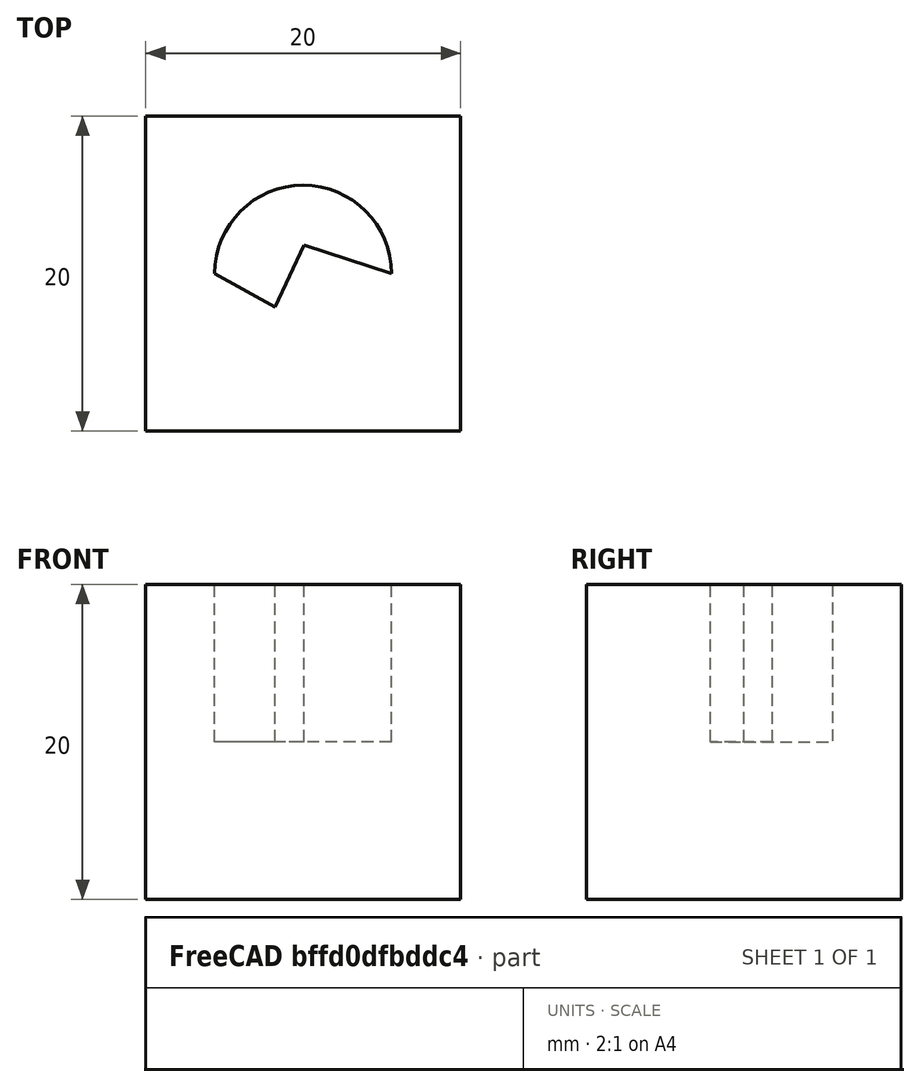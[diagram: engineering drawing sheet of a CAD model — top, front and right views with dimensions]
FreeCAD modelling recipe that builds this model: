
FCSTD DOCUMENT  (FreeCAD 1.0R39109 (Git))
Label: extrudeLimitation-1
License: All rights reserved
LicenseURL: http://en.wikipedia.org/wiki/All_rights_reserved
objects: App::DocumentObjectGroupPython×1248, App::Part×2, Part::FeaturePython×1, Sketcher::SketchObject×1, Part::Extrusion×1
note: 4 computed .brp shape members not serialized (recipe doc carries the construction recipe); baked Part::Feature solids carry a one-line shape summary decoded from their .brp

FEATURE [App::DocumentObjectGroupPython] HALFPI  # scripted group (container) (typed FeaturePython)
  name = HALFPI
  value = pi/2.
FEATURE [App::DocumentObjectGroupPython] PI  # scripted group (container) (typed FeaturePython)
  name = PI
  value = 1.*pi
FEATURE [App::DocumentObjectGroupPython] TWOPI  # scripted group (container) (typed FeaturePython)
  name = TWOPI
  value = 2.*pi
FEATURE [App::DocumentObjectGroupPython] Constants  # scripted group (container) (typed FeaturePython)
  Group = -> [HALFPI,PI,TWOPI]
FEATURE [App::DocumentObjectGroupPython] Variables  # scripted group (container) (typed FeaturePython)
FEATURE [App::DocumentObjectGroupPython] Quantities  # scripted group (container) (typed FeaturePython)
FEATURE [App::DocumentObjectGroupPython] Isotopes  # scripted group (container) (typed FeaturePython)
FEATURE [App::DocumentObjectGroupPython] Elements  # scripted group (container) (typed FeaturePython)
FEATURE [App::DocumentObjectGroupPython] G4Isotopes  # scripted group (container) (typed FeaturePython)
FEATURE [App::DocumentObjectGroupPython] H_element  # scripted group (container) (typed FeaturePython)
  Z = 1
  atom_value = 1.008
  formula = H
  name = H_element
FEATURE [App::DocumentObjectGroupPython] He_element  # scripted group (container) (typed FeaturePython)
  Z = 2
  atom_value = 4.0026
  formula = He
  name = He_element
FEATURE [App::DocumentObjectGroupPython] Li_element  # scripted group (container) (typed FeaturePython)
  Z = 3
  atom_value = 6.94
  formula = Li
  name = Li_element
FEATURE [App::DocumentObjectGroupPython] Be_element  # scripted group (container) (typed FeaturePython)
  Z = 4
  atom_value = 9.01218
  formula = Be
  name = Be_element
FEATURE [App::DocumentObjectGroupPython] B_element  # scripted group (container) (typed FeaturePython)
  Z = 5
  atom_value = 10.81
  formula = B
  name = B_element
FEATURE [App::DocumentObjectGroupPython] C_element  # scripted group (container) (typed FeaturePython)
  Z = 6
  atom_value = 12.011
  formula = C
  name = C_element
FEATURE [App::DocumentObjectGroupPython] N_element  # scripted group (container) (typed FeaturePython)
  Z = 7
  atom_value = 14.007
  formula = N
  name = N_element
FEATURE [App::DocumentObjectGroupPython] O_element  # scripted group (container) (typed FeaturePython)
  Z = 8
  atom_value = 15.999
  formula = O
  name = O_element
FEATURE [App::DocumentObjectGroupPython] F_element  # scripted group (container) (typed FeaturePython)
  Z = 9
  atom_value = 18.9984
  formula = F
  name = F_element
FEATURE [App::DocumentObjectGroupPython] Ne_element  # scripted group (container) (typed FeaturePython)
  Z = 10
  atom_value = 20.1797
  formula = Ne
  name = Ne_element
FEATURE [App::DocumentObjectGroupPython] Na_element  # scripted group (container) (typed FeaturePython)
  Z = 11
  atom_value = 22.9898
  formula = Na
  name = Na_element
FEATURE [App::DocumentObjectGroupPython] Mg_element  # scripted group (container) (typed FeaturePython)
  Z = 12
  atom_value = 24.305
  formula = Mg
  name = Mg_element
FEATURE [App::DocumentObjectGroupPython] Al_element  # scripted group (container) (typed FeaturePython)
  Z = 13
  atom_value = 26.9815
  formula = Al
  name = Al_element
FEATURE [App::DocumentObjectGroupPython] Si_element  # scripted group (container) (typed FeaturePython)
  Z = 14
  atom_value = 28.085
  formula = Si
  name = Si_element
FEATURE [App::DocumentObjectGroupPython] P_element  # scripted group (container) (typed FeaturePython)
  Z = 15
  atom_value = 30.9738
  formula = P
  name = P_element
FEATURE [App::DocumentObjectGroupPython] S_element  # scripted group (container) (typed FeaturePython)
  Z = 16
  atom_value = 32.06
  formula = S
  name = S_element
FEATURE [App::DocumentObjectGroupPython] Cl_element  # scripted group (container) (typed FeaturePython)
  Z = 17
  atom_value = 35.45
  formula = Cl
  name = Cl_element
FEATURE [App::DocumentObjectGroupPython] Ar_element  # scripted group (container) (typed FeaturePython)
  Z = 18
  atom_value = 39.95
  formula = Ar
  name = Ar_element
FEATURE [App::DocumentObjectGroupPython] K_element  # scripted group (container) (typed FeaturePython)
  Z = 19
  atom_value = 39.0983
  formula = K
  name = K_element
FEATURE [App::DocumentObjectGroupPython] Ca_element  # scripted group (container) (typed FeaturePython)
  Z = 20
  atom_value = 40.078
  formula = Ca
  name = Ca_element
FEATURE [App::DocumentObjectGroupPython] Sc_element  # scripted group (container) (typed FeaturePython)
  Z = 21
  atom_value = 44.9559
  formula = Sc
  name = Sc_element
FEATURE [App::DocumentObjectGroupPython] Ti_element  # scripted group (container) (typed FeaturePython)
  Z = 22
  atom_value = 47.867
  formula = Ti
  name = Ti_element
FEATURE [App::DocumentObjectGroupPython] V_element  # scripted group (container) (typed FeaturePython)
  Z = 23
  atom_value = 50.9415
  formula = V
  name = V_element
FEATURE [App::DocumentObjectGroupPython] Cr_element  # scripted group (container) (typed FeaturePython)
  Z = 24
  atom_value = 51.9961
  formula = Cr
  name = Cr_element
FEATURE [App::DocumentObjectGroupPython] Mn_element  # scripted group (container) (typed FeaturePython)
  Z = 25
  atom_value = 54.938
  formula = Mn
  name = Mn_element
FEATURE [App::DocumentObjectGroupPython] Fe_element  # scripted group (container) (typed FeaturePython)
  Z = 26
  atom_value = 55.845
  formula = Fe
  name = Fe_element
FEATURE [App::DocumentObjectGroupPython] Co_element  # scripted group (container) (typed FeaturePython)
  Z = 27
  atom_value = 58.9332
  formula = Co
  name = Co_element
FEATURE [App::DocumentObjectGroupPython] Ni_element  # scripted group (container) (typed FeaturePython)
  Z = 28
  atom_value = 58.6934
  formula = Ni
  name = Ni_element
FEATURE [App::DocumentObjectGroupPython] Cu_element  # scripted group (container) (typed FeaturePython)
  Z = 29
  atom_value = 63.546
  formula = Cu
  name = Cu_element
FEATURE [App::DocumentObjectGroupPython] Zn_element  # scripted group (container) (typed FeaturePython)
  Z = 30
  atom_value = 65.38
  formula = Zn
  name = Zn_element
FEATURE [App::DocumentObjectGroupPython] Ga_element  # scripted group (container) (typed FeaturePython)
  Z = 31
  atom_value = 69.723
  formula = Ga
  name = Ga_element
FEATURE [App::DocumentObjectGroupPython] Ge_element  # scripted group (container) (typed FeaturePython)
  Z = 32
  atom_value = 72.63
  formula = Ge
  name = Ge_element
FEATURE [App::DocumentObjectGroupPython] As_element  # scripted group (container) (typed FeaturePython)
  Z = 33
  atom_value = 74.9216
  formula = As
  name = As_element
FEATURE [App::DocumentObjectGroupPython] Se_element  # scripted group (container) (typed FeaturePython)
  Z = 34
  atom_value = 78.971
  formula = Se
  name = Se_element
FEATURE [App::DocumentObjectGroupPython] Br_element  # scripted group (container) (typed FeaturePython)
  Z = 35
  atom_value = 79.904
  formula = Br
  name = Br_element
FEATURE [App::DocumentObjectGroupPython] Kr_element  # scripted group (container) (typed FeaturePython)
  Z = 36
  atom_value = 83.798
  formula = Kr
  name = Kr_element
FEATURE [App::DocumentObjectGroupPython] Rb_element  # scripted group (container) (typed FeaturePython)
  Z = 37
  atom_value = 85.4678
  formula = Rb
  name = Rb_element
FEATURE [App::DocumentObjectGroupPython] Sr_element  # scripted group (container) (typed FeaturePython)
  Z = 38
  atom_value = 87.62
  formula = Sr
  name = Sr_element
FEATURE [App::DocumentObjectGroupPython] Y_element  # scripted group (container) (typed FeaturePython)
  Z = 39
  atom_value = 88.9058
  formula = Y
  name = Y_element
FEATURE [App::DocumentObjectGroupPython] Zr_element  # scripted group (container) (typed FeaturePython)
  Z = 40
  atom_value = 91.224
  formula = Zr
  name = Zr_element
FEATURE [App::DocumentObjectGroupPython] Nb_element  # scripted group (container) (typed FeaturePython)
  Z = 41
  atom_value = 92.9064
  formula = Nb
  name = Nb_element
FEATURE [App::DocumentObjectGroupPython] Mo_element  # scripted group (container) (typed FeaturePython)
  Z = 42
  atom_value = 95.95
  formula = Mo
  name = Mo_element
FEATURE [App::DocumentObjectGroupPython] Tc_element  # scripted group (container) (typed FeaturePython)
  Z = 43
  atom_value = 97
  formula = Tc
  name = Tc_element
FEATURE [App::DocumentObjectGroupPython] Ru_element  # scripted group (container) (typed FeaturePython)
  Z = 44
  atom_value = 101.07
  formula = Ru
  name = Ru_element
FEATURE [App::DocumentObjectGroupPython] Rh_element  # scripted group (container) (typed FeaturePython)
  Z = 45
  atom_value = 102.905
  formula = Rh
  name = Rh_element
FEATURE [App::DocumentObjectGroupPython] Pd_element  # scripted group (container) (typed FeaturePython)
  Z = 46
  atom_value = 106.42
  formula = Pd
  name = Pd_element
FEATURE [App::DocumentObjectGroupPython] Ag_element  # scripted group (container) (typed FeaturePython)
  Z = 47
  atom_value = 107.868
  formula = Ag
  name = Ag_element
FEATURE [App::DocumentObjectGroupPython] Cd_element  # scripted group (container) (typed FeaturePython)
  Z = 48
  atom_value = 112.414
  formula = Cd
  name = Cd_element
FEATURE [App::DocumentObjectGroupPython] In_element  # scripted group (container) (typed FeaturePython)
  Z = 49
  atom_value = 114.818
  formula = In
  name = In_element
FEATURE [App::DocumentObjectGroupPython] Sn_element  # scripted group (container) (typed FeaturePython)
  Z = 50
  atom_value = 118.71
  formula = Sn
  name = Sn_element
FEATURE [App::DocumentObjectGroupPython] Sb_element  # scripted group (container) (typed FeaturePython)
  Z = 51
  atom_value = 121.76
  formula = Sb
  name = Sb_element
FEATURE [App::DocumentObjectGroupPython] Te_element  # scripted group (container) (typed FeaturePython)
  Z = 52
  atom_value = 127.6
  formula = Te
  name = Te_element
FEATURE [App::DocumentObjectGroupPython] I_element  # scripted group (container) (typed FeaturePython)
  Z = 53
  atom_value = 126.904
  formula = I
  name = I_element
FEATURE [App::DocumentObjectGroupPython] Xe_element  # scripted group (container) (typed FeaturePython)
  Z = 54
  atom_value = 131.293
  formula = Xe
  name = Xe_element
FEATURE [App::DocumentObjectGroupPython] Cs_element  # scripted group (container) (typed FeaturePython)
  Z = 55
  atom_value = 132.905
  formula = Cs
  name = Cs_element
FEATURE [App::DocumentObjectGroupPython] Ba_element  # scripted group (container) (typed FeaturePython)
  Z = 56
  atom_value = 137.327
  formula = Ba
  name = Ba_element
FEATURE [App::DocumentObjectGroupPython] La_element  # scripted group (container) (typed FeaturePython)
  Z = 57
  atom_value = 138.905
  formula = La
  name = La_element
FEATURE [App::DocumentObjectGroupPython] Ce_element  # scripted group (container) (typed FeaturePython)
  Z = 58
  atom_value = 140.116
  formula = Ce
  name = Ce_element
FEATURE [App::DocumentObjectGroupPython] Pr_element  # scripted group (container) (typed FeaturePython)
  Z = 59
  atom_value = 140.908
  formula = Pr
  name = Pr_element
FEATURE [App::DocumentObjectGroupPython] Nd_element  # scripted group (container) (typed FeaturePython)
  Z = 60
  atom_value = 144.242
  formula = Nd
  name = Nd_element
FEATURE [App::DocumentObjectGroupPython] Pm_element  # scripted group (container) (typed FeaturePython)
  Z = 61
  atom_value = 145
  formula = Pm
  name = Pm_element
FEATURE [App::DocumentObjectGroupPython] Sm_element  # scripted group (container) (typed FeaturePython)
  Z = 62
  atom_value = 150.36
  formula = Sm
  name = Sm_element
FEATURE [App::DocumentObjectGroupPython] Eu_element  # scripted group (container) (typed FeaturePython)
  Z = 63
  atom_value = 151.964
  formula = Eu
  name = Eu_element
FEATURE [App::DocumentObjectGroupPython] Gd_element  # scripted group (container) (typed FeaturePython)
  Z = 64
  atom_value = 157.25
  formula = Gd
  name = Gd_element
FEATURE [App::DocumentObjectGroupPython] Tb_element  # scripted group (container) (typed FeaturePython)
  Z = 65
  atom_value = 158.925
  formula = Tb
  name = Tb_element
FEATURE [App::DocumentObjectGroupPython] Dy_element  # scripted group (container) (typed FeaturePython)
  Z = 66
  atom_value = 162.5
  formula = Dy
  name = Dy_element
FEATURE [App::DocumentObjectGroupPython] Ho_element  # scripted group (container) (typed FeaturePython)
  Z = 67
  atom_value = 164.93
  formula = Ho
  name = Ho_element
FEATURE [App::DocumentObjectGroupPython] Er_element  # scripted group (container) (typed FeaturePython)
  Z = 68
  atom_value = 167.259
  formula = Er
  name = Er_element
FEATURE [App::DocumentObjectGroupPython] Tm_element  # scripted group (container) (typed FeaturePython)
  Z = 69
  atom_value = 168.934
  formula = Tm
  name = Tm_element
FEATURE [App::DocumentObjectGroupPython] Yb_element  # scripted group (container) (typed FeaturePython)
  Z = 70
  atom_value = 173.045
  formula = Yb
  name = Yb_element
FEATURE [App::DocumentObjectGroupPython] Lu_element  # scripted group (container) (typed FeaturePython)
  Z = 71
  atom_value = 174.967
  formula = Lu
  name = Lu_element
FEATURE [App::DocumentObjectGroupPython] Hf_element  # scripted group (container) (typed FeaturePython)
  Z = 72
  atom_value = 178.49
  formula = Hf
  name = Hf_element
FEATURE [App::DocumentObjectGroupPython] Ta_element  # scripted group (container) (typed FeaturePython)
  Z = 73
  atom_value = 180.948
  formula = Ta
  name = Ta_element
FEATURE [App::DocumentObjectGroupPython] W_element  # scripted group (container) (typed FeaturePython)
  Z = 74
  atom_value = 183.84
  formula = W
  name = W_element
FEATURE [App::DocumentObjectGroupPython] Re_element  # scripted group (container) (typed FeaturePython)
  Z = 75
  atom_value = 186.207
  formula = Re
  name = Re_element
FEATURE [App::DocumentObjectGroupPython] Os_element  # scripted group (container) (typed FeaturePython)
  Z = 76
  atom_value = 190.23
  formula = Os
  name = Os_element
FEATURE [App::DocumentObjectGroupPython] Ir_element  # scripted group (container) (typed FeaturePython)
  Z = 77
  atom_value = 192.217
  formula = Ir
  name = Ir_element
FEATURE [App::DocumentObjectGroupPython] Pt_element  # scripted group (container) (typed FeaturePython)
  Z = 78
  atom_value = 195.084
  formula = Pt
  name = Pt_element
FEATURE [App::DocumentObjectGroupPython] Au_element  # scripted group (container) (typed FeaturePython)
  Z = 79
  atom_value = 196.967
  formula = Au
  name = Au_element
FEATURE [App::DocumentObjectGroupPython] Hg_element  # scripted group (container) (typed FeaturePython)
  Z = 80
  atom_value = 200.592
  formula = Hg
  name = Hg_element
FEATURE [App::DocumentObjectGroupPython] Tl_element  # scripted group (container) (typed FeaturePython)
  Z = 81
  atom_value = 204.38
  formula = Tl
  name = Tl_element
FEATURE [App::DocumentObjectGroupPython] Pb_element  # scripted group (container) (typed FeaturePython)
  Z = 82
  atom_value = 207.2
  formula = Pb
  name = Pb_element
FEATURE [App::DocumentObjectGroupPython] Bi_element  # scripted group (container) (typed FeaturePython)
  Z = 83
  atom_value = 208.98
  formula = Bi
  name = Bi_element
FEATURE [App::DocumentObjectGroupPython] Po_element  # scripted group (container) (typed FeaturePython)
  Z = 84
  atom_value = 209
  formula = Po
  name = Po_element
FEATURE [App::DocumentObjectGroupPython] At_element  # scripted group (container) (typed FeaturePython)
  Z = 85
  atom_value = 210
  formula = At
  name = At_element
FEATURE [App::DocumentObjectGroupPython] Rn_element  # scripted group (container) (typed FeaturePython)
  Z = 86
  atom_value = 222
  formula = Rn
  name = Rn_element
FEATURE [App::DocumentObjectGroupPython] Fr_element  # scripted group (container) (typed FeaturePython)
  Z = 87
  atom_value = 223
  formula = Fr
  name = Fr_element
FEATURE [App::DocumentObjectGroupPython] Ra_element  # scripted group (container) (typed FeaturePython)
  Z = 88
  atom_value = 226
  formula = Ra
  name = Ra_element
FEATURE [App::DocumentObjectGroupPython] Ac_element  # scripted group (container) (typed FeaturePython)
  Z = 89
  atom_value = 227
  formula = Ac
  name = Ac_element
FEATURE [App::DocumentObjectGroupPython] Th_element  # scripted group (container) (typed FeaturePython)
  Z = 90
  atom_value = 232.038
  formula = Th
  name = Th_element
FEATURE [App::DocumentObjectGroupPython] Pa_element  # scripted group (container) (typed FeaturePython)
  Z = 91
  atom_value = 231.036
  formula = Pa
  name = Pa_element
FEATURE [App::DocumentObjectGroupPython] U_element  # scripted group (container) (typed FeaturePython)
  Z = 92
  atom_value = 238.029
  formula = U
  name = U_element
FEATURE [App::DocumentObjectGroupPython] Np_element  # scripted group (container) (typed FeaturePython)
  Z = 93
  atom_value = 237
  formula = Np
  name = Np_element
FEATURE [App::DocumentObjectGroupPython] Pu_element  # scripted group (container) (typed FeaturePython)
  Z = 94
  atom_value = 244
  formula = Pu
  name = Pu_element
FEATURE [App::DocumentObjectGroupPython] Am_element  # scripted group (container) (typed FeaturePython)
  Z = 95
  atom_value = 243
  formula = Am
  name = Am_element
FEATURE [App::DocumentObjectGroupPython] Cm_element  # scripted group (container) (typed FeaturePython)
  Z = 96
  atom_value = 247
  formula = Cm
  name = Cm_element
FEATURE [App::DocumentObjectGroupPython] Bk_element  # scripted group (container) (typed FeaturePython)
  Z = 97
  atom_value = 247
  formula = Bk
  name = Bk_element
FEATURE [App::DocumentObjectGroupPython] Cf_element  # scripted group (container) (typed FeaturePython)
  Z = 98
  atom_value = 251
  formula = Cf
  name = Cf_element
FEATURE [App::DocumentObjectGroupPython] G4Elements  # scripted group (container) (typed FeaturePython)
  Group = -> [H_element,He_element,Li_element,Be_element,B_element,C_element,N_element,O_element,F_element,Ne_element,Na_element,Mg_element,Al_element,Si_element,P_element,S_element,Cl_element,Ar_element,K_element,Ca_element,Sc_element,Ti_element,V_element,Cr_element,Mn_element,Fe_element,Co_element,Ni_element,Cu_element,Zn_element,Ga_element,Ge_element,As_element,Se_element,Br_element,Kr_element,Rb_element,+61 more]
FEATURE [App::DocumentObjectGroupPython] H_element001  label="H_element : 0.101"  # scripted group (container) (typed FeaturePython)
  n = 0.101327
FEATURE [App::DocumentObjectGroupPython] C_element001  label="C_element : 0.775"  # scripted group (container) (typed FeaturePython)
  n = 0.7755
FEATURE [App::DocumentObjectGroupPython] N_element001  label="N_element : 0.035"  # scripted group (container) (typed FeaturePython)
  n = 0.035057
FEATURE [App::DocumentObjectGroupPython] O_element001  label="O_element : 0.052"  # scripted group (container) (typed FeaturePython)
  n = 0.0523159
FEATURE [App::DocumentObjectGroupPython] F_element001  label="F_element : 0.017"  # scripted group (container) (typed FeaturePython)
  n = 0.017422
FEATURE [App::DocumentObjectGroupPython] Ca_element001  label="Ca_element : 0.018"  # scripted group (container) (typed FeaturePython)
  n = 0.018378
FEATURE [App::DocumentObjectGroupPython] G4_A_150_TISSUE  label="G4_A-150_TISSUE"  # scripted group (container) (typed FeaturePython)
  Dunit = g/cm3
  Dvalue = 1.127
  Group = -> [H_element001,C_element001,N_element001,O_element001,F_element001,Ca_element001]
  conduct = 2
  density = 1
  expand = 3
  formula = G4_A-150_TISSUE
  name = G4_A-150_TISSUE
  specific = 4
FEATURE [App::DocumentObjectGroupPython] C_element002  label="C_element : 3"  # scripted group (container) (typed FeaturePython)
  n = 3
  ref = C_element
FEATURE [App::DocumentObjectGroupPython] H_element002  label="H_element : 6"  # scripted group (container) (typed FeaturePython)
  n = 6
  ref = H_element
FEATURE [App::DocumentObjectGroupPython] O_element002  label="O_element : 1"  # scripted group (container) (typed FeaturePython)
  n = 1
  ref = O_element
FEATURE [App::DocumentObjectGroupPython] G4_ACETONE  # scripted group (container) (typed FeaturePython)
  Dunit = g/cm3
  Dvalue = 0.7899
  Group = -> [C_element002,H_element002,O_element002]
  conduct = 2
  density = 1
  expand = 3
  formula = G4_ACETONE
  name = G4_ACETONE
  specific = 4
FEATURE [App::DocumentObjectGroupPython] C_element003  label="C_element : 2"  # scripted group (container) (typed FeaturePython)
  n = 2
  ref = C_element
FEATURE [App::DocumentObjectGroupPython] H_element003  label="H_element : 2"  # scripted group (container) (typed FeaturePython)
  n = 2
  ref = H_element
FEATURE [App::DocumentObjectGroupPython] G4_ACETYLENE  # scripted group (container) (typed FeaturePython)
  Dunit = g/cm3
  Dvalue = 0.0010967
  Group = -> [C_element003,H_element003]
  conduct = 2
  density = 1
  expand = 3
  formula = G4_ACETYLENE
  name = G4_ACETYLENE
  specific = 4
FEATURE [App::DocumentObjectGroupPython] C_element004  label="C_element : 5"  # scripted group (container) (typed FeaturePython)
  n = 5
  ref = C_element
FEATURE [App::DocumentObjectGroupPython] H_element004  label="H_element : 5"  # scripted group (container) (typed FeaturePython)
  n = 5
  ref = H_element
FEATURE [App::DocumentObjectGroupPython] N_element002  label="N_element : 5"  # scripted group (container) (typed FeaturePython)
  n = 5
  ref = N_element
FEATURE [App::DocumentObjectGroupPython] G4_ADENINE  # scripted group (container) (typed FeaturePython)
  Dunit = g/cm3
  Dvalue = 1.6
  Group = -> [C_element004,H_element004,N_element002]
  conduct = 2
  density = 1
  expand = 3
  formula = G4_ADENINE
  name = G4_ADENINE
  specific = 4
FEATURE [App::DocumentObjectGroupPython] H_element005  label="H_element : 0.114"  # scripted group (container) (typed FeaturePython)
  n = 0.114
FEATURE [App::DocumentObjectGroupPython] C_element005  label="C_element : 0.598"  # scripted group (container) (typed FeaturePython)
  n = 0.598
FEATURE [App::DocumentObjectGroupPython] N_element003  label="N_element : 0.007"  # scripted group (container) (typed FeaturePython)
  n = 0.007
FEATURE [App::DocumentObjectGroupPython] O_element003  label="O_element : 0.278"  # scripted group (container) (typed FeaturePython)
  n = 0.278
FEATURE [App::DocumentObjectGroupPython] Na_element001  label="Na_element : 0.001"  # scripted group (container) (typed FeaturePython)
  n = 0.001
FEATURE [App::DocumentObjectGroupPython] S_element001  label="S_element : 0.001"  # scripted group (container) (typed FeaturePython)
  n = 0.001
FEATURE [App::DocumentObjectGroupPython] Cl_element001  label="Cl_element : 0.001"  # scripted group (container) (typed FeaturePython)
  n = 0.001
FEATURE [App::DocumentObjectGroupPython] G4_ADIPOSE_TISSUE_ICRP  # scripted group (container) (typed FeaturePython)
  Dunit = g/cm3
  Dvalue = 0.95
  Group = -> [H_element005,C_element005,N_element003,O_element003,Na_element001,S_element001,Cl_element001]
  conduct = 2
  density = 1
  expand = 3
  formula = G4_ADIPOSE_TISSUE_ICRP
  name = G4_ADIPOSE_TISSUE_ICRP
  specific = 4
FEATURE [App::DocumentObjectGroupPython] C_element006  label="C_element : 0.000"  # scripted group (container) (typed FeaturePython)
  n = 0.000124
FEATURE [App::DocumentObjectGroupPython] N_element004  label="N_element : 0.755"  # scripted group (container) (typed FeaturePython)
  n = 0.755268
FEATURE [App::DocumentObjectGroupPython] O_element004  label="O_element : 0.232"  # scripted group (container) (typed FeaturePython)
  n = 0.231781
FEATURE [App::DocumentObjectGroupPython] Ar_element001  label="Ar_element : 0.013"  # scripted group (container) (typed FeaturePython)
  n = 0.012827
FEATURE [App::DocumentObjectGroupPython] G4_AIR  # scripted group (container) (typed FeaturePython)
  Dunit = g/cm3
  Dvalue = 0.00120479
  Group = -> [C_element006,N_element004,O_element004,Ar_element001]
  conduct = 2
  density = 1
  expand = 3
  formula = G4_AIR
  name = G4_AIR
  specific = 4
FEATURE [App::DocumentObjectGroupPython] C_element007  label="C_element : 006"  # scripted group (container) (typed FeaturePython)
  n = 3
  ref = C_element
FEATURE [App::DocumentObjectGroupPython] H_element006  label="H_element : 7"  # scripted group (container) (typed FeaturePython)
  n = 7
  ref = H_element
FEATURE [App::DocumentObjectGroupPython] N_element005  label="N_element : 1"  # scripted group (container) (typed FeaturePython)
  n = 1
  ref = N_element
FEATURE [App::DocumentObjectGroupPython] O_element005  label="O_element : 2"  # scripted group (container) (typed FeaturePython)
  n = 2
  ref = O_element
FEATURE [App::DocumentObjectGroupPython] G4_ALANINE  # scripted group (container) (typed FeaturePython)
  Dunit = g/cm3
  Dvalue = 1.42
  Group = -> [C_element007,H_element006,N_element005,O_element005]
  conduct = 2
  density = 1
  expand = 3
  formula = G4_ALANINE
  name = G4_ALANINE
  specific = 4
FEATURE [App::DocumentObjectGroupPython] Al_element001  label="Al_element : 2"  # scripted group (container) (typed FeaturePython)
  n = 2
  ref = Al_element
FEATURE [App::DocumentObjectGroupPython] O_element006  label="O_element : 3"  # scripted group (container) (typed FeaturePython)
  n = 3
  ref = O_element
FEATURE [App::DocumentObjectGroupPython] G4_ALUMINUM_OXIDE  # scripted group (container) (typed FeaturePython)
  Dunit = g/cm3
  Dvalue = 3.97
  Group = -> [Al_element001,O_element006]
  conduct = 2
  density = 1
  expand = 3
  formula = G4_ALUMINUM_OXIDE
  name = G4_ALUMINUM_OXIDE
  specific = 4
FEATURE [App::DocumentObjectGroupPython] H_element007  label="H_element : 0.106"  # scripted group (container) (typed FeaturePython)
  n = 0.10593
FEATURE [App::DocumentObjectGroupPython] C_element008  label="C_element : 0.789"  # scripted group (container) (typed FeaturePython)
  n = 0.788974
FEATURE [App::DocumentObjectGroupPython] O_element007  label="O_element : 0.105"  # scripted group (container) (typed FeaturePython)
  n = 0.105096
FEATURE [App::DocumentObjectGroupPython] G4_AMBER  # scripted group (container) (typed FeaturePython)
  Dunit = g/cm3
  Dvalue = 1.1
  Group = -> [H_element007,C_element008,O_element007]
  conduct = 2
  density = 1
  expand = 3
  formula = G4_AMBER
  name = G4_AMBER
  specific = 4
FEATURE [App::DocumentObjectGroupPython] N_element006  label="N_element : 006"  # scripted group (container) (typed FeaturePython)
  n = 1
  ref = N_element
FEATURE [App::DocumentObjectGroupPython] H_element008  label="H_element : 3"  # scripted group (container) (typed FeaturePython)
  n = 3
  ref = H_element
FEATURE [App::DocumentObjectGroupPython] G4_AMMONIA  # scripted group (container) (typed FeaturePython)
  Dunit = g/cm3
  Dvalue = 0.000826019
  Group = -> [N_element006,H_element008]
  conduct = 2
  density = 1
  expand = 3
  formula = G4_AMMONIA
  name = G4_AMMONIA
  specific = 4
FEATURE [App::DocumentObjectGroupPython] C_element009  label="C_element : 6"  # scripted group (container) (typed FeaturePython)
  n = 6
  ref = C_element
FEATURE [App::DocumentObjectGroupPython] H_element009  label="H_element : 008"  # scripted group (container) (typed FeaturePython)
  n = 7
  ref = H_element
FEATURE [App::DocumentObjectGroupPython] N_element007  label="N_element : 007"  # scripted group (container) (typed FeaturePython)
  n = 1
  ref = N_element
FEATURE [App::DocumentObjectGroupPython] G4_ANILINE  # scripted group (container) (typed FeaturePython)
  Dunit = g/cm3
  Dvalue = 1.0235
  Group = -> [C_element009,H_element009,N_element007]
  conduct = 2
  density = 1
  expand = 3
  formula = G4_ANILINE
  name = G4_ANILINE
  specific = 4
FEATURE [App::DocumentObjectGroupPython] C_element010  label="C_element : 14"  # scripted group (container) (typed FeaturePython)
  n = 14
  ref = C_element
FEATURE [App::DocumentObjectGroupPython] H_element010  label="H_element : 10"  # scripted group (container) (typed FeaturePython)
  n = 10
  ref = H_element
FEATURE [App::DocumentObjectGroupPython] G4_ANTHRACENE  # scripted group (container) (typed FeaturePython)
  Dunit = g/cm3
  Dvalue = 1.283
  Group = -> [C_element010,H_element010]
  conduct = 2
  density = 1
  expand = 3
  formula = G4_ANTHRACENE
  name = G4_ANTHRACENE
  specific = 4
FEATURE [App::DocumentObjectGroupPython] H_element011  label="H_element : 0.065"  # scripted group (container) (typed FeaturePython)
  n = 0.0654709
FEATURE [App::DocumentObjectGroupPython] C_element011  label="C_element : 0.537"  # scripted group (container) (typed FeaturePython)
  n = 0.536944
FEATURE [App::DocumentObjectGroupPython] N_element008  label="N_element : 0.021"  # scripted group (container) (typed FeaturePython)
  n = 0.0215
FEATURE [App::DocumentObjectGroupPython] O_element008  label="O_element : 0.032"  # scripted group (container) (typed FeaturePython)
  n = 0.032085
FEATURE [App::DocumentObjectGroupPython] F_element002  label="F_element : 0.167"  # scripted group (container) (typed FeaturePython)
  n = 0.167411
FEATURE [App::DocumentObjectGroupPython] Ca_element002  label="Ca_element : 0.177"  # scripted group (container) (typed FeaturePython)
  n = 0.176589
FEATURE [App::DocumentObjectGroupPython] G4_B_100_BONE  label="G4_B-100_BONE"  # scripted group (container) (typed FeaturePython)
  Dunit = g/cm3
  Dvalue = 1.45
  Group = -> [H_element011,C_element011,N_element008,O_element008,F_element002,Ca_element002]
  conduct = 2
  density = 1
  expand = 3
  formula = G4_B-100_BONE
  name = G4_B-100_BONE
  specific = 4
FEATURE [App::DocumentObjectGroupPython] H_element012  label="H_element : 0.057"  # scripted group (container) (typed FeaturePython)
  n = 0.057441
FEATURE [App::DocumentObjectGroupPython] C_element012  label="C_element : 0.790"  # scripted group (container) (typed FeaturePython)
  n = 0.774591
FEATURE [App::DocumentObjectGroupPython] O_element009  label="O_element : 0.168"  # scripted group (container) (typed FeaturePython)
  n = 0.167968
FEATURE [App::DocumentObjectGroupPython] G4_BAKELITE  # scripted group (container) (typed FeaturePython)
  Dunit = g/cm3
  Dvalue = 1.25
  Group = -> [H_element012,C_element012,O_element009]
  conduct = 2
  density = 1
  expand = 3
  formula = G4_BAKELITE
  name = G4_BAKELITE
  specific = 4
FEATURE [App::DocumentObjectGroupPython] Ba_element001  label="Ba_element : 1"  # scripted group (container) (typed FeaturePython)
  n = 1
  ref = Ba_element
FEATURE [App::DocumentObjectGroupPython] F_element003  label="F_element : 2"  # scripted group (container) (typed FeaturePython)
  n = 2
  ref = F_element
FEATURE [App::DocumentObjectGroupPython] G4_BARIUM_FLUORIDE  # scripted group (container) (typed FeaturePython)
  Dunit = g/cm3
  Dvalue = 4.89
  Group = -> [Ba_element001,F_element003]
  conduct = 2
  density = 1
  expand = 3
  formula = G4_BARIUM_FLUORIDE
  name = G4_BARIUM_FLUORIDE
  specific = 4
FEATURE [App::DocumentObjectGroupPython] Ba_element002  label="Ba_element : 002"  # scripted group (container) (typed FeaturePython)
  n = 1
  ref = Ba_element
FEATURE [App::DocumentObjectGroupPython] S_element002  label="S_element : 1"  # scripted group (container) (typed FeaturePython)
  n = 1
  ref = S_element
FEATURE [App::DocumentObjectGroupPython] O_element010  label="O_element : 4"  # scripted group (container) (typed FeaturePython)
  n = 4
  ref = O_element
FEATURE [App::DocumentObjectGroupPython] G4_BARIUM_SULFATE  # scripted group (container) (typed FeaturePython)
  Dunit = g/cm3
  Dvalue = 4.5
  Group = -> [Ba_element002,S_element002,O_element010]
  conduct = 2
  density = 1
  expand = 3
  formula = G4_BARIUM_SULFATE
  name = G4_BARIUM_SULFATE
  specific = 4
FEATURE [App::DocumentObjectGroupPython] C_element013  label="C_element : 007"  # scripted group (container) (typed FeaturePython)
  n = 6
  ref = C_element
FEATURE [App::DocumentObjectGroupPython] H_element013  label="H_element : 009"  # scripted group (container) (typed FeaturePython)
  n = 6
  ref = H_element
FEATURE [App::DocumentObjectGroupPython] G4_BENZENE  # scripted group (container) (typed FeaturePython)
  Dunit = g/cm3
  Dvalue = 0.87865
  Group = -> [C_element013,H_element013]
  conduct = 2
  density = 1
  expand = 3
  formula = G4_BENZENE
  name = G4_BENZENE
  specific = 4
FEATURE [App::DocumentObjectGroupPython] Be_element001  label="Be_element : 1"  # scripted group (container) (typed FeaturePython)
  n = 1
  ref = Be_element
FEATURE [App::DocumentObjectGroupPython] O_element011  label="O_element : 005"  # scripted group (container) (typed FeaturePython)
  n = 1
  ref = O_element
FEATURE [App::DocumentObjectGroupPython] G4_BERYLLIUM_OXIDE  # scripted group (container) (typed FeaturePython)
  Dunit = g/cm3
  Dvalue = 3.01
  Group = -> [Be_element001,O_element011]
  conduct = 2
  density = 1
  expand = 3
  formula = G4_BERYLLIUM_OXIDE
  name = G4_BERYLLIUM_OXIDE
  specific = 4
FEATURE [App::DocumentObjectGroupPython] Bi_element001  label="Bi_element : 4"  # scripted group (container) (typed FeaturePython)
  n = 4
  ref = Bi_element
FEATURE [App::DocumentObjectGroupPython] Ge_element001  label="Ge_element : 3"  # scripted group (container) (typed FeaturePython)
  n = 3
  ref = Ge_element
FEATURE [App::DocumentObjectGroupPython] O_element012  label="O_element : 12"  # scripted group (container) (typed FeaturePython)
  n = 12
  ref = O_element
FEATURE [App::DocumentObjectGroupPython] G4_BGO  # scripted group (container) (typed FeaturePython)
  Dunit = g/cm3
  Dvalue = 7.13
  Group = -> [Bi_element001,Ge_element001,O_element012]
  conduct = 2
  density = 1
  expand = 3
  formula = G4_BGO
  name = G4_BGO
  specific = 4
FEATURE [App::DocumentObjectGroupPython] H_element014  label="H_element : 0.102"  # scripted group (container) (typed FeaturePython)
  n = 0.102
FEATURE [App::DocumentObjectGroupPython] C_element014  label="C_element : 0.110"  # scripted group (container) (typed FeaturePython)
  n = 0.11
FEATURE [App::DocumentObjectGroupPython] N_element009  label="N_element : 0.033"  # scripted group (container) (typed FeaturePython)
  n = 0.033
FEATURE [App::DocumentObjectGroupPython] O_element013  label="O_element : 0.745"  # scripted group (container) (typed FeaturePython)
  n = 0.745
FEATURE [App::DocumentObjectGroupPython] Na_element002  label="Na_element : 0.002"  # scripted group (container) (typed FeaturePython)
  n = 0.001
FEATURE [App::DocumentObjectGroupPython] P_element001  label="P_element : 0.001"  # scripted group (container) (typed FeaturePython)
  n = 0.001
FEATURE [App::DocumentObjectGroupPython] S_element003  label="S_element : 0.002"  # scripted group (container) (typed FeaturePython)
  n = 0.002
FEATURE [App::DocumentObjectGroupPython] Cl_element002  label="Cl_element : 0.003"  # scripted group (container) (typed FeaturePython)
  n = 0.003
FEATURE [App::DocumentObjectGroupPython] K_element001  label="K_element : 0.002"  # scripted group (container) (typed FeaturePython)
  n = 0.002
FEATURE [App::DocumentObjectGroupPython] Fe_element001  label="Fe_element : 0.001"  # scripted group (container) (typed FeaturePython)
  n = 0.001
FEATURE [App::DocumentObjectGroupPython] G4_BLOOD_ICRP  # scripted group (container) (typed FeaturePython)
  Dunit = g/cm3
  Dvalue = 1.06
  Group = -> [H_element014,C_element014,N_element009,O_element013,Na_element002,P_element001,S_element003,Cl_element002,K_element001,Fe_element001]
  conduct = 2
  density = 1
  expand = 3
  formula = G4_BLOOD_ICRP
  name = G4_BLOOD_ICRP
  specific = 4
FEATURE [App::DocumentObjectGroupPython] H_element015  label="H_element : 0.064"  # scripted group (container) (typed FeaturePython)
  n = 0.064
FEATURE [App::DocumentObjectGroupPython] C_element015  label="C_element : 0.278"  # scripted group (container) (typed FeaturePython)
  n = 0.278
FEATURE [App::DocumentObjectGroupPython] N_element010  label="N_element : 0.027"  # scripted group (container) (typed FeaturePython)
  n = 0.027
FEATURE [App::DocumentObjectGroupPython] O_element014  label="O_element : 0.410"  # scripted group (container) (typed FeaturePython)
  n = 0.41
FEATURE [App::DocumentObjectGroupPython] Mg_element001  label="Mg_element : 0.002"  # scripted group (container) (typed FeaturePython)
  n = 0.002
FEATURE [App::DocumentObjectGroupPython] P_element002  label="P_element : 0.070"  # scripted group (container) (typed FeaturePython)
  n = 0.07
FEATURE [App::DocumentObjectGroupPython] S_element004  label="S_element : 0.003"  # scripted group (container) (typed FeaturePython)
  n = 0.002
FEATURE [App::DocumentObjectGroupPython] Ca_element003  label="Ca_element : 0.147"  # scripted group (container) (typed FeaturePython)
  n = 0.147
FEATURE [App::DocumentObjectGroupPython] G4_BONE_COMPACT_ICRU  # scripted group (container) (typed FeaturePython)
  Dunit = g/cm3
  Dvalue = 1.85
  Group = -> [H_element015,C_element015,N_element010,O_element014,Mg_element001,P_element002,S_element004,Ca_element003]
  conduct = 2
  density = 1
  expand = 3
  formula = G4_BONE_COMPACT_ICRU
  name = G4_BONE_COMPACT_ICRU
  specific = 4
FEATURE [App::DocumentObjectGroupPython] H_element016  label="H_element : 0.034"  # scripted group (container) (typed FeaturePython)
  n = 0.034
FEATURE [App::DocumentObjectGroupPython] C_element016  label="C_element : 0.155"  # scripted group (container) (typed FeaturePython)
  n = 0.155
FEATURE [App::DocumentObjectGroupPython] N_element011  label="N_element : 0.042"  # scripted group (container) (typed FeaturePython)
  n = 0.042
FEATURE [App::DocumentObjectGroupPython] O_element015  label="O_element : 0.435"  # scripted group (container) (typed FeaturePython)
  n = 0.435
FEATURE [App::DocumentObjectGroupPython] Na_element003  label="Na_element : 0.003"  # scripted group (container) (typed FeaturePython)
  n = 0.001
FEATURE [App::DocumentObjectGroupPython] Mg_element002  label="Mg_element : 0.003"  # scripted group (container) (typed FeaturePython)
  n = 0.002
FEATURE [App::DocumentObjectGroupPython] P_element003  label="P_element : 0.103"  # scripted group (container) (typed FeaturePython)
  n = 0.103
FEATURE [App::DocumentObjectGroupPython] S_element005  label="S_element : 0.004"  # scripted group (container) (typed FeaturePython)
  n = 0.003
FEATURE [App::DocumentObjectGroupPython] Ca_element004  label="Ca_element : 0.225"  # scripted group (container) (typed FeaturePython)
  n = 0.225
FEATURE [App::DocumentObjectGroupPython] G4_BONE_CORTICAL_ICRP  # scripted group (container) (typed FeaturePython)
  Dunit = g/cm3
  Dvalue = 1.92
  Group = -> [H_element016,C_element016,N_element011,O_element015,Na_element003,Mg_element002,P_element003,S_element005,Ca_element004]
  conduct = 2
  density = 1
  expand = 3
  formula = G4_BONE_CORTICAL_ICRP
  name = G4_BONE_CORTICAL_ICRP
  specific = 4
FEATURE [App::DocumentObjectGroupPython] B_element001  label="B_element : 4"  # scripted group (container) (typed FeaturePython)
  n = 4
  ref = B_element
FEATURE [App::DocumentObjectGroupPython] C_element017  label="C_element : 1"  # scripted group (container) (typed FeaturePython)
  n = 1
  ref = C_element
FEATURE [App::DocumentObjectGroupPython] G4_BORON_CARBIDE  # scripted group (container) (typed FeaturePython)
  Dunit = g/cm3
  Dvalue = 2.52
  Group = -> [B_element001,C_element017]
  conduct = 2
  density = 1
  expand = 3
  formula = G4_BORON_CARBIDE
  name = G4_BORON_CARBIDE
  specific = 4
FEATURE [App::DocumentObjectGroupPython] B_element002  label="B_element : 2"  # scripted group (container) (typed FeaturePython)
  n = 2
  ref = B_element
FEATURE [App::DocumentObjectGroupPython] O_element016  label="O_element : 006"  # scripted group (container) (typed FeaturePython)
  n = 3
  ref = O_element
FEATURE [App::DocumentObjectGroupPython] G4_BORON_OXIDE  # scripted group (container) (typed FeaturePython)
  Dunit = g/cm3
  Dvalue = 1.812
  Group = -> [B_element002,O_element016]
  conduct = 2
  density = 1
  expand = 3
  formula = G4_BORON_OXIDE
  name = G4_BORON_OXIDE
  specific = 4
FEATURE [App::DocumentObjectGroupPython] H_element017  label="H_element : 0.107"  # scripted group (container) (typed FeaturePython)
  n = 0.107
FEATURE [App::DocumentObjectGroupPython] C_element018  label="C_element : 0.145"  # scripted group (container) (typed FeaturePython)
  n = 0.145
FEATURE [App::DocumentObjectGroupPython] N_element012  label="N_element : 0.022"  # scripted group (container) (typed FeaturePython)
  n = 0.022
FEATURE [App::DocumentObjectGroupPython] O_element017  label="O_element : 0.712"  # scripted group (container) (typed FeaturePython)
  n = 0.712
FEATURE [App::DocumentObjectGroupPython] Na_element004  label="Na_element : 0.004"  # scripted group (container) (typed FeaturePython)
  n = 0.002
FEATURE [App::DocumentObjectGroupPython] P_element004  label="P_element : 0.004"  # scripted group (container) (typed FeaturePython)
  n = 0.004
FEATURE [App::DocumentObjectGroupPython] S_element006  label="S_element : 0.005"  # scripted group (container) (typed FeaturePython)
  n = 0.002
FEATURE [App::DocumentObjectGroupPython] Cl_element003  label="Cl_element : 0.004"  # scripted group (container) (typed FeaturePython)
  n = 0.003
FEATURE [App::DocumentObjectGroupPython] K_element002  label="K_element : 0.003"  # scripted group (container) (typed FeaturePython)
  n = 0.003
FEATURE [App::DocumentObjectGroupPython] G4_BRAIN_ICRP  # scripted group (container) (typed FeaturePython)
  Dunit = g/cm3
  Dvalue = 1.04
  Group = -> [H_element017,C_element018,N_element012,O_element017,Na_element004,P_element004,S_element006,Cl_element003,K_element002]
  conduct = 2
  density = 1
  expand = 3
  formula = G4_BRAIN_ICRP
  name = G4_BRAIN_ICRP
  specific = 4
FEATURE [App::DocumentObjectGroupPython] C_element019  label="C_element : 4"  # scripted group (container) (typed FeaturePython)
  n = 4
  ref = C_element
FEATURE [App::DocumentObjectGroupPython] H_element018  label="H_element : 010"  # scripted group (container) (typed FeaturePython)
  n = 10
  ref = H_element
FEATURE [App::DocumentObjectGroupPython] G4_BUTANE  # scripted group (container) (typed FeaturePython)
  Dunit = g/cm3
  Dvalue = 0.00249343
  Group = -> [C_element019,H_element018]
  conduct = 2
  density = 1
  expand = 3
  formula = G4_BUTANE
  name = G4_BUTANE
  specific = 4
FEATURE [App::DocumentObjectGroupPython] C_element020  label="C_element : 008"  # scripted group (container) (typed FeaturePython)
  n = 4
  ref = C_element
FEATURE [App::DocumentObjectGroupPython] H_element019  label="H_element : 011"  # scripted group (container) (typed FeaturePython)
  n = 10
  ref = H_element
FEATURE [App::DocumentObjectGroupPython] O_element018  label="O_element : 007"  # scripted group (container) (typed FeaturePython)
  n = 1
  ref = O_element
FEATURE [App::DocumentObjectGroupPython] G4_N_BUTYL_ALCOHOL  label="G4_N-BUTYL_ALCOHOL"  # scripted group (container) (typed FeaturePython)
  Dunit = g/cm3
  Dvalue = 0.8098
  Group = -> [C_element020,H_element019,O_element018]
  conduct = 2
  density = 1
  expand = 3
  formula = G4_N-BUTYL_ALCOHOL
  name = G4_N-BUTYL_ALCOHOL
  specific = 4
FEATURE [App::DocumentObjectGroupPython] H_element020  label="H_element : 0.025"  # scripted group (container) (typed FeaturePython)
  n = 0.02468
FEATURE [App::DocumentObjectGroupPython] C_element021  label="C_element : 0.502"  # scripted group (container) (typed FeaturePython)
  n = 0.501611
FEATURE [App::DocumentObjectGroupPython] O_element019  label="O_element : 0.005"  # scripted group (container) (typed FeaturePython)
  n = 0.004527
FEATURE [App::DocumentObjectGroupPython] F_element004  label="F_element : 0.465"  # scripted group (container) (typed FeaturePython)
  n = 0.465209
FEATURE [App::DocumentObjectGroupPython] Si_element001  label="Si_element : 0.004"  # scripted group (container) (typed FeaturePython)
  n = 0.003973
FEATURE [App::DocumentObjectGroupPython] G4_C_552  label="G4_C-552"  # scripted group (container) (typed FeaturePython)
  Dunit = g/cm3
  Dvalue = 1.76
  Group = -> [H_element020,C_element021,O_element019,F_element004,Si_element001]
  conduct = 2
  density = 1
  expand = 3
  formula = G4_C-552
  name = G4_C-552
  specific = 4
FEATURE [App::DocumentObjectGroupPython] Cd_element001  label="Cd_element : 1"  # scripted group (container) (typed FeaturePython)
  n = 1
  ref = Cd_element
FEATURE [App::DocumentObjectGroupPython] Te_element001  label="Te_element : 1"  # scripted group (container) (typed FeaturePython)
  n = 1
  ref = Te_element
FEATURE [App::DocumentObjectGroupPython] G4_CADMIUM_TELLURIDE  # scripted group (container) (typed FeaturePython)
  Dunit = g/cm3
  Dvalue = 6.2
  Group = -> [Cd_element001,Te_element001]
  conduct = 2
  density = 1
  expand = 3
  formula = G4_CADMIUM_TELLURIDE
  name = G4_CADMIUM_TELLURIDE
  specific = 4
FEATURE [App::DocumentObjectGroupPython] Cd_element002  label="Cd_element : 002"  # scripted group (container) (typed FeaturePython)
  n = 1
  ref = Cd_element
FEATURE [App::DocumentObjectGroupPython] W_element001  label="W_element : 1"  # scripted group (container) (typed FeaturePython)
  n = 1
  ref = W_element
FEATURE [App::DocumentObjectGroupPython] O_element020  label="O_element : 008"  # scripted group (container) (typed FeaturePython)
  n = 4
  ref = O_element
FEATURE [App::DocumentObjectGroupPython] G4_CADMIUM_TUNGSTATE  # scripted group (container) (typed FeaturePython)
  Dunit = g/cm3
  Dvalue = 7.9
  Group = -> [Cd_element002,W_element001,O_element020]
  conduct = 2
  density = 1
  expand = 3
  formula = G4_CADMIUM_TUNGSTATE
  name = G4_CADMIUM_TUNGSTATE
  specific = 4
FEATURE [App::DocumentObjectGroupPython] Ca_element005  label="Ca_element : 1"  # scripted group (container) (typed FeaturePython)
  n = 1
  ref = Ca_element
FEATURE [App::DocumentObjectGroupPython] C_element022  label="C_element : 009"  # scripted group (container) (typed FeaturePython)
  n = 1
  ref = C_element
FEATURE [App::DocumentObjectGroupPython] O_element021  label="O_element : 009"  # scripted group (container) (typed FeaturePython)
  n = 3
  ref = O_element
FEATURE [App::DocumentObjectGroupPython] G4_CALCIUM_CARBONATE  # scripted group (container) (typed FeaturePython)
  Dunit = g/cm3
  Dvalue = 2.8
  Group = -> [Ca_element005,C_element022,O_element021]
  conduct = 2
  density = 1
  expand = 3
  formula = G4_CALCIUM_CARBONATE
  name = G4_CALCIUM_CARBONATE
  specific = 4
FEATURE [App::DocumentObjectGroupPython] Ca_element006  label="Ca_element : 002"  # scripted group (container) (typed FeaturePython)
  n = 1
  ref = Ca_element
FEATURE [App::DocumentObjectGroupPython] F_element005  label="F_element : 003"  # scripted group (container) (typed FeaturePython)
  n = 2
  ref = F_element
FEATURE [App::DocumentObjectGroupPython] G4_CALCIUM_FLUORIDE  # scripted group (container) (typed FeaturePython)
  Dunit = g/cm3
  Dvalue = 3.18
  Group = -> [Ca_element006,F_element005]
  conduct = 2
  density = 1
  expand = 3
  formula = G4_CALCIUM_FLUORIDE
  name = G4_CALCIUM_FLUORIDE
  specific = 4
FEATURE [App::DocumentObjectGroupPython] Ca_element007  label="Ca_element : 003"  # scripted group (container) (typed FeaturePython)
  n = 1
  ref = Ca_element
FEATURE [App::DocumentObjectGroupPython] O_element022  label="O_element : 010"  # scripted group (container) (typed FeaturePython)
  n = 1
  ref = O_element
FEATURE [App::DocumentObjectGroupPython] G4_CALCIUM_OXIDE  # scripted group (container) (typed FeaturePython)
  Dunit = g/cm3
  Dvalue = 3.3
  Group = -> [Ca_element007,O_element022]
  conduct = 2
  density = 1
  expand = 3
  formula = G4_CALCIUM_OXIDE
  name = G4_CALCIUM_OXIDE
  specific = 4
FEATURE [App::DocumentObjectGroupPython] Ca_element008  label="Ca_element : 004"  # scripted group (container) (typed FeaturePython)
  n = 1
  ref = Ca_element
FEATURE [App::DocumentObjectGroupPython] S_element007  label="S_element : 002"  # scripted group (container) (typed FeaturePython)
  n = 1
  ref = S_element
FEATURE [App::DocumentObjectGroupPython] O_element023  label="O_element : 011"  # scripted group (container) (typed FeaturePython)
  n = 4
  ref = O_element
FEATURE [App::DocumentObjectGroupPython] G4_CALCIUM_SULFATE  # scripted group (container) (typed FeaturePython)
  Dunit = g/cm3
  Dvalue = 2.96
  Group = -> [Ca_element008,S_element007,O_element023]
  conduct = 2
  density = 1
  expand = 3
  formula = G4_CALCIUM_SULFATE
  name = G4_CALCIUM_SULFATE
  specific = 4
FEATURE [App::DocumentObjectGroupPython] Ca_element009  label="Ca_element : 005"  # scripted group (container) (typed FeaturePython)
  n = 1
  ref = Ca_element
FEATURE [App::DocumentObjectGroupPython] W_element002  label="W_element : 002"  # scripted group (container) (typed FeaturePython)
  n = 1
  ref = W_element
FEATURE [App::DocumentObjectGroupPython] O_element024  label="O_element : 012"  # scripted group (container) (typed FeaturePython)
  n = 4
  ref = O_element
FEATURE [App::DocumentObjectGroupPython] G4_CALCIUM_TUNGSTATE  # scripted group (container) (typed FeaturePython)
  Dunit = g/cm3
  Dvalue = 6.062
  Group = -> [Ca_element009,W_element002,O_element024]
  conduct = 2
  density = 1
  expand = 3
  formula = G4_CALCIUM_TUNGSTATE
  name = G4_CALCIUM_TUNGSTATE
  specific = 4
FEATURE [App::DocumentObjectGroupPython] C_element023  label="C_element : 010"  # scripted group (container) (typed FeaturePython)
  n = 1
  ref = C_element
FEATURE [App::DocumentObjectGroupPython] O_element025  label="O_element : 013"  # scripted group (container) (typed FeaturePython)
  n = 2
  ref = O_element
FEATURE [App::DocumentObjectGroupPython] G4_CARBON_DIOXIDE  # scripted group (container) (typed FeaturePython)
  Dunit = g/cm3
  Dvalue = 0.00184212
  Group = -> [C_element023,O_element025]
  conduct = 2
  density = 1
  expand = 3
  formula = G4_CARBON_DIOXIDE
  name = G4_CARBON_DIOXIDE
  specific = 4
FEATURE [App::DocumentObjectGroupPython] C_element024  label="C_element : 011"  # scripted group (container) (typed FeaturePython)
  n = 1
  ref = C_element
FEATURE [App::DocumentObjectGroupPython] Cl_element004  label="Cl_element : 4"  # scripted group (container) (typed FeaturePython)
  n = 4
  ref = Cl_element
FEATURE [App::DocumentObjectGroupPython] G4_CARBON_TETRACHLORIDE  # scripted group (container) (typed FeaturePython)
  Dunit = g/cm3
  Dvalue = 1.594
  Group = -> [C_element024,Cl_element004]
  conduct = 2
  density = 1
  expand = 3
  formula = G4_CARBON_TETRACHLORIDE
  name = G4_CARBON_TETRACHLORIDE
  specific = 4
FEATURE [App::DocumentObjectGroupPython] C_element025  label="C_element : 012"  # scripted group (container) (typed FeaturePython)
  n = 6
  ref = C_element
FEATURE [App::DocumentObjectGroupPython] H_element021  label="H_element : 012"  # scripted group (container) (typed FeaturePython)
  n = 10
  ref = H_element
FEATURE [App::DocumentObjectGroupPython] O_element026  label="O_element : 5"  # scripted group (container) (typed FeaturePython)
  n = 5
  ref = O_element
FEATURE [App::DocumentObjectGroupPython] G4_CELLULOSE_CELLOPHANE  # scripted group (container) (typed FeaturePython)
  Dunit = g/cm3
  Dvalue = 1.42
  Group = -> [C_element025,H_element021,O_element026]
  conduct = 2
  density = 1
  expand = 3
  formula = G4_CELLULOSE_CELLOPHANE
  name = G4_CELLULOSE_CELLOPHANE
  specific = 4
FEATURE [App::DocumentObjectGroupPython] H_element022  label="H_element : 0.067"  # scripted group (container) (typed FeaturePython)
  n = 0.067125
FEATURE [App::DocumentObjectGroupPython] C_element026  label="C_element : 0.545"  # scripted group (container) (typed FeaturePython)
  n = 0.545403
FEATURE [App::DocumentObjectGroupPython] O_element027  label="O_element : 0.387"  # scripted group (container) (typed FeaturePython)
  n = 0.387472
FEATURE [App::DocumentObjectGroupPython] G4_CELLULOSE_BUTYRATE  # scripted group (container) (typed FeaturePython)
  Dunit = g/cm3
  Dvalue = 1.2
  Group = -> [H_element022,C_element026,O_element027]
  conduct = 2
  density = 1
  expand = 3
  formula = G4_CELLULOSE_BUTYRATE
  name = G4_CELLULOSE_BUTYRATE
  specific = 4
FEATURE [App::DocumentObjectGroupPython] H_element023  label="H_element : 0.029"  # scripted group (container) (typed FeaturePython)
  n = 0.029216
FEATURE [App::DocumentObjectGroupPython] C_element027  label="C_element : 0.271"  # scripted group (container) (typed FeaturePython)
  n = 0.271296
FEATURE [App::DocumentObjectGroupPython] N_element013  label="N_element : 0.121"  # scripted group (container) (typed FeaturePython)
  n = 0.121276
FEATURE [App::DocumentObjectGroupPython] O_element028  label="O_element : 0.578"  # scripted group (container) (typed FeaturePython)
  n = 0.578212
FEATURE [App::DocumentObjectGroupPython] G4_CELLULOSE_NITRATE  # scripted group (container) (typed FeaturePython)
  Dunit = g/cm3
  Dvalue = 1.49
  Group = -> [H_element023,C_element027,N_element013,O_element028]
  conduct = 2
  density = 1
  expand = 3
  formula = G4_CELLULOSE_NITRATE
  name = G4_CELLULOSE_NITRATE
  specific = 4
FEATURE [App::DocumentObjectGroupPython] H_element024  label="H_element : 0.108"  # scripted group (container) (typed FeaturePython)
  n = 0.107596
FEATURE [App::DocumentObjectGroupPython] N_element014  label="N_element : 0.001"  # scripted group (container) (typed FeaturePython)
  n = 0.0008
FEATURE [App::DocumentObjectGroupPython] O_element029  label="O_element : 0.875"  # scripted group (container) (typed FeaturePython)
  n = 0.874976
FEATURE [App::DocumentObjectGroupPython] S_element008  label="S_element : 0.015"  # scripted group (container) (typed FeaturePython)
  n = 0.014627
FEATURE [App::DocumentObjectGroupPython] Ce_element001  label="Ce_element : 0.002"  # scripted group (container) (typed FeaturePython)
  n = 0.002001
FEATURE [App::DocumentObjectGroupPython] G4_CERIC_SULFATE  # scripted group (container) (typed FeaturePython)
  Dunit = g/cm3
  Dvalue = 1.03
  Group = -> [H_element024,N_element014,O_element029,S_element008,Ce_element001]
  conduct = 2
  density = 1
  expand = 3
  formula = G4_CERIC_SULFATE
  name = G4_CERIC_SULFATE
  specific = 4
FEATURE [App::DocumentObjectGroupPython] Cs_element001  label="Cs_element : 1"  # scripted group (container) (typed FeaturePython)
  n = 1
  ref = Cs_element
FEATURE [App::DocumentObjectGroupPython] F_element006  label="F_element : 1"  # scripted group (container) (typed FeaturePython)
  n = 1
  ref = F_element
FEATURE [App::DocumentObjectGroupPython] G4_CESIUM_FLUORIDE  # scripted group (container) (typed FeaturePython)
  Dunit = g/cm3
  Dvalue = 4.115
  Group = -> [Cs_element001,F_element006]
  conduct = 2
  density = 1
  expand = 3
  formula = G4_CESIUM_FLUORIDE
  name = G4_CESIUM_FLUORIDE
  specific = 4
FEATURE [App::DocumentObjectGroupPython] Cs_element002  label="Cs_element : 002"  # scripted group (container) (typed FeaturePython)
  n = 1
  ref = Cs_element
FEATURE [App::DocumentObjectGroupPython] I_element001  label="I_element : 1"  # scripted group (container) (typed FeaturePython)
  n = 1
  ref = I_element
FEATURE [App::DocumentObjectGroupPython] G4_CESIUM_IODIDE  # scripted group (container) (typed FeaturePython)
  Dunit = g/cm3
  Dvalue = 4.51
  Group = -> [Cs_element002,I_element001]
  conduct = 2
  density = 1
  expand = 3
  formula = G4_CESIUM_IODIDE
  name = G4_CESIUM_IODIDE
  specific = 4
FEATURE [App::DocumentObjectGroupPython] C_element028  label="C_element : 013"  # scripted group (container) (typed FeaturePython)
  n = 6
  ref = C_element
FEATURE [App::DocumentObjectGroupPython] H_element025  label="H_element : 013"  # scripted group (container) (typed FeaturePython)
  n = 5
  ref = H_element
FEATURE [App::DocumentObjectGroupPython] Cl_element005  label="Cl_element : 1"  # scripted group (container) (typed FeaturePython)
  n = 1
  ref = Cl_element
FEATURE [App::DocumentObjectGroupPython] G4_CHLOROBENZENE  # scripted group (container) (typed FeaturePython)
  Dunit = g/cm3
  Dvalue = 1.1058
  Group = -> [C_element028,H_element025,Cl_element005]
  conduct = 2
  density = 1
  expand = 3
  formula = G4_CHLOROBENZENE
  name = G4_CHLOROBENZENE
  specific = 4
FEATURE [App::DocumentObjectGroupPython] C_element029  label="C_element : 014"  # scripted group (container) (typed FeaturePython)
  n = 1
  ref = C_element
FEATURE [App::DocumentObjectGroupPython] H_element026  label="H_element : 1"  # scripted group (container) (typed FeaturePython)
  n = 1
  ref = H_element
FEATURE [App::DocumentObjectGroupPython] Cl_element006  label="Cl_element : 3"  # scripted group (container) (typed FeaturePython)
  n = 3
  ref = Cl_element
FEATURE [App::DocumentObjectGroupPython] G4_CHLOROFORM  # scripted group (container) (typed FeaturePython)
  Dunit = g/cm3
  Dvalue = 1.4832
  Group = -> [C_element029,H_element026,Cl_element006]
  conduct = 2
  density = 1
  expand = 3
  formula = G4_CHLOROFORM
  name = G4_CHLOROFORM
  specific = 4
FEATURE [App::DocumentObjectGroupPython] H_element027  label="H_element : 0.010"  # scripted group (container) (typed FeaturePython)
  n = 0.01
FEATURE [App::DocumentObjectGroupPython] C_element030  label="C_element : 0.001"  # scripted group (container) (typed FeaturePython)
  n = 0.001
FEATURE [App::DocumentObjectGroupPython] O_element030  label="O_element : 0.529"  # scripted group (container) (typed FeaturePython)
  n = 0.529107
FEATURE [App::DocumentObjectGroupPython] Na_element005  label="Na_element : 0.016"  # scripted group (container) (typed FeaturePython)
  n = 0.016
FEATURE [App::DocumentObjectGroupPython] Mg_element003  label="Mg_element : 0.004"  # scripted group (container) (typed FeaturePython)
  n = 0.002
FEATURE [App::DocumentObjectGroupPython] Al_element002  label="Al_element : 0.034"  # scripted group (container) (typed FeaturePython)
  n = 0.033872
FEATURE [App::DocumentObjectGroupPython] Si_element002  label="Si_element : 0.337"  # scripted group (container) (typed FeaturePython)
  n = 0.337021
FEATURE [App::DocumentObjectGroupPython] K_element003  label="K_element : 0.013"  # scripted group (container) (typed FeaturePython)
  n = 0.013
FEATURE [App::DocumentObjectGroupPython] Ca_element010  label="Ca_element : 0.044"  # scripted group (container) (typed FeaturePython)
  n = 0.044
FEATURE [App::DocumentObjectGroupPython] Fe_element002  label="Fe_element : 0.014"  # scripted group (container) (typed FeaturePython)
  n = 0.014
FEATURE [App::DocumentObjectGroupPython] G4_CONCRETE  # scripted group (container) (typed FeaturePython)
  Dunit = g/cm3
  Dvalue = 2.3
  Group = -> [H_element027,C_element030,O_element030,Na_element005,Mg_element003,Al_element002,Si_element002,K_element003,Ca_element010,Fe_element002]
  conduct = 2
  density = 1
  expand = 3
  formula = G4_CONCRETE
  name = G4_CONCRETE
  specific = 4
FEATURE [App::DocumentObjectGroupPython] C_element031  label="C_element : 015"  # scripted group (container) (typed FeaturePython)
  n = 6
  ref = C_element
FEATURE [App::DocumentObjectGroupPython] H_element028  label="H_element : 12"  # scripted group (container) (typed FeaturePython)
  n = 12
  ref = H_element
FEATURE [App::DocumentObjectGroupPython] G4_CYCLOHEXANE  # scripted group (container) (typed FeaturePython)
  Dunit = g/cm3
  Dvalue = 0.779
  Group = -> [C_element031,H_element028]
  conduct = 2
  density = 1
  expand = 3
  formula = G4_CYCLOHEXANE
  name = G4_CYCLOHEXANE
  specific = 4
FEATURE [App::DocumentObjectGroupPython] C_element032  label="C_element : 016"  # scripted group (container) (typed FeaturePython)
  n = 6
  ref = C_element
FEATURE [App::DocumentObjectGroupPython] H_element029  label="H_element : 4"  # scripted group (container) (typed FeaturePython)
  n = 4
  ref = H_element
FEATURE [App::DocumentObjectGroupPython] Cl_element007  label="Cl_element : 2"  # scripted group (container) (typed FeaturePython)
  n = 2
  ref = Cl_element
FEATURE [App::DocumentObjectGroupPython] G4_1_2_DICHLOROBENZENE  label="G4_1.2-DICHLOROBENZENE"  # scripted group (container) (typed FeaturePython)
  Dunit = g/cm3
  Dvalue = 1.3048
  Group = -> [C_element032,H_element029,Cl_element007]
  conduct = 2
  density = 1
  expand = 3
  formula = G4_1.2-DICHLOROBENZENE
  name = G4_1.2-DICHLOROBENZENE
  specific = 4
FEATURE [App::DocumentObjectGroupPython] C_element033  label="C_element : 017"  # scripted group (container) (typed FeaturePython)
  n = 4
  ref = C_element
FEATURE [App::DocumentObjectGroupPython] H_element030  label="H_element : 8"  # scripted group (container) (typed FeaturePython)
  n = 8
  ref = H_element
FEATURE [App::DocumentObjectGroupPython] O_element031  label="O_element : 014"  # scripted group (container) (typed FeaturePython)
  n = 1
  ref = O_element
FEATURE [App::DocumentObjectGroupPython] Cl_element008  label="Cl_element : 005"  # scripted group (container) (typed FeaturePython)
  n = 2
  ref = Cl_element
FEATURE [App::DocumentObjectGroupPython] G4_DICHLORODIETHYL_ETHER  # scripted group (container) (typed FeaturePython)
  Dunit = g/cm3
  Dvalue = 1.2199
  Group = -> [C_element033,H_element030,O_element031,Cl_element008]
  conduct = 2
  density = 1
  expand = 3
  formula = G4_DICHLORODIETHYL_ETHER
  name = G4_DICHLORODIETHYL_ETHER
  specific = 4
FEATURE [App::DocumentObjectGroupPython] C_element034  label="C_element : 018"  # scripted group (container) (typed FeaturePython)
  n = 2
  ref = C_element
FEATURE [App::DocumentObjectGroupPython] H_element031  label="H_element : 014"  # scripted group (container) (typed FeaturePython)
  n = 4
  ref = H_element
FEATURE [App::DocumentObjectGroupPython] Cl_element009  label="Cl_element : 006"  # scripted group (container) (typed FeaturePython)
  n = 2
  ref = Cl_element
FEATURE [App::DocumentObjectGroupPython] G4_1_2_DICHLOROETHANE  label="G4_1.2-DICHLOROETHANE"  # scripted group (container) (typed FeaturePython)
  Dunit = g/cm3
  Dvalue = 1.2351
  Group = -> [C_element034,H_element031,Cl_element009]
  conduct = 2
  density = 1
  expand = 3
  formula = G4_1.2-DICHLOROETHANE
  name = G4_1.2-DICHLOROETHANE
  specific = 4
FEATURE [App::DocumentObjectGroupPython] C_element035  label="C_element : 019"  # scripted group (container) (typed FeaturePython)
  n = 4
  ref = C_element
FEATURE [App::DocumentObjectGroupPython] H_element032  label="H_element : 015"  # scripted group (container) (typed FeaturePython)
  n = 10
  ref = H_element
FEATURE [App::DocumentObjectGroupPython] O_element032  label="O_element : 015"  # scripted group (container) (typed FeaturePython)
  n = 1
  ref = O_element
FEATURE [App::DocumentObjectGroupPython] G4_DIETHYL_ETHER  # scripted group (container) (typed FeaturePython)
  Dunit = g/cm3
  Dvalue = 0.71378
  Group = -> [C_element035,H_element032,O_element032]
  conduct = 2
  density = 1
  expand = 3
  formula = G4_DIETHYL_ETHER
  name = G4_DIETHYL_ETHER
  specific = 4
FEATURE [App::DocumentObjectGroupPython] C_element036  label="C_element : 020"  # scripted group (container) (typed FeaturePython)
  n = 3
  ref = C_element
FEATURE [App::DocumentObjectGroupPython] H_element033  label="H_element : 016"  # scripted group (container) (typed FeaturePython)
  n = 7
  ref = H_element
FEATURE [App::DocumentObjectGroupPython] N_element015  label="N_element : 008"  # scripted group (container) (typed FeaturePython)
  n = 1
  ref = N_element
FEATURE [App::DocumentObjectGroupPython] O_element033  label="O_element : 016"  # scripted group (container) (typed FeaturePython)
  n = 1
  ref = O_element
FEATURE [App::DocumentObjectGroupPython] G4_N_N_DIMETHYL_FORMAMIDE  label="G4_N.N-DIMETHYL_FORMAMIDE"  # scripted group (container) (typed FeaturePython)
  Dunit = g/cm3
  Dvalue = 0.9487
  Group = -> [C_element036,H_element033,N_element015,O_element033]
  conduct = 2
  density = 1
  expand = 3
  formula = G4_N.N-DIMETHYL_FORMAMIDE
  name = G4_N.N-DIMETHYL_FORMAMIDE
  specific = 4
FEATURE [App::DocumentObjectGroupPython] C_element037  label="C_element : 021"  # scripted group (container) (typed FeaturePython)
  n = 2
  ref = C_element
FEATURE [App::DocumentObjectGroupPython] H_element034  label="H_element : 017"  # scripted group (container) (typed FeaturePython)
  n = 6
  ref = H_element
FEATURE [App::DocumentObjectGroupPython] O_element034  label="O_element : 017"  # scripted group (container) (typed FeaturePython)
  n = 1
  ref = O_element
FEATURE [App::DocumentObjectGroupPython] S_element009  label="S_element : 003"  # scripted group (container) (typed FeaturePython)
  n = 1
  ref = S_element
FEATURE [App::DocumentObjectGroupPython] G4_DIMETHYL_SULFOXIDE  # scripted group (container) (typed FeaturePython)
  Dunit = g/cm3
  Dvalue = 1.1014
  Group = -> [C_element037,H_element034,O_element034,S_element009]
  conduct = 2
  density = 1
  expand = 3
  formula = G4_DIMETHYL_SULFOXIDE
  name = G4_DIMETHYL_SULFOXIDE
  specific = 4
FEATURE [App::DocumentObjectGroupPython] C_element038  label="C_element : 022"  # scripted group (container) (typed FeaturePython)
  n = 2
  ref = C_element
FEATURE [App::DocumentObjectGroupPython] H_element035  label="H_element : 018"  # scripted group (container) (typed FeaturePython)
  n = 6
  ref = H_element
FEATURE [App::DocumentObjectGroupPython] G4_ETHANE  # scripted group (container) (typed FeaturePython)
  Dunit = g/cm3
  Dvalue = 0.00125324
  Group = -> [C_element038,H_element035]
  conduct = 2
  density = 1
  expand = 3
  formula = G4_ETHANE
  name = G4_ETHANE
  specific = 4
FEATURE [App::DocumentObjectGroupPython] C_element039  label="C_element : 023"  # scripted group (container) (typed FeaturePython)
  n = 2
  ref = C_element
FEATURE [App::DocumentObjectGroupPython] H_element036  label="H_element : 019"  # scripted group (container) (typed FeaturePython)
  n = 6
  ref = H_element
FEATURE [App::DocumentObjectGroupPython] O_element035  label="O_element : 018"  # scripted group (container) (typed FeaturePython)
  n = 1
  ref = O_element
FEATURE [App::DocumentObjectGroupPython] G4_ETHYL_ALCOHOL  # scripted group (container) (typed FeaturePython)
  Dunit = g/cm3
  Dvalue = 0.7893
  Group = -> [C_element039,H_element036,O_element035]
  conduct = 2
  density = 1
  expand = 3
  formula = G4_ETHYL_ALCOHOL
  name = G4_ETHYL_ALCOHOL
  specific = 4
FEATURE [App::DocumentObjectGroupPython] H_element037  label="H_element : 0.090"  # scripted group (container) (typed FeaturePython)
  n = 0.090027
FEATURE [App::DocumentObjectGroupPython] C_element040  label="C_element : 0.585"  # scripted group (container) (typed FeaturePython)
  n = 0.585182
FEATURE [App::DocumentObjectGroupPython] O_element036  label="O_element : 0.325"  # scripted group (container) (typed FeaturePython)
  n = 0.324791
FEATURE [App::DocumentObjectGroupPython] G4_ETHYL_CELLULOSE  # scripted group (container) (typed FeaturePython)
  Dunit = g/cm3
  Dvalue = 1.13
  Group = -> [H_element037,C_element040,O_element036]
  conduct = 2
  density = 1
  expand = 3
  formula = G4_ETHYL_CELLULOSE
  name = G4_ETHYL_CELLULOSE
  specific = 4
FEATURE [App::DocumentObjectGroupPython] C_element041  label="C_element : 024"  # scripted group (container) (typed FeaturePython)
  n = 2
  ref = C_element
FEATURE [App::DocumentObjectGroupPython] H_element038  label="H_element : 020"  # scripted group (container) (typed FeaturePython)
  n = 4
  ref = H_element
FEATURE [App::DocumentObjectGroupPython] G4_ETHYLENE  # scripted group (container) (typed FeaturePython)
  Dunit = g/cm3
  Dvalue = 0.00117497
  Group = -> [C_element041,H_element038]
  conduct = 2
  density = 1
  expand = 3
  formula = G4_ETHYLENE
  name = G4_ETHYLENE
  specific = 4
FEATURE [App::DocumentObjectGroupPython] H_element039  label="H_element : 0.096"  # scripted group (container) (typed FeaturePython)
  n = 0.096
FEATURE [App::DocumentObjectGroupPython] C_element042  label="C_element : 0.195"  # scripted group (container) (typed FeaturePython)
  n = 0.195
FEATURE [App::DocumentObjectGroupPython] N_element016  label="N_element : 0.057"  # scripted group (container) (typed FeaturePython)
  n = 0.057
FEATURE [App::DocumentObjectGroupPython] O_element037  label="O_element : 0.646"  # scripted group (container) (typed FeaturePython)
  n = 0.646
FEATURE [App::DocumentObjectGroupPython] Na_element006  label="Na_element : 0.017"  # scripted group (container) (typed FeaturePython)
  n = 0.001
FEATURE [App::DocumentObjectGroupPython] P_element005  label="P_element : 0.104"  # scripted group (container) (typed FeaturePython)
  n = 0.001
FEATURE [App::DocumentObjectGroupPython] S_element010  label="S_element : 0.016"  # scripted group (container) (typed FeaturePython)
  n = 0.003
FEATURE [App::DocumentObjectGroupPython] Cl_element010  label="Cl_element : 0.005"  # scripted group (container) (typed FeaturePython)
  n = 0.001
FEATURE [App::DocumentObjectGroupPython] G4_EYE_LENS_ICRP  # scripted group (container) (typed FeaturePython)
  Dunit = g/cm3
  Dvalue = 1.07
  Group = -> [H_element039,C_element042,N_element016,O_element037,Na_element006,P_element005,S_element010,Cl_element010]
  conduct = 2
  density = 1
  expand = 3
  formula = G4_EYE_LENS_ICRP
  name = G4_EYE_LENS_ICRP
  specific = 4
FEATURE [App::DocumentObjectGroupPython] Fe_element003  label="Fe_element : 2"  # scripted group (container) (typed FeaturePython)
  n = 2
  ref = Fe_element
FEATURE [App::DocumentObjectGroupPython] O_element038  label="O_element : 019"  # scripted group (container) (typed FeaturePython)
  n = 3
  ref = O_element
FEATURE [App::DocumentObjectGroupPython] G4_FERRIC_OXIDE  # scripted group (container) (typed FeaturePython)
  Dunit = g/cm3
  Dvalue = 5.2
  Group = -> [Fe_element003,O_element038]
  conduct = 2
  density = 1
  expand = 3
  formula = G4_FERRIC_OXIDE
  name = G4_FERRIC_OXIDE
  specific = 4
FEATURE [App::DocumentObjectGroupPython] Fe_element004  label="Fe_element : 1"  # scripted group (container) (typed FeaturePython)
  n = 1
  ref = Fe_element
FEATURE [App::DocumentObjectGroupPython] B_element003  label="B_element : 1"  # scripted group (container) (typed FeaturePython)
  n = 1
  ref = B_element
FEATURE [App::DocumentObjectGroupPython] G4_FERROBORIDE  # scripted group (container) (typed FeaturePython)
  Dunit = g/cm3
  Dvalue = 7.15
  Group = -> [Fe_element004,B_element003]
  conduct = 2
  density = 1
  expand = 3
  formula = G4_FERROBORIDE
  name = G4_FERROBORIDE
  specific = 4
FEATURE [App::DocumentObjectGroupPython] Fe_element005  label="Fe_element : 003"  # scripted group (container) (typed FeaturePython)
  n = 1
  ref = Fe_element
FEATURE [App::DocumentObjectGroupPython] O_element039  label="O_element : 020"  # scripted group (container) (typed FeaturePython)
  n = 1
  ref = O_element
FEATURE [App::DocumentObjectGroupPython] G4_FERROUS_OXIDE  # scripted group (container) (typed FeaturePython)
  Dunit = g/cm3
  Dvalue = 5.7
  Group = -> [Fe_element005,O_element039]
  conduct = 2
  density = 1
  expand = 3
  formula = G4_FERROUS_OXIDE
  name = G4_FERROUS_OXIDE
  specific = 4
FEATURE [App::DocumentObjectGroupPython] H_element040  label="H_element : 0.115"  # scripted group (container) (typed FeaturePython)
  n = 0.108259
FEATURE [App::DocumentObjectGroupPython] N_element017  label="N_element : 0.000"  # scripted group (container) (typed FeaturePython)
  n = 2.7e-05
FEATURE [App::DocumentObjectGroupPython] O_element040  label="O_element : 0.879"  # scripted group (container) (typed FeaturePython)
  n = 0.878636
FEATURE [App::DocumentObjectGroupPython] Na_element007  label="Na_element : 0.000"  # scripted group (container) (typed FeaturePython)
  n = 2.2e-05
FEATURE [App::DocumentObjectGroupPython] S_element011  label="S_element : 0.013"  # scripted group (container) (typed FeaturePython)
  n = 0.012968
FEATURE [App::DocumentObjectGroupPython] Cl_element011  label="Cl_element : 0.000"  # scripted group (container) (typed FeaturePython)
  n = 3.4e-05
FEATURE [App::DocumentObjectGroupPython] Fe_element006  label="Fe_element : 0.000"  # scripted group (container) (typed FeaturePython)
  n = 5.4e-05
FEATURE [App::DocumentObjectGroupPython] G4_FERROUS_SULFATE  # scripted group (container) (typed FeaturePython)
  Dunit = g/cm3
  Dvalue = 1.024
  Group = -> [H_element040,N_element017,O_element040,Na_element007,S_element011,Cl_element011,Fe_element006]
  conduct = 2
  density = 1
  expand = 3
  formula = G4_FERROUS_SULFATE
  name = G4_FERROUS_SULFATE
  specific = 4
FEATURE [App::DocumentObjectGroupPython] C_element043  label="C_element : 0.099"  # scripted group (container) (typed FeaturePython)
  n = 0.099335
FEATURE [App::DocumentObjectGroupPython] F_element007  label="F_element : 0.314"  # scripted group (container) (typed FeaturePython)
  n = 0.314247
FEATURE [App::DocumentObjectGroupPython] Cl_element012  label="Cl_element : 0.586"  # scripted group (container) (typed FeaturePython)
  n = 0.586418
FEATURE [App::DocumentObjectGroupPython] G4_FREON_12  label="G4_FREON-12"  # scripted group (container) (typed FeaturePython)
  Dunit = g/cm3
  Dvalue = 1.12
  Group = -> [C_element043,F_element007,Cl_element012]
  conduct = 2
  density = 1
  expand = 3
  formula = G4_FREON-12
  name = G4_FREON-12
  specific = 4
FEATURE [App::DocumentObjectGroupPython] C_element044  label="C_element : 0.057"  # scripted group (container) (typed FeaturePython)
  n = 0.057245
FEATURE [App::DocumentObjectGroupPython] F_element008  label="F_element : 0.181"  # scripted group (container) (typed FeaturePython)
  n = 0.181096
FEATURE [App::DocumentObjectGroupPython] Br_element001  label="Br_element : 0.762"  # scripted group (container) (typed FeaturePython)
  n = 0.761659
FEATURE [App::DocumentObjectGroupPython] G4_FREON_12B2  label="G4_FREON-12B2"  # scripted group (container) (typed FeaturePython)
  Dunit = g/cm3
  Dvalue = 1.8
  Group = -> [C_element044,F_element008,Br_element001]
  conduct = 2
  density = 1
  expand = 3
  formula = G4_FREON-12B2
  name = G4_FREON-12B2
  specific = 4
FEATURE [App::DocumentObjectGroupPython] C_element045  label="C_element : 0.115"  # scripted group (container) (typed FeaturePython)
  n = 0.114983
FEATURE [App::DocumentObjectGroupPython] F_element009  label="F_element : 0.546"  # scripted group (container) (typed FeaturePython)
  n = 0.545621
FEATURE [App::DocumentObjectGroupPython] Cl_element013  label="Cl_element : 0.339"  # scripted group (container) (typed FeaturePython)
  n = 0.339396
FEATURE [App::DocumentObjectGroupPython] G4_FREON_13  label="G4_FREON-13"  # scripted group (container) (typed FeaturePython)
  Dunit = g/cm3
  Dvalue = 0.95
  Group = -> [C_element045,F_element009,Cl_element013]
  conduct = 2
  density = 1
  expand = 3
  formula = G4_FREON-13
  name = G4_FREON-13
  specific = 4
FEATURE [App::DocumentObjectGroupPython] C_element046  label="C_element : 025"  # scripted group (container) (typed FeaturePython)
  n = 1
  ref = C_element
FEATURE [App::DocumentObjectGroupPython] F_element010  label="F_element : 3"  # scripted group (container) (typed FeaturePython)
  n = 3
  ref = F_element
FEATURE [App::DocumentObjectGroupPython] Br_element002  label="Br_element : 1"  # scripted group (container) (typed FeaturePython)
  n = 1
  ref = Br_element
FEATURE [App::DocumentObjectGroupPython] G4_FREON_13B1  label="G4_FREON-13B1"  # scripted group (container) (typed FeaturePython)
  Dunit = g/cm3
  Dvalue = 1.5
  Group = -> [C_element046,F_element010,Br_element002]
  conduct = 2
  density = 1
  expand = 3
  formula = G4_FREON-13B1
  name = G4_FREON-13B1
  specific = 4
FEATURE [App::DocumentObjectGroupPython] C_element047  label="C_element : 0.061"  # scripted group (container) (typed FeaturePython)
  n = 0.061309
FEATURE [App::DocumentObjectGroupPython] F_element011  label="F_element : 0.291"  # scripted group (container) (typed FeaturePython)
  n = 0.290924
FEATURE [App::DocumentObjectGroupPython] I_element002  label="I_element : 0.648"  # scripted group (container) (typed FeaturePython)
  n = 0.647767
FEATURE [App::DocumentObjectGroupPython] G4_FREON_13I1  label="G4_FREON-13I1"  # scripted group (container) (typed FeaturePython)
  Dunit = g/cm3
  Dvalue = 1.8
  Group = -> [C_element047,F_element011,I_element002]
  conduct = 2
  density = 1
  expand = 3
  formula = G4_FREON-13I1
  name = G4_FREON-13I1
  specific = 4
FEATURE [App::DocumentObjectGroupPython] Gd_element001  label="Gd_element : 2"  # scripted group (container) (typed FeaturePython)
  n = 2
  ref = Gd_element
FEATURE [App::DocumentObjectGroupPython] O_element041  label="O_element : 021"  # scripted group (container) (typed FeaturePython)
  n = 2
  ref = O_element
FEATURE [App::DocumentObjectGroupPython] S_element012  label="S_element : 004"  # scripted group (container) (typed FeaturePython)
  n = 1
  ref = S_element
FEATURE [App::DocumentObjectGroupPython] G4_GADOLINIUM_OXYSULFIDE  # scripted group (container) (typed FeaturePython)
  Dunit = g/cm3
  Dvalue = 7.44
  Group = -> [Gd_element001,O_element041,S_element012]
  conduct = 2
  density = 1
  expand = 3
  formula = G4_GADOLINIUM_OXYSULFIDE
  name = G4_GADOLINIUM_OXYSULFIDE
  specific = 4
FEATURE [App::DocumentObjectGroupPython] Ga_element001  label="Ga_element : 1"  # scripted group (container) (typed FeaturePython)
  n = 1
  ref = Ga_element
FEATURE [App::DocumentObjectGroupPython] As_element001  label="As_element : 1"  # scripted group (container) (typed FeaturePython)
  n = 1
  ref = As_element
FEATURE [App::DocumentObjectGroupPython] G4_GALLIUM_ARSENIDE  # scripted group (container) (typed FeaturePython)
  Dunit = g/cm3
  Dvalue = 5.31
  Group = -> [Ga_element001,As_element001]
  conduct = 2
  density = 1
  expand = 3
  formula = G4_GALLIUM_ARSENIDE
  name = G4_GALLIUM_ARSENIDE
  specific = 4
FEATURE [App::DocumentObjectGroupPython] H_element041  label="H_element : 0.081"  # scripted group (container) (typed FeaturePython)
  n = 0.08118
FEATURE [App::DocumentObjectGroupPython] C_element048  label="C_element : 0.416"  # scripted group (container) (typed FeaturePython)
  n = 0.41606
FEATURE [App::DocumentObjectGroupPython] N_element018  label="N_element : 0.111"  # scripted group (container) (typed FeaturePython)
  n = 0.11124
FEATURE [App::DocumentObjectGroupPython] O_element042  label="O_element : 0.381"  # scripted group (container) (typed FeaturePython)
  n = 0.38064
FEATURE [App::DocumentObjectGroupPython] S_element013  label="S_element : 0.011"  # scripted group (container) (typed FeaturePython)
  n = 0.01088
FEATURE [App::DocumentObjectGroupPython] G4_GEL_PHOTO_EMULSION  # scripted group (container) (typed FeaturePython)
  Dunit = g/cm3
  Dvalue = 1.2914
  Group = -> [H_element041,C_element048,N_element018,O_element042,S_element013]
  conduct = 2
  density = 1
  expand = 3
  formula = G4_GEL_PHOTO_EMULSION
  name = G4_GEL_PHOTO_EMULSION
  specific = 4
FEATURE [App::DocumentObjectGroupPython] B_element004  label="B_element : 0.040"  # scripted group (container) (typed FeaturePython)
  n = 0.0400639
FEATURE [App::DocumentObjectGroupPython] O_element043  label="O_element : 0.540"  # scripted group (container) (typed FeaturePython)
  n = 0.539561
FEATURE [App::DocumentObjectGroupPython] Na_element008  label="Na_element : 0.028"  # scripted group (container) (typed FeaturePython)
  n = 0.0281909
FEATURE [App::DocumentObjectGroupPython] Al_element003  label="Al_element : 0.012"  # scripted group (container) (typed FeaturePython)
  n = 0.011644
FEATURE [App::DocumentObjectGroupPython] Si_element003  label="Si_element : 0.377"  # scripted group (container) (typed FeaturePython)
  n = 0.377219
FEATURE [App::DocumentObjectGroupPython] K_element004  label="K_element : 0.014"  # scripted group (container) (typed FeaturePython)
  n = 0.00332099
FEATURE [App::DocumentObjectGroupPython] G4_Pyrex_Glass  # scripted group (container) (typed FeaturePython)
  Dunit = g/cm3
  Dvalue = 2.23
  Group = -> [B_element004,O_element043,Na_element008,Al_element003,Si_element003,K_element004]
  conduct = 2
  density = 1
  expand = 3
  formula = G4_Pyrex_Glass
  name = G4_Pyrex_Glass
  specific = 4
FEATURE [App::DocumentObjectGroupPython] O_element044  label="O_element : 0.156"  # scripted group (container) (typed FeaturePython)
  n = 0.156453
FEATURE [App::DocumentObjectGroupPython] Si_element004  label="Si_element : 0.081"  # scripted group (container) (typed FeaturePython)
  n = 0.080866
FEATURE [App::DocumentObjectGroupPython] Ti_element001  label="Ti_element : 0.008"  # scripted group (container) (typed FeaturePython)
  n = 0.008092
FEATURE [App::DocumentObjectGroupPython] As_element002  label="As_element : 0.003"  # scripted group (container) (typed FeaturePython)
  n = 0.002651
FEATURE [App::DocumentObjectGroupPython] Pb_element001  label="Pb_element : 0.752"  # scripted group (container) (typed FeaturePython)
  n = 0.751938
FEATURE [App::DocumentObjectGroupPython] G4_GLASS_LEAD  # scripted group (container) (typed FeaturePython)
  Dunit = g/cm3
  Dvalue = 6.22
  Group = -> [O_element044,Si_element004,Ti_element001,As_element002,Pb_element001]
  conduct = 2
  density = 1
  expand = 3
  formula = G4_GLASS_LEAD
  name = G4_GLASS_LEAD
  specific = 4
FEATURE [App::DocumentObjectGroupPython] O_element045  label="O_element : 0.460"  # scripted group (container) (typed FeaturePython)
  n = 0.4598
FEATURE [App::DocumentObjectGroupPython] Na_element009  label="Na_element : 0.096"  # scripted group (container) (typed FeaturePython)
  n = 0.0964411
FEATURE [App::DocumentObjectGroupPython] Si_element005  label="Si_element : 0.378"  # scripted group (container) (typed FeaturePython)
  n = 0.336553
FEATURE [App::DocumentObjectGroupPython] Ca_element011  label="Ca_element : 0.107"  # scripted group (container) (typed FeaturePython)
  n = 0.107205
FEATURE [App::DocumentObjectGroupPython] G4_GLASS_PLATE  # scripted group (container) (typed FeaturePython)
  Dunit = g/cm3
  Dvalue = 2.4
  Group = -> [O_element045,Na_element009,Si_element005,Ca_element011]
  conduct = 2
  density = 1
  expand = 3
  formula = G4_GLASS_PLATE
  name = G4_GLASS_PLATE
  specific = 4
FEATURE [App::DocumentObjectGroupPython] C_element049  label="C_element : 026"  # scripted group (container) (typed FeaturePython)
  n = 5
  ref = C_element
FEATURE [App::DocumentObjectGroupPython] H_element042  label="H_element : 021"  # scripted group (container) (typed FeaturePython)
  n = 10
  ref = H_element
FEATURE [App::DocumentObjectGroupPython] N_element019  label="N_element : 2"  # scripted group (container) (typed FeaturePython)
  n = 2
  ref = N_element
FEATURE [App::DocumentObjectGroupPython] O_element046  label="O_element : 022"  # scripted group (container) (typed FeaturePython)
  n = 3
  ref = O_element
FEATURE [App::DocumentObjectGroupPython] G4_GLUTAMINE  # scripted group (container) (typed FeaturePython)
  Dunit = g/cm3
  Dvalue = 1.46
  Group = -> [C_element049,H_element042,N_element019,O_element046]
  conduct = 2
  density = 1
  expand = 3
  formula = G4_GLUTAMINE
  name = G4_GLUTAMINE
  specific = 4
FEATURE [App::DocumentObjectGroupPython] C_element050  label="C_element : 027"  # scripted group (container) (typed FeaturePython)
  n = 3
  ref = C_element
FEATURE [App::DocumentObjectGroupPython] H_element043  label="H_element : 022"  # scripted group (container) (typed FeaturePython)
  n = 8
  ref = H_element
FEATURE [App::DocumentObjectGroupPython] O_element047  label="O_element : 023"  # scripted group (container) (typed FeaturePython)
  n = 3
  ref = O_element
FEATURE [App::DocumentObjectGroupPython] G4_GLYCEROL  # scripted group (container) (typed FeaturePython)
  Dunit = g/cm3
  Dvalue = 1.2613
  Group = -> [C_element050,H_element043,O_element047]
  conduct = 2
  density = 1
  expand = 3
  formula = G4_GLYCEROL
  name = G4_GLYCEROL
  specific = 4
FEATURE [App::DocumentObjectGroupPython] C_element051  label="C_element : 028"  # scripted group (container) (typed FeaturePython)
  n = 5
  ref = C_element
FEATURE [App::DocumentObjectGroupPython] H_element044  label="H_element : 023"  # scripted group (container) (typed FeaturePython)
  n = 5
  ref = H_element
FEATURE [App::DocumentObjectGroupPython] N_element020  label="N_element : 009"  # scripted group (container) (typed FeaturePython)
  n = 5
  ref = N_element
FEATURE [App::DocumentObjectGroupPython] O_element048  label="O_element : 024"  # scripted group (container) (typed FeaturePython)
  n = 1
  ref = O_element
FEATURE [App::DocumentObjectGroupPython] G4_GUANINE  # scripted group (container) (typed FeaturePython)
  Dunit = g/cm3
  Dvalue = 2.2
  Group = -> [C_element051,H_element044,N_element020,O_element048]
  conduct = 2
  density = 1
  expand = 3
  formula = G4_GUANINE
  name = G4_GUANINE
  specific = 4
FEATURE [App::DocumentObjectGroupPython] Ca_element012  label="Ca_element : 006"  # scripted group (container) (typed FeaturePython)
  n = 1
  ref = Ca_element
FEATURE [App::DocumentObjectGroupPython] S_element014  label="S_element : 005"  # scripted group (container) (typed FeaturePython)
  n = 1
  ref = S_element
FEATURE [App::DocumentObjectGroupPython] O_element049  label="O_element : 6"  # scripted group (container) (typed FeaturePython)
  n = 6
  ref = O_element
FEATURE [App::DocumentObjectGroupPython] H_element045  label="H_element : 024"  # scripted group (container) (typed FeaturePython)
  n = 4
  ref = H_element
FEATURE [App::DocumentObjectGroupPython] G4_GYPSUM  # scripted group (container) (typed FeaturePython)
  Dunit = g/cm3
  Dvalue = 2.32
  Group = -> [Ca_element012,S_element014,O_element049,H_element045]
  conduct = 2
  density = 1
  expand = 3
  formula = G4_GYPSUM
  name = G4_GYPSUM
  specific = 4
FEATURE [App::DocumentObjectGroupPython] C_element052  label="C_element : 7"  # scripted group (container) (typed FeaturePython)
  n = 7
  ref = C_element
FEATURE [App::DocumentObjectGroupPython] H_element046  label="H_element : 16"  # scripted group (container) (typed FeaturePython)
  n = 16
  ref = H_element
FEATURE [App::DocumentObjectGroupPython] G4_N_HEPTANE  label="G4_N-HEPTANE"  # scripted group (container) (typed FeaturePython)
  Dunit = g/cm3
  Dvalue = 0.68376
  Group = -> [C_element052,H_element046]
  conduct = 2
  density = 1
  expand = 3
  formula = G4_N-HEPTANE
  name = G4_N-HEPTANE
  specific = 4
FEATURE [App::DocumentObjectGroupPython] C_element053  label="C_element : 029"  # scripted group (container) (typed FeaturePython)
  n = 6
  ref = C_element
FEATURE [App::DocumentObjectGroupPython] H_element047  label="H_element : 14"  # scripted group (container) (typed FeaturePython)
  n = 14
  ref = H_element
FEATURE [App::DocumentObjectGroupPython] G4_N_HEXANE  label="G4_N-HEXANE"  # scripted group (container) (typed FeaturePython)
  Dunit = g/cm3
  Dvalue = 0.6603
  Group = -> [C_element053,H_element047]
  conduct = 2
  density = 1
  expand = 3
  formula = G4_N-HEXANE
  name = G4_N-HEXANE
  specific = 4
FEATURE [App::DocumentObjectGroupPython] C_element054  label="C_element : 22"  # scripted group (container) (typed FeaturePython)
  n = 22
  ref = C_element
FEATURE [App::DocumentObjectGroupPython] H_element048  label="H_element : 025"  # scripted group (container) (typed FeaturePython)
  n = 10
  ref = H_element
FEATURE [App::DocumentObjectGroupPython] N_element021  label="N_element : 010"  # scripted group (container) (typed FeaturePython)
  n = 2
  ref = N_element
FEATURE [App::DocumentObjectGroupPython] O_element050  label="O_element : 025"  # scripted group (container) (typed FeaturePython)
  n = 5
  ref = O_element
FEATURE [App::DocumentObjectGroupPython] G4_KAPTON  # scripted group (container) (typed FeaturePython)
  Dunit = g/cm3
  Dvalue = 1.42
  Group = -> [C_element054,H_element048,N_element021,O_element050]
  conduct = 2
  density = 1
  expand = 3
  formula = G4_KAPTON
  name = G4_KAPTON
  specific = 4
FEATURE [App::DocumentObjectGroupPython] La_element001  label="La_element : 1"  # scripted group (container) (typed FeaturePython)
  n = 1
  ref = La_element
FEATURE [App::DocumentObjectGroupPython] Br_element003  label="Br_element : 002"  # scripted group (container) (typed FeaturePython)
  n = 1
  ref = Br_element
FEATURE [App::DocumentObjectGroupPython] O_element051  label="O_element : 026"  # scripted group (container) (typed FeaturePython)
  n = 1
  ref = O_element
FEATURE [App::DocumentObjectGroupPython] G4_LANTHANUM_OXYBROMIDE  # scripted group (container) (typed FeaturePython)
  Dunit = g/cm3
  Dvalue = 6.28
  Group = -> [La_element001,Br_element003,O_element051]
  conduct = 2
  density = 1
  expand = 3
  formula = G4_LANTHANUM_OXYBROMIDE
  name = G4_LANTHANUM_OXYBROMIDE
  specific = 4
FEATURE [App::DocumentObjectGroupPython] La_element002  label="La_element : 2"  # scripted group (container) (typed FeaturePython)
  n = 2
  ref = La_element
FEATURE [App::DocumentObjectGroupPython] O_element052  label="O_element : 027"  # scripted group (container) (typed FeaturePython)
  n = 2
  ref = O_element
FEATURE [App::DocumentObjectGroupPython] S_element015  label="S_element : 006"  # scripted group (container) (typed FeaturePython)
  n = 1
  ref = S_element
FEATURE [App::DocumentObjectGroupPython] G4_LANTHANUM_OXYSULFIDE  # scripted group (container) (typed FeaturePython)
  Dunit = g/cm3
  Dvalue = 5.86
  Group = -> [La_element002,O_element052,S_element015]
  conduct = 2
  density = 1
  expand = 3
  formula = G4_LANTHANUM_OXYSULFIDE
  name = G4_LANTHANUM_OXYSULFIDE
  specific = 4
FEATURE [App::DocumentObjectGroupPython] O_element053  label="O_element : 0.072"  # scripted group (container) (typed FeaturePython)
  n = 0.071682
FEATURE [App::DocumentObjectGroupPython] Pb_element002  label="Pb_element : 0.928"  # scripted group (container) (typed FeaturePython)
  n = 0.928318
FEATURE [App::DocumentObjectGroupPython] G4_LEAD_OXIDE  # scripted group (container) (typed FeaturePython)
  Dunit = g/cm3
  Dvalue = 9.53
  Group = -> [O_element053,Pb_element002]
  conduct = 2
  density = 1
  expand = 3
  formula = G4_LEAD_OXIDE
  name = G4_LEAD_OXIDE
  specific = 4
FEATURE [App::DocumentObjectGroupPython] Li_element001  label="Li_element : 1"  # scripted group (container) (typed FeaturePython)
  n = 1
  ref = Li_element
FEATURE [App::DocumentObjectGroupPython] N_element022  label="N_element : 011"  # scripted group (container) (typed FeaturePython)
  n = 1
  ref = N_element
FEATURE [App::DocumentObjectGroupPython] H_element049  label="H_element : 026"  # scripted group (container) (typed FeaturePython)
  n = 2
  ref = H_element
FEATURE [App::DocumentObjectGroupPython] G4_LITHIUM_AMIDE  # scripted group (container) (typed FeaturePython)
  Dunit = g/cm3
  Dvalue = 1.178
  Group = -> [Li_element001,N_element022,H_element049]
  conduct = 2
  density = 1
  expand = 3
  formula = G4_LITHIUM_AMIDE
  name = G4_LITHIUM_AMIDE
  specific = 4
FEATURE [App::DocumentObjectGroupPython] Li_element002  label="Li_element : 2"  # scripted group (container) (typed FeaturePython)
  n = 2
  ref = Li_element
FEATURE [App::DocumentObjectGroupPython] C_element055  label="C_element : 030"  # scripted group (container) (typed FeaturePython)
  n = 1
  ref = C_element
FEATURE [App::DocumentObjectGroupPython] O_element054  label="O_element : 028"  # scripted group (container) (typed FeaturePython)
  n = 3
  ref = O_element
FEATURE [App::DocumentObjectGroupPython] G4_LITHIUM_CARBONATE  # scripted group (container) (typed FeaturePython)
  Dunit = g/cm3
  Dvalue = 2.11
  Group = -> [Li_element002,C_element055,O_element054]
  conduct = 2
  density = 1
  expand = 3
  formula = G4_LITHIUM_CARBONATE
  name = G4_LITHIUM_CARBONATE
  specific = 4
FEATURE [App::DocumentObjectGroupPython] Li_element003  label="Li_element : 003"  # scripted group (container) (typed FeaturePython)
  n = 1
  ref = Li_element
FEATURE [App::DocumentObjectGroupPython] F_element012  label="F_element : 004"  # scripted group (container) (typed FeaturePython)
  n = 1
  ref = F_element
FEATURE [App::DocumentObjectGroupPython] G4_LITHIUM_FLUORIDE  # scripted group (container) (typed FeaturePython)
  Dunit = g/cm3
  Dvalue = 2.635
  Group = -> [Li_element003,F_element012]
  conduct = 2
  density = 1
  expand = 3
  formula = G4_LITHIUM_FLUORIDE
  name = G4_LITHIUM_FLUORIDE
  specific = 4
FEATURE [App::DocumentObjectGroupPython] Li_element004  label="Li_element : 004"  # scripted group (container) (typed FeaturePython)
  n = 1
  ref = Li_element
FEATURE [App::DocumentObjectGroupPython] H_element050  label="H_element : 027"  # scripted group (container) (typed FeaturePython)
  n = 1
  ref = H_element
FEATURE [App::DocumentObjectGroupPython] G4_LITHIUM_HYDRIDE  # scripted group (container) (typed FeaturePython)
  Dunit = g/cm3
  Dvalue = 0.82
  Group = -> [Li_element004,H_element050]
  conduct = 2
  density = 1
  expand = 3
  formula = G4_LITHIUM_HYDRIDE
  name = G4_LITHIUM_HYDRIDE
  specific = 4
FEATURE [App::DocumentObjectGroupPython] Li_element005  label="Li_element : 005"  # scripted group (container) (typed FeaturePython)
  n = 1
  ref = Li_element
FEATURE [App::DocumentObjectGroupPython] I_element003  label="I_element : 002"  # scripted group (container) (typed FeaturePython)
  n = 1
  ref = I_element
FEATURE [App::DocumentObjectGroupPython] G4_LITHIUM_IODIDE  # scripted group (container) (typed FeaturePython)
  Dunit = g/cm3
  Dvalue = 3.494
  Group = -> [Li_element005,I_element003]
  conduct = 2
  density = 1
  expand = 3
  formula = G4_LITHIUM_IODIDE
  name = G4_LITHIUM_IODIDE
  specific = 4
FEATURE [App::DocumentObjectGroupPython] Li_element006  label="Li_element : 006"  # scripted group (container) (typed FeaturePython)
  n = 2
  ref = Li_element
FEATURE [App::DocumentObjectGroupPython] O_element055  label="O_element : 029"  # scripted group (container) (typed FeaturePython)
  n = 1
  ref = O_element
FEATURE [App::DocumentObjectGroupPython] G4_LITHIUM_OXIDE  # scripted group (container) (typed FeaturePython)
  Dunit = g/cm3
  Dvalue = 2.013
  Group = -> [Li_element006,O_element055]
  conduct = 2
  density = 1
  expand = 3
  formula = G4_LITHIUM_OXIDE
  name = G4_LITHIUM_OXIDE
  specific = 4
FEATURE [App::DocumentObjectGroupPython] Li_element007  label="Li_element : 007"  # scripted group (container) (typed FeaturePython)
  n = 2
  ref = Li_element
FEATURE [App::DocumentObjectGroupPython] B_element005  label="B_element : 005"  # scripted group (container) (typed FeaturePython)
  n = 4
  ref = B_element
FEATURE [App::DocumentObjectGroupPython] O_element056  label="O_element : 7"  # scripted group (container) (typed FeaturePython)
  n = 7
  ref = O_element
FEATURE [App::DocumentObjectGroupPython] G4_LITHIUM_TETRABORATE  # scripted group (container) (typed FeaturePython)
  Dunit = g/cm3
  Dvalue = 2.44
  Group = -> [Li_element007,B_element005,O_element056]
  conduct = 2
  density = 1
  expand = 3
  formula = G4_LITHIUM_TETRABORATE
  name = G4_LITHIUM_TETRABORATE
  specific = 4
FEATURE [App::DocumentObjectGroupPython] H_element051  label="H_element : 0.105"  # scripted group (container) (typed FeaturePython)
  n = 0.105
FEATURE [App::DocumentObjectGroupPython] C_element056  label="C_element : 0.083"  # scripted group (container) (typed FeaturePython)
  n = 0.083
FEATURE [App::DocumentObjectGroupPython] N_element023  label="N_element : 0.023"  # scripted group (container) (typed FeaturePython)
  n = 0.023
FEATURE [App::DocumentObjectGroupPython] O_element057  label="O_element : 0.779"  # scripted group (container) (typed FeaturePython)
  n = 0.779
FEATURE [App::DocumentObjectGroupPython] Na_element010  label="Na_element : 0.097"  # scripted group (container) (typed FeaturePython)
  n = 0.002
FEATURE [App::DocumentObjectGroupPython] P_element006  label="P_element : 0.105"  # scripted group (container) (typed FeaturePython)
  n = 0.001
FEATURE [App::DocumentObjectGroupPython] S_element016  label="S_element : 0.017"  # scripted group (container) (typed FeaturePython)
  n = 0.002
FEATURE [App::DocumentObjectGroupPython] Cl_element014  label="Cl_element : 0.587"  # scripted group (container) (typed FeaturePython)
  n = 0.003
FEATURE [App::DocumentObjectGroupPython] K_element005  label="K_element : 0.015"  # scripted group (container) (typed FeaturePython)
  n = 0.002
FEATURE [App::DocumentObjectGroupPython] G4_LUNG_ICRP  # scripted group (container) (typed FeaturePython)
  Dunit = g/cm3
  Dvalue = 1.04
  Group = -> [H_element051,C_element056,N_element023,O_element057,Na_element010,P_element006,S_element016,Cl_element014,K_element005]
  conduct = 2
  density = 1
  expand = 3
  formula = G4_LUNG_ICRP
  name = G4_LUNG_ICRP
  specific = 4
FEATURE [App::DocumentObjectGroupPython] H_element052  label="H_element : 0.116"  # scripted group (container) (typed FeaturePython)
  n = 0.114318
FEATURE [App::DocumentObjectGroupPython] C_element057  label="C_element : 0.656"  # scripted group (container) (typed FeaturePython)
  n = 0.655824
FEATURE [App::DocumentObjectGroupPython] O_element058  label="O_element : 0.092"  # scripted group (container) (typed FeaturePython)
  n = 0.0921831
FEATURE [App::DocumentObjectGroupPython] Mg_element004  label="Mg_element : 0.135"  # scripted group (container) (typed FeaturePython)
  n = 0.134792
FEATURE [App::DocumentObjectGroupPython] Ca_element013  label="Ca_element : 0.003"  # scripted group (container) (typed FeaturePython)
  n = 0.002883
FEATURE [App::DocumentObjectGroupPython] G4_M3_WAX  # scripted group (container) (typed FeaturePython)
  Dunit = g/cm3
  Dvalue = 1.05
  Group = -> [H_element052,C_element057,O_element058,Mg_element004,Ca_element013]
  conduct = 2
  density = 1
  expand = 3
  formula = G4_M3_WAX
  name = G4_M3_WAX
  specific = 4
FEATURE [App::DocumentObjectGroupPython] Mg_element005  label="Mg_element : 1"  # scripted group (container) (typed FeaturePython)
  n = 1
  ref = Mg_element
FEATURE [App::DocumentObjectGroupPython] C_element058  label="C_element : 031"  # scripted group (container) (typed FeaturePython)
  n = 1
  ref = C_element
FEATURE [App::DocumentObjectGroupPython] O_element059  label="O_element : 030"  # scripted group (container) (typed FeaturePython)
  n = 3
  ref = O_element
FEATURE [App::DocumentObjectGroupPython] G4_MAGNESIUM_CARBONATE  # scripted group (container) (typed FeaturePython)
  Dunit = g/cm3
  Dvalue = 2.958
  Group = -> [Mg_element005,C_element058,O_element059]
  conduct = 2
  density = 1
  expand = 3
  formula = G4_MAGNESIUM_CARBONATE
  name = G4_MAGNESIUM_CARBONATE
  specific = 4
FEATURE [App::DocumentObjectGroupPython] Mg_element006  label="Mg_element : 002"  # scripted group (container) (typed FeaturePython)
  n = 1
  ref = Mg_element
FEATURE [App::DocumentObjectGroupPython] F_element013  label="F_element : 005"  # scripted group (container) (typed FeaturePython)
  n = 2
  ref = F_element
FEATURE [App::DocumentObjectGroupPython] G4_MAGNESIUM_FLUORIDE  # scripted group (container) (typed FeaturePython)
  Dunit = g/cm3
  Dvalue = 3
  Group = -> [Mg_element006,F_element013]
  conduct = 2
  density = 1
  expand = 3
  formula = G4_MAGNESIUM_FLUORIDE
  name = G4_MAGNESIUM_FLUORIDE
  specific = 4
FEATURE [App::DocumentObjectGroupPython] Mg_element007  label="Mg_element : 003"  # scripted group (container) (typed FeaturePython)
  n = 1
  ref = Mg_element
FEATURE [App::DocumentObjectGroupPython] O_element060  label="O_element : 031"  # scripted group (container) (typed FeaturePython)
  n = 1
  ref = O_element
FEATURE [App::DocumentObjectGroupPython] G4_MAGNESIUM_OXIDE  # scripted group (container) (typed FeaturePython)
  Dunit = g/cm3
  Dvalue = 3.58
  Group = -> [Mg_element007,O_element060]
  conduct = 2
  density = 1
  expand = 3
  formula = G4_MAGNESIUM_OXIDE
  name = G4_MAGNESIUM_OXIDE
  specific = 4
FEATURE [App::DocumentObjectGroupPython] Mg_element008  label="Mg_element : 004"  # scripted group (container) (typed FeaturePython)
  n = 1
  ref = Mg_element
FEATURE [App::DocumentObjectGroupPython] B_element006  label="B_element : 006"  # scripted group (container) (typed FeaturePython)
  n = 4
  ref = B_element
FEATURE [App::DocumentObjectGroupPython] O_element061  label="O_element : 032"  # scripted group (container) (typed FeaturePython)
  n = 7
  ref = O_element
FEATURE [App::DocumentObjectGroupPython] G4_MAGNESIUM_TETRABORATE  # scripted group (container) (typed FeaturePython)
  Dunit = g/cm3
  Dvalue = 2.53
  Group = -> [Mg_element008,B_element006,O_element061]
  conduct = 2
  density = 1
  expand = 3
  formula = G4_MAGNESIUM_TETRABORATE
  name = G4_MAGNESIUM_TETRABORATE
  specific = 4
FEATURE [App::DocumentObjectGroupPython] Hg_element001  label="Hg_element : 1"  # scripted group (container) (typed FeaturePython)
  n = 1
  ref = Hg_element
FEATURE [App::DocumentObjectGroupPython] I_element004  label="I_element : 2"  # scripted group (container) (typed FeaturePython)
  n = 2
  ref = I_element
FEATURE [App::DocumentObjectGroupPython] G4_MERCURIC_IODIDE  # scripted group (container) (typed FeaturePython)
  Dunit = g/cm3
  Dvalue = 6.36
  Group = -> [Hg_element001,I_element004]
  conduct = 2
  density = 1
  expand = 3
  formula = G4_MERCURIC_IODIDE
  name = G4_MERCURIC_IODIDE
  specific = 4
FEATURE [App::DocumentObjectGroupPython] C_element059  label="C_element : 032"  # scripted group (container) (typed FeaturePython)
  n = 1
  ref = C_element
FEATURE [App::DocumentObjectGroupPython] H_element053  label="H_element : 028"  # scripted group (container) (typed FeaturePython)
  n = 4
  ref = H_element
FEATURE [App::DocumentObjectGroupPython] G4_METHANE  # scripted group (container) (typed FeaturePython)
  Dunit = g/cm3
  Dvalue = 0.000667151
  Group = -> [C_element059,H_element053]
  conduct = 2
  density = 1
  expand = 3
  formula = G4_METHANE
  name = G4_METHANE
  specific = 4
FEATURE [App::DocumentObjectGroupPython] C_element060  label="C_element : 033"  # scripted group (container) (typed FeaturePython)
  n = 1
  ref = C_element
FEATURE [App::DocumentObjectGroupPython] H_element054  label="H_element : 029"  # scripted group (container) (typed FeaturePython)
  n = 4
  ref = H_element
FEATURE [App::DocumentObjectGroupPython] O_element062  label="O_element : 033"  # scripted group (container) (typed FeaturePython)
  n = 1
  ref = O_element
FEATURE [App::DocumentObjectGroupPython] G4_METHANOL  # scripted group (container) (typed FeaturePython)
  Dunit = g/cm3
  Dvalue = 0.7914
  Group = -> [C_element060,H_element054,O_element062]
  conduct = 2
  density = 1
  expand = 3
  formula = G4_METHANOL
  name = G4_METHANOL
  specific = 4
FEATURE [App::DocumentObjectGroupPython] H_element055  label="H_element : 0.134"  # scripted group (container) (typed FeaturePython)
  n = 0.13404
FEATURE [App::DocumentObjectGroupPython] C_element061  label="C_element : 0.778"  # scripted group (container) (typed FeaturePython)
  n = 0.77796
FEATURE [App::DocumentObjectGroupPython] O_element063  label="O_element : 0.035"  # scripted group (container) (typed FeaturePython)
  n = 0.03502
FEATURE [App::DocumentObjectGroupPython] Mg_element009  label="Mg_element : 0.039"  # scripted group (container) (typed FeaturePython)
  n = 0.038594
FEATURE [App::DocumentObjectGroupPython] Ti_element002  label="Ti_element : 0.014"  # scripted group (container) (typed FeaturePython)
  n = 0.014386
FEATURE [App::DocumentObjectGroupPython] G4_MIX_D_WAX  # scripted group (container) (typed FeaturePython)
  Dunit = g/cm3
  Dvalue = 0.99
  Group = -> [H_element055,C_element061,O_element063,Mg_element009,Ti_element002]
  conduct = 2
  density = 1
  expand = 3
  formula = G4_MIX_D_WAX
  name = G4_MIX_D_WAX
  specific = 4
FEATURE [App::DocumentObjectGroupPython] H_element056  label="H_element : 0.135"  # scripted group (container) (typed FeaturePython)
  n = 0.081192
FEATURE [App::DocumentObjectGroupPython] C_element062  label="C_element : 0.583"  # scripted group (container) (typed FeaturePython)
  n = 0.583442
FEATURE [App::DocumentObjectGroupPython] N_element024  label="N_element : 0.018"  # scripted group (container) (typed FeaturePython)
  n = 0.017798
FEATURE [App::DocumentObjectGroupPython] O_element064  label="O_element : 0.186"  # scripted group (container) (typed FeaturePython)
  n = 0.186381
FEATURE [App::DocumentObjectGroupPython] Mg_element010  label="Mg_element : 0.130"  # scripted group (container) (typed FeaturePython)
  n = 0.130287
FEATURE [App::DocumentObjectGroupPython] Cl_element015  label="Cl_element : 0.588"  # scripted group (container) (typed FeaturePython)
  n = 0.0009
FEATURE [App::DocumentObjectGroupPython] G4_MS20_TISSUE  # scripted group (container) (typed FeaturePython)
  Dunit = g/cm3
  Dvalue = 1
  Group = -> [H_element056,C_element062,N_element024,O_element064,Mg_element010,Cl_element015]
  conduct = 2
  density = 1
  expand = 3
  formula = G4_MS20_TISSUE
  name = G4_MS20_TISSUE
  specific = 4
FEATURE [App::DocumentObjectGroupPython] H_element057  label="H_element : 0.136"  # scripted group (container) (typed FeaturePython)
  n = 0.102
FEATURE [App::DocumentObjectGroupPython] C_element063  label="C_element : 0.143"  # scripted group (container) (typed FeaturePython)
  n = 0.143
FEATURE [App::DocumentObjectGroupPython] N_element025  label="N_element : 0.034"  # scripted group (container) (typed FeaturePython)
  n = 0.034
FEATURE [App::DocumentObjectGroupPython] O_element065  label="O_element : 0.710"  # scripted group (container) (typed FeaturePython)
  n = 0.71
FEATURE [App::DocumentObjectGroupPython] Na_element011  label="Na_element : 0.098"  # scripted group (container) (typed FeaturePython)
  n = 0.001
FEATURE [App::DocumentObjectGroupPython] P_element007  label="P_element : 0.002"  # scripted group (container) (typed FeaturePython)
  n = 0.002
FEATURE [App::DocumentObjectGroupPython] S_element017  label="S_element : 0.018"  # scripted group (container) (typed FeaturePython)
  n = 0.003
FEATURE [App::DocumentObjectGroupPython] Cl_element016  label="Cl_element : 0.589"  # scripted group (container) (typed FeaturePython)
  n = 0.001
FEATURE [App::DocumentObjectGroupPython] K_element006  label="K_element : 0.004"  # scripted group (container) (typed FeaturePython)
  n = 0.004
FEATURE [App::DocumentObjectGroupPython] G4_MUSCLE_SKELETAL_ICRP  # scripted group (container) (typed FeaturePython)
  Dunit = g/cm3
  Dvalue = 1.05
  Group = -> [H_element057,C_element063,N_element025,O_element065,Na_element011,P_element007,S_element017,Cl_element016,K_element006]
  conduct = 2
  density = 1
  expand = 3
  formula = G4_MUSCLE_SKELETAL_ICRP
  name = G4_MUSCLE_SKELETAL_ICRP
  specific = 4
FEATURE [App::DocumentObjectGroupPython] H_element058  label="H_element : 0.137"  # scripted group (container) (typed FeaturePython)
  n = 0.102102
FEATURE [App::DocumentObjectGroupPython] C_element064  label="C_element : 0.123"  # scripted group (container) (typed FeaturePython)
  n = 0.123123
FEATURE [App::DocumentObjectGroupPython] N_element026  label="N_element : 0.756"  # scripted group (container) (typed FeaturePython)
  n = 0.035035
FEATURE [App::DocumentObjectGroupPython] O_element066  label="O_element : 0.730"  # scripted group (container) (typed FeaturePython)
  n = 0.72973
FEATURE [App::DocumentObjectGroupPython] Na_element012  label="Na_element : 0.099"  # scripted group (container) (typed FeaturePython)
  n = 0.001001
FEATURE [App::DocumentObjectGroupPython] P_element008  label="P_element : 0.106"  # scripted group (container) (typed FeaturePython)
  n = 0.002002
FEATURE [App::DocumentObjectGroupPython] S_element018  label="S_element : 0.019"  # scripted group (container) (typed FeaturePython)
  n = 0.004004
FEATURE [App::DocumentObjectGroupPython] K_element007  label="K_element : 0.016"  # scripted group (container) (typed FeaturePython)
  n = 0.003003
FEATURE [App::DocumentObjectGroupPython] G4_MUSCLE_STRIATED_ICRU  # scripted group (container) (typed FeaturePython)
  Dunit = g/cm3
  Dvalue = 1.04
  Group = -> [H_element058,C_element064,N_element026,O_element066,Na_element012,P_element008,S_element018,K_element007]
  conduct = 2
  density = 1
  expand = 3
  formula = G4_MUSCLE_STRIATED_ICRU
  name = G4_MUSCLE_STRIATED_ICRU
  specific = 4
FEATURE [App::DocumentObjectGroupPython] H_element059  label="H_element : 0.098"  # scripted group (container) (typed FeaturePython)
  n = 0.0982341
FEATURE [App::DocumentObjectGroupPython] C_element065  label="C_element : 0.156"  # scripted group (container) (typed FeaturePython)
  n = 0.156214
FEATURE [App::DocumentObjectGroupPython] N_element027  label="N_element : 0.757"  # scripted group (container) (typed FeaturePython)
  n = 0.035451
FEATURE [App::DocumentObjectGroupPython] O_element067  label="O_element : 0.880"  # scripted group (container) (typed FeaturePython)
  n = 0.710101
FEATURE [App::DocumentObjectGroupPython] G4_MUSCLE_WITH_SUCROSE  # scripted group (container) (typed FeaturePython)
  Dunit = g/cm3
  Dvalue = 1.11
  Group = -> [H_element059,C_element065,N_element027,O_element067]
  conduct = 2
  density = 1
  expand = 3
  formula = G4_MUSCLE_WITH_SUCROSE
  name = G4_MUSCLE_WITH_SUCROSE
  specific = 4
FEATURE [App::DocumentObjectGroupPython] H_element060  label="H_element : 0.138"  # scripted group (container) (typed FeaturePython)
  n = 0.101969
FEATURE [App::DocumentObjectGroupPython] C_element066  label="C_element : 0.120"  # scripted group (container) (typed FeaturePython)
  n = 0.120058
FEATURE [App::DocumentObjectGroupPython] N_element028  label="N_element : 0.758"  # scripted group (container) (typed FeaturePython)
  n = 0.035451
FEATURE [App::DocumentObjectGroupPython] O_element068  label="O_element : 0.743"  # scripted group (container) (typed FeaturePython)
  n = 0.742522
FEATURE [App::DocumentObjectGroupPython] G4_MUSCLE_WITHOUT_SUCROSE  # scripted group (container) (typed FeaturePython)
  Dunit = g/cm3
  Dvalue = 1.07
  Group = -> [H_element060,C_element066,N_element028,O_element068]
  conduct = 2
  density = 1
  expand = 3
  formula = G4_MUSCLE_WITHOUT_SUCROSE
  name = G4_MUSCLE_WITHOUT_SUCROSE
  specific = 4
FEATURE [App::DocumentObjectGroupPython] C_element067  label="C_element : 10"  # scripted group (container) (typed FeaturePython)
  n = 10
  ref = C_element
FEATURE [App::DocumentObjectGroupPython] H_element061  label="H_element : 030"  # scripted group (container) (typed FeaturePython)
  n = 8
  ref = H_element
FEATURE [App::DocumentObjectGroupPython] G4_NAPHTHALENE  # scripted group (container) (typed FeaturePython)
  Dunit = g/cm3
  Dvalue = 1.145
  Group = -> [C_element067,H_element061]
  conduct = 2
  density = 1
  expand = 3
  formula = G4_NAPHTHALENE
  name = G4_NAPHTHALENE
  specific = 4
FEATURE [App::DocumentObjectGroupPython] C_element068  label="C_element : 034"  # scripted group (container) (typed FeaturePython)
  n = 6
  ref = C_element
FEATURE [App::DocumentObjectGroupPython] H_element062  label="H_element : 031"  # scripted group (container) (typed FeaturePython)
  n = 5
  ref = H_element
FEATURE [App::DocumentObjectGroupPython] N_element029  label="N_element : 012"  # scripted group (container) (typed FeaturePython)
  n = 1
  ref = N_element
FEATURE [App::DocumentObjectGroupPython] O_element069  label="O_element : 034"  # scripted group (container) (typed FeaturePython)
  n = 2
  ref = O_element
FEATURE [App::DocumentObjectGroupPython] G4_NITROBENZENE  # scripted group (container) (typed FeaturePython)
  Dunit = g/cm3
  Dvalue = 1.19867
  Group = -> [C_element068,H_element062,N_element029,O_element069]
  conduct = 2
  density = 1
  expand = 3
  formula = G4_NITROBENZENE
  name = G4_NITROBENZENE
  specific = 4
FEATURE [App::DocumentObjectGroupPython] N_element030  label="N_element : 013"  # scripted group (container) (typed FeaturePython)
  n = 2
  ref = N_element
FEATURE [App::DocumentObjectGroupPython] O_element070  label="O_element : 035"  # scripted group (container) (typed FeaturePython)
  n = 1
  ref = O_element
FEATURE [App::DocumentObjectGroupPython] G4_NITROUS_OXIDE  # scripted group (container) (typed FeaturePython)
  Dunit = g/cm3
  Dvalue = 0.00183094
  Group = -> [N_element030,O_element070]
  conduct = 2
  density = 1
  expand = 3
  formula = G4_NITROUS_OXIDE
  name = G4_NITROUS_OXIDE
  specific = 4
FEATURE [App::DocumentObjectGroupPython] H_element063  label="H_element : 0.104"  # scripted group (container) (typed FeaturePython)
  n = 0.103509
FEATURE [App::DocumentObjectGroupPython] C_element069  label="C_element : 0.648"  # scripted group (container) (typed FeaturePython)
  n = 0.648416
FEATURE [App::DocumentObjectGroupPython] N_element031  label="N_element : 0.100"  # scripted group (container) (typed FeaturePython)
  n = 0.0995361
FEATURE [App::DocumentObjectGroupPython] O_element071  label="O_element : 0.149"  # scripted group (container) (typed FeaturePython)
  n = 0.148539
FEATURE [App::DocumentObjectGroupPython] G4_NYLON_8062  label="G4_NYLON-8062"  # scripted group (container) (typed FeaturePython)
  Dunit = g/cm3
  Dvalue = 1.08
  Group = -> [H_element063,C_element069,N_element031,O_element071]
  conduct = 2
  density = 1
  expand = 3
  formula = G4_NYLON-8062
  name = G4_NYLON-8062
  specific = 4
FEATURE [App::DocumentObjectGroupPython] C_element070  label="C_element : 035"  # scripted group (container) (typed FeaturePython)
  n = 6
  ref = C_element
FEATURE [App::DocumentObjectGroupPython] H_element064  label="H_element : 11"  # scripted group (container) (typed FeaturePython)
  n = 11
  ref = H_element
FEATURE [App::DocumentObjectGroupPython] N_element032  label="N_element : 014"  # scripted group (container) (typed FeaturePython)
  n = 1
  ref = N_element
FEATURE [App::DocumentObjectGroupPython] O_element072  label="O_element : 036"  # scripted group (container) (typed FeaturePython)
  n = 1
  ref = O_element
FEATURE [App::DocumentObjectGroupPython] G4_NYLON_6_6  label="G4_NYLON-6-6"  # scripted group (container) (typed FeaturePython)
  Dunit = g/cm3
  Dvalue = 1.14
  Group = -> [C_element070,H_element064,N_element032,O_element072]
  conduct = 2
  density = 1
  expand = 3
  formula = G4_NYLON-6-6
  name = G4_NYLON-6-6
  specific = 4
FEATURE [App::DocumentObjectGroupPython] H_element065  label="H_element : 0.139"  # scripted group (container) (typed FeaturePython)
  n = 0.107062
FEATURE [App::DocumentObjectGroupPython] C_element071  label="C_element : 0.680"  # scripted group (container) (typed FeaturePython)
  n = 0.680449
FEATURE [App::DocumentObjectGroupPython] N_element033  label="N_element : 0.099"  # scripted group (container) (typed FeaturePython)
  n = 0.099189
FEATURE [App::DocumentObjectGroupPython] O_element073  label="O_element : 0.113"  # scripted group (container) (typed FeaturePython)
  n = 0.1133
FEATURE [App::DocumentObjectGroupPython] G4_NYLON_6_10  label="G4_NYLON-6-10"  # scripted group (container) (typed FeaturePython)
  Dunit = g/cm3
  Dvalue = 1.14
  Group = -> [H_element065,C_element071,N_element033,O_element073]
  conduct = 2
  density = 1
  expand = 3
  formula = G4_NYLON-6-10
  name = G4_NYLON-6-10
  specific = 4
FEATURE [App::DocumentObjectGroupPython] H_element066  label="H_element : 0.140"  # scripted group (container) (typed FeaturePython)
  n = 0.115476
FEATURE [App::DocumentObjectGroupPython] C_element072  label="C_element : 0.721"  # scripted group (container) (typed FeaturePython)
  n = 0.720818
FEATURE [App::DocumentObjectGroupPython] N_element034  label="N_element : 0.076"  # scripted group (container) (typed FeaturePython)
  n = 0.0764169
FEATURE [App::DocumentObjectGroupPython] O_element074  label="O_element : 0.087"  # scripted group (container) (typed FeaturePython)
  n = 0.0872889
FEATURE [App::DocumentObjectGroupPython] G4_NYLON_11_RILSAN  label="G4_NYLON-11_RILSAN"  # scripted group (container) (typed FeaturePython)
  Dunit = g/cm3
  Dvalue = 1.425
  Group = -> [H_element066,C_element072,N_element034,O_element074]
  conduct = 2
  density = 1
  expand = 3
  formula = G4_NYLON-11_RILSAN
  name = G4_NYLON-11_RILSAN
  specific = 4
FEATURE [App::DocumentObjectGroupPython] C_element073  label="C_element : 8"  # scripted group (container) (typed FeaturePython)
  n = 8
  ref = C_element
FEATURE [App::DocumentObjectGroupPython] H_element067  label="H_element : 18"  # scripted group (container) (typed FeaturePython)
  n = 18
  ref = H_element
FEATURE [App::DocumentObjectGroupPython] G4_OCTANE  # scripted group (container) (typed FeaturePython)
  Dunit = g/cm3
  Dvalue = 0.7026
  Group = -> [C_element073,H_element067]
  conduct = 2
  density = 1
  expand = 3
  formula = G4_OCTANE
  name = G4_OCTANE
  specific = 4
FEATURE [App::DocumentObjectGroupPython] C_element074  label="C_element : 25"  # scripted group (container) (typed FeaturePython)
  n = 25
  ref = C_element
FEATURE [App::DocumentObjectGroupPython] H_element068  label="H_element : 52"  # scripted group (container) (typed FeaturePython)
  n = 52
  ref = H_element
FEATURE [App::DocumentObjectGroupPython] G4_PARAFFIN  # scripted group (container) (typed FeaturePython)
  Dunit = g/cm3
  Dvalue = 0.93
  Group = -> [C_element074,H_element068]
  conduct = 2
  density = 1
  expand = 3
  formula = G4_PARAFFIN
  name = G4_PARAFFIN
  specific = 4
FEATURE [App::DocumentObjectGroupPython] C_element075  label="C_element : 036"  # scripted group (container) (typed FeaturePython)
  n = 5
  ref = C_element
FEATURE [App::DocumentObjectGroupPython] H_element069  label="H_element : 032"  # scripted group (container) (typed FeaturePython)
  n = 12
  ref = H_element
FEATURE [App::DocumentObjectGroupPython] G4_N_PENTANE  label="G4_N-PENTANE"  # scripted group (container) (typed FeaturePython)
  Dunit = g/cm3
  Dvalue = 0.6262
  Group = -> [C_element075,H_element069]
  conduct = 2
  density = 1
  expand = 3
  formula = G4_N-PENTANE
  name = G4_N-PENTANE
  specific = 4
FEATURE [App::DocumentObjectGroupPython] H_element070  label="H_element : 0.014"  # scripted group (container) (typed FeaturePython)
  n = 0.0141
FEATURE [App::DocumentObjectGroupPython] C_element076  label="C_element : 0.072"  # scripted group (container) (typed FeaturePython)
  n = 0.072261
FEATURE [App::DocumentObjectGroupPython] N_element035  label="N_element : 0.019"  # scripted group (container) (typed FeaturePython)
  n = 0.01932
FEATURE [App::DocumentObjectGroupPython] O_element075  label="O_element : 0.066"  # scripted group (container) (typed FeaturePython)
  n = 0.066101
FEATURE [App::DocumentObjectGroupPython] S_element019  label="S_element : 0.020"  # scripted group (container) (typed FeaturePython)
  n = 0.00189
FEATURE [App::DocumentObjectGroupPython] Br_element004  label="Br_element : 0.349"  # scripted group (container) (typed FeaturePython)
  n = 0.349103
FEATURE [App::DocumentObjectGroupPython] Ag_element001  label="Ag_element : 0.474"  # scripted group (container) (typed FeaturePython)
  n = 0.474105
FEATURE [App::DocumentObjectGroupPython] I_element005  label="I_element : 0.003"  # scripted group (container) (typed FeaturePython)
  n = 0.00312
FEATURE [App::DocumentObjectGroupPython] G4_PHOTO_EMULSION  # scripted group (container) (typed FeaturePython)
  Dunit = g/cm3
  Dvalue = 3.815
  Group = -> [H_element070,C_element076,N_element035,O_element075,S_element019,Br_element004,Ag_element001,I_element005]
  conduct = 2
  density = 1
  expand = 3
  formula = G4_PHOTO_EMULSION
  name = G4_PHOTO_EMULSION
  specific = 4
FEATURE [App::DocumentObjectGroupPython] C_element077  label="C_element : 9"  # scripted group (container) (typed FeaturePython)
  n = 9
  ref = C_element
FEATURE [App::DocumentObjectGroupPython] H_element071  label="H_element : 033"  # scripted group (container) (typed FeaturePython)
  n = 10
  ref = H_element
FEATURE [App::DocumentObjectGroupPython] G4_PLASTIC_SC_VINYLTOLUENE  # scripted group (container) (typed FeaturePython)
  Dunit = g/cm3
  Dvalue = 1.032
  Group = -> [C_element077,H_element071]
  conduct = 2
  density = 1
  expand = 3
  formula = G4_PLASTIC_SC_VINYLTOLUENE
  name = G4_PLASTIC_SC_VINYLTOLUENE
  specific = 4
FEATURE [App::DocumentObjectGroupPython] Pu_element001  label="Pu_element : 1"  # scripted group (container) (typed FeaturePython)
  n = 1
  ref = Pu_element
FEATURE [App::DocumentObjectGroupPython] O_element076  label="O_element : 037"  # scripted group (container) (typed FeaturePython)
  n = 2
  ref = O_element
FEATURE [App::DocumentObjectGroupPython] G4_PLUTONIUM_DIOXIDE  # scripted group (container) (typed FeaturePython)
  Dunit = g/cm3
  Dvalue = 11.46
  Group = -> [Pu_element001,O_element076]
  conduct = 2
  density = 1
  expand = 3
  formula = G4_PLUTONIUM_DIOXIDE
  name = G4_PLUTONIUM_DIOXIDE
  specific = 4
FEATURE [App::DocumentObjectGroupPython] C_element078  label="C_element : 037"  # scripted group (container) (typed FeaturePython)
  n = 3
  ref = C_element
FEATURE [App::DocumentObjectGroupPython] H_element072  label="H_element : 034"  # scripted group (container) (typed FeaturePython)
  n = 3
  ref = H_element
FEATURE [App::DocumentObjectGroupPython] N_element036  label="N_element : 015"  # scripted group (container) (typed FeaturePython)
  n = 1
  ref = N_element
FEATURE [App::DocumentObjectGroupPython] G4_POLYACRYLONITRILE  # scripted group (container) (typed FeaturePython)
  Dunit = g/cm3
  Dvalue = 1.17
  Group = -> [C_element078,H_element072,N_element036]
  conduct = 2
  density = 1
  expand = 3
  formula = G4_POLYACRYLONITRILE
  name = G4_POLYACRYLONITRILE
  specific = 4
FEATURE [App::DocumentObjectGroupPython] C_element079  label="C_element : 16"  # scripted group (container) (typed FeaturePython)
  n = 16
  ref = C_element
FEATURE [App::DocumentObjectGroupPython] H_element073  label="H_element : 035"  # scripted group (container) (typed FeaturePython)
  n = 14
  ref = H_element
FEATURE [App::DocumentObjectGroupPython] O_element077  label="O_element : 038"  # scripted group (container) (typed FeaturePython)
  n = 3
  ref = O_element
FEATURE [App::DocumentObjectGroupPython] G4_POLYCARBONATE  # scripted group (container) (typed FeaturePython)
  Dunit = g/cm3
  Dvalue = 1.2
  Group = -> [C_element079,H_element073,O_element077]
  conduct = 2
  density = 1
  expand = 3
  formula = G4_POLYCARBONATE
  name = G4_POLYCARBONATE
  specific = 4
FEATURE [App::DocumentObjectGroupPython] C_element080  label="C_element : 038"  # scripted group (container) (typed FeaturePython)
  n = 8
  ref = C_element
FEATURE [App::DocumentObjectGroupPython] H_element074  label="H_element : 036"  # scripted group (container) (typed FeaturePython)
  n = 7
  ref = H_element
FEATURE [App::DocumentObjectGroupPython] Cl_element017  label="Cl_element : 007"  # scripted group (container) (typed FeaturePython)
  n = 1
  ref = Cl_element
FEATURE [App::DocumentObjectGroupPython] G4_POLYCHLOROSTYRENE  # scripted group (container) (typed FeaturePython)
  Dunit = g/cm3
  Dvalue = 1.3
  Group = -> [C_element080,H_element074,Cl_element017]
  conduct = 2
  density = 1
  expand = 3
  formula = G4_POLYCHLOROSTYRENE
  name = G4_POLYCHLOROSTYRENE
  specific = 4
FEATURE [App::DocumentObjectGroupPython] C_element081  label="C_element : 039"  # scripted group (container) (typed FeaturePython)
  n = 1
  ref = C_element
FEATURE [App::DocumentObjectGroupPython] H_element075  label="H_element : 037"  # scripted group (container) (typed FeaturePython)
  n = 2
  ref = H_element
FEATURE [App::DocumentObjectGroupPython] G4_POLYETHYLENE  # scripted group (container) (typed FeaturePython)
  Dunit = g/cm3
  Dvalue = 0.94
  Group = -> [C_element081,H_element075]
  conduct = 2
  density = 1
  expand = 3
  formula = G4_POLYETHYLENE
  name = G4_POLYETHYLENE
  specific = 4
FEATURE [App::DocumentObjectGroupPython] C_element082  label="C_element : 040"  # scripted group (container) (typed FeaturePython)
  n = 10
  ref = C_element
FEATURE [App::DocumentObjectGroupPython] H_element076  label="H_element : 038"  # scripted group (container) (typed FeaturePython)
  n = 8
  ref = H_element
FEATURE [App::DocumentObjectGroupPython] O_element078  label="O_element : 039"  # scripted group (container) (typed FeaturePython)
  n = 4
  ref = O_element
FEATURE [App::DocumentObjectGroupPython] G4_MYLAR  # scripted group (container) (typed FeaturePython)
  Dunit = g/cm3
  Dvalue = 1.4
  Group = -> [C_element082,H_element076,O_element078]
  conduct = 2
  density = 1
  expand = 3
  formula = G4_MYLAR
  name = G4_MYLAR
  specific = 4
FEATURE [App::DocumentObjectGroupPython] C_element083  label="C_element : 041"  # scripted group (container) (typed FeaturePython)
  n = 5
  ref = C_element
FEATURE [App::DocumentObjectGroupPython] H_element077  label="H_element : 039"  # scripted group (container) (typed FeaturePython)
  n = 8
  ref = H_element
FEATURE [App::DocumentObjectGroupPython] O_element079  label="O_element : 040"  # scripted group (container) (typed FeaturePython)
  n = 2
  ref = O_element
FEATURE [App::DocumentObjectGroupPython] G4_PLEXIGLASS  # scripted group (container) (typed FeaturePython)
  Dunit = g/cm3
  Dvalue = 1.19
  Group = -> [C_element083,H_element077,O_element079]
  conduct = 2
  density = 1
  expand = 3
  formula = G4_PLEXIGLASS
  name = G4_PLEXIGLASS
  specific = 4
FEATURE [App::DocumentObjectGroupPython] C_element084  label="C_element : 042"  # scripted group (container) (typed FeaturePython)
  n = 1
  ref = C_element
FEATURE [App::DocumentObjectGroupPython] H_element078  label="H_element : 040"  # scripted group (container) (typed FeaturePython)
  n = 2
  ref = H_element
FEATURE [App::DocumentObjectGroupPython] O_element080  label="O_element : 041"  # scripted group (container) (typed FeaturePython)
  n = 1
  ref = O_element
FEATURE [App::DocumentObjectGroupPython] G4_POLYOXYMETHYLENE  # scripted group (container) (typed FeaturePython)
  Dunit = g/cm3
  Dvalue = 1.425
  Group = -> [C_element084,H_element078,O_element080]
  conduct = 2
  density = 1
  expand = 3
  formula = G4_POLYOXYMETHYLENE
  name = G4_POLYOXYMETHYLENE
  specific = 4
FEATURE [App::DocumentObjectGroupPython] C_element085  label="C_element : 043"  # scripted group (container) (typed FeaturePython)
  n = 2
  ref = C_element
FEATURE [App::DocumentObjectGroupPython] H_element079  label="H_element : 041"  # scripted group (container) (typed FeaturePython)
  n = 4
  ref = H_element
FEATURE [App::DocumentObjectGroupPython] G4_POLYPROPYLENE  # scripted group (container) (typed FeaturePython)
  Dunit = g/cm3
  Dvalue = 0.9
  Group = -> [C_element085,H_element079]
  conduct = 2
  density = 1
  expand = 3
  formula = G4_POLYPROPYLENE
  name = G4_POLYPROPYLENE
  specific = 4
FEATURE [App::DocumentObjectGroupPython] C_element086  label="C_element : 044"  # scripted group (container) (typed FeaturePython)
  n = 8
  ref = C_element
FEATURE [App::DocumentObjectGroupPython] H_element080  label="H_element : 042"  # scripted group (container) (typed FeaturePython)
  n = 8
  ref = H_element
FEATURE [App::DocumentObjectGroupPython] G4_POLYSTYRENE  # scripted group (container) (typed FeaturePython)
  Dunit = g/cm3
  Dvalue = 1.06
  Group = -> [C_element086,H_element080]
  conduct = 2
  density = 1
  expand = 3
  formula = G4_POLYSTYRENE
  name = G4_POLYSTYRENE
  specific = 4
FEATURE [App::DocumentObjectGroupPython] C_element087  label="C_element : 045"  # scripted group (container) (typed FeaturePython)
  n = 2
  ref = C_element
FEATURE [App::DocumentObjectGroupPython] F_element014  label="F_element : 4"  # scripted group (container) (typed FeaturePython)
  n = 4
  ref = F_element
FEATURE [App::DocumentObjectGroupPython] G4_TEFLON  # scripted group (container) (typed FeaturePython)
  Dunit = g/cm3
  Dvalue = 2.2
  Group = -> [C_element087,F_element014]
  conduct = 2
  density = 1
  expand = 3
  formula = G4_TEFLON
  name = G4_TEFLON
  specific = 4
FEATURE [App::DocumentObjectGroupPython] C_element088  label="C_element : 046"  # scripted group (container) (typed FeaturePython)
  n = 2
  ref = C_element
FEATURE [App::DocumentObjectGroupPython] F_element015  label="F_element : 006"  # scripted group (container) (typed FeaturePython)
  n = 3
  ref = F_element
FEATURE [App::DocumentObjectGroupPython] Cl_element018  label="Cl_element : 008"  # scripted group (container) (typed FeaturePython)
  n = 1
  ref = Cl_element
FEATURE [App::DocumentObjectGroupPython] G4_POLYTRIFLUOROCHLOROETHYLENE  # scripted group (container) (typed FeaturePython)
  Dunit = g/cm3
  Dvalue = 2.1
  Group = -> [C_element088,F_element015,Cl_element018]
  conduct = 2
  density = 1
  expand = 3
  formula = G4_POLYTRIFLUOROCHLOROETHYLENE
  name = G4_POLYTRIFLUOROCHLOROETHYLENE
  specific = 4
FEATURE [App::DocumentObjectGroupPython] C_element089  label="C_element : 047"  # scripted group (container) (typed FeaturePython)
  n = 4
  ref = C_element
FEATURE [App::DocumentObjectGroupPython] H_element081  label="H_element : 043"  # scripted group (container) (typed FeaturePython)
  n = 6
  ref = H_element
FEATURE [App::DocumentObjectGroupPython] O_element081  label="O_element : 042"  # scripted group (container) (typed FeaturePython)
  n = 2
  ref = O_element
FEATURE [App::DocumentObjectGroupPython] G4_POLYVINYL_ACETATE  # scripted group (container) (typed FeaturePython)
  Dunit = g/cm3
  Dvalue = 1.19
  Group = -> [C_element089,H_element081,O_element081]
  conduct = 2
  density = 1
  expand = 3
  formula = G4_POLYVINYL_ACETATE
  name = G4_POLYVINYL_ACETATE
  specific = 4
FEATURE [App::DocumentObjectGroupPython] C_element090  label="C_element : 048"  # scripted group (container) (typed FeaturePython)
  n = 2
  ref = C_element
FEATURE [App::DocumentObjectGroupPython] H_element082  label="H_element : 044"  # scripted group (container) (typed FeaturePython)
  n = 4
  ref = H_element
FEATURE [App::DocumentObjectGroupPython] O_element082  label="O_element : 043"  # scripted group (container) (typed FeaturePython)
  n = 1
  ref = O_element
FEATURE [App::DocumentObjectGroupPython] G4_POLYVINYL_ALCOHOL  # scripted group (container) (typed FeaturePython)
  Dunit = g/cm3
  Dvalue = 1.3
  Group = -> [C_element090,H_element082,O_element082]
  conduct = 2
  density = 1
  expand = 3
  formula = G4_POLYVINYL_ALCOHOL
  name = G4_POLYVINYL_ALCOHOL
  specific = 4
FEATURE [App::DocumentObjectGroupPython] C_element091  label="C_element : 049"  # scripted group (container) (typed FeaturePython)
  n = 8
  ref = C_element
FEATURE [App::DocumentObjectGroupPython] H_element083  label="H_element : 045"  # scripted group (container) (typed FeaturePython)
  n = 14
  ref = H_element
FEATURE [App::DocumentObjectGroupPython] O_element083  label="O_element : 044"  # scripted group (container) (typed FeaturePython)
  n = 2
  ref = O_element
FEATURE [App::DocumentObjectGroupPython] G4_POLYVINYL_BUTYRAL  # scripted group (container) (typed FeaturePython)
  Dunit = g/cm3
  Dvalue = 1.12
  Group = -> [C_element091,H_element083,O_element083]
  conduct = 2
  density = 1
  expand = 3
  formula = G4_POLYVINYL_BUTYRAL
  name = G4_POLYVINYL_BUTYRAL
  specific = 4
FEATURE [App::DocumentObjectGroupPython] C_element092  label="C_element : 050"  # scripted group (container) (typed FeaturePython)
  n = 2
  ref = C_element
FEATURE [App::DocumentObjectGroupPython] H_element084  label="H_element : 046"  # scripted group (container) (typed FeaturePython)
  n = 3
  ref = H_element
FEATURE [App::DocumentObjectGroupPython] Cl_element019  label="Cl_element : 009"  # scripted group (container) (typed FeaturePython)
  n = 1
  ref = Cl_element
FEATURE [App::DocumentObjectGroupPython] G4_POLYVINYL_CHLORIDE  # scripted group (container) (typed FeaturePython)
  Dunit = g/cm3
  Dvalue = 1.3
  Group = -> [C_element092,H_element084,Cl_element019]
  conduct = 2
  density = 1
  expand = 3
  formula = G4_POLYVINYL_CHLORIDE
  name = G4_POLYVINYL_CHLORIDE
  specific = 4
FEATURE [App::DocumentObjectGroupPython] C_element093  label="C_element : 051"  # scripted group (container) (typed FeaturePython)
  n = 2
  ref = C_element
FEATURE [App::DocumentObjectGroupPython] H_element085  label="H_element : 047"  # scripted group (container) (typed FeaturePython)
  n = 2
  ref = H_element
FEATURE [App::DocumentObjectGroupPython] Cl_element020  label="Cl_element : 010"  # scripted group (container) (typed FeaturePython)
  n = 2
  ref = Cl_element
FEATURE [App::DocumentObjectGroupPython] G4_POLYVINYLIDENE_CHLORIDE  # scripted group (container) (typed FeaturePython)
  Dunit = g/cm3
  Dvalue = 1.7
  Group = -> [C_element093,H_element085,Cl_element020]
  conduct = 2
  density = 1
  expand = 3
  formula = G4_POLYVINYLIDENE_CHLORIDE
  name = G4_POLYVINYLIDENE_CHLORIDE
  specific = 4
FEATURE [App::DocumentObjectGroupPython] C_element094  label="C_element : 052"  # scripted group (container) (typed FeaturePython)
  n = 2
  ref = C_element
FEATURE [App::DocumentObjectGroupPython] H_element086  label="H_element : 048"  # scripted group (container) (typed FeaturePython)
  n = 2
  ref = H_element
FEATURE [App::DocumentObjectGroupPython] F_element016  label="F_element : 007"  # scripted group (container) (typed FeaturePython)
  n = 2
  ref = F_element
FEATURE [App::DocumentObjectGroupPython] G4_POLYVINYLIDENE_FLUORIDE  # scripted group (container) (typed FeaturePython)
  Dunit = g/cm3
  Dvalue = 1.76
  Group = -> [C_element094,H_element086,F_element016]
  conduct = 2
  density = 1
  expand = 3
  formula = G4_POLYVINYLIDENE_FLUORIDE
  name = G4_POLYVINYLIDENE_FLUORIDE
  specific = 4
FEATURE [App::DocumentObjectGroupPython] C_element095  label="C_element : 053"  # scripted group (container) (typed FeaturePython)
  n = 6
  ref = C_element
FEATURE [App::DocumentObjectGroupPython] H_element087  label="H_element : 9"  # scripted group (container) (typed FeaturePython)
  n = 9
  ref = H_element
FEATURE [App::DocumentObjectGroupPython] N_element037  label="N_element : 016"  # scripted group (container) (typed FeaturePython)
  n = 1
  ref = N_element
FEATURE [App::DocumentObjectGroupPython] O_element084  label="O_element : 045"  # scripted group (container) (typed FeaturePython)
  n = 1
  ref = O_element
FEATURE [App::DocumentObjectGroupPython] G4_POLYVINYL_PYRROLIDONE  # scripted group (container) (typed FeaturePython)
  Dunit = g/cm3
  Dvalue = 1.25
  Group = -> [C_element095,H_element087,N_element037,O_element084]
  conduct = 2
  density = 1
  expand = 3
  formula = G4_POLYVINYL_PYRROLIDONE
  name = G4_POLYVINYL_PYRROLIDONE
  specific = 4
FEATURE [App::DocumentObjectGroupPython] K_element008  label="K_element : 1"  # scripted group (container) (typed FeaturePython)
  n = 1
  ref = K_element
FEATURE [App::DocumentObjectGroupPython] I_element006  label="I_element : 003"  # scripted group (container) (typed FeaturePython)
  n = 1
  ref = I_element
FEATURE [App::DocumentObjectGroupPython] G4_POTASSIUM_IODIDE  # scripted group (container) (typed FeaturePython)
  Dunit = g/cm3
  Dvalue = 3.13
  Group = -> [K_element008,I_element006]
  conduct = 2
  density = 1
  expand = 3
  formula = G4_POTASSIUM_IODIDE
  name = G4_POTASSIUM_IODIDE
  specific = 4
FEATURE [App::DocumentObjectGroupPython] K_element009  label="K_element : 2"  # scripted group (container) (typed FeaturePython)
  n = 2
  ref = K_element
FEATURE [App::DocumentObjectGroupPython] O_element085  label="O_element : 046"  # scripted group (container) (typed FeaturePython)
  n = 1
  ref = O_element
FEATURE [App::DocumentObjectGroupPython] G4_POTASSIUM_OXIDE  # scripted group (container) (typed FeaturePython)
  Dunit = g/cm3
  Dvalue = 2.32
  Group = -> [K_element009,O_element085]
  conduct = 2
  density = 1
  expand = 3
  formula = G4_POTASSIUM_OXIDE
  name = G4_POTASSIUM_OXIDE
  specific = 4
FEATURE [App::DocumentObjectGroupPython] C_element096  label="C_element : 054"  # scripted group (container) (typed FeaturePython)
  n = 3
  ref = C_element
FEATURE [App::DocumentObjectGroupPython] H_element088  label="H_element : 049"  # scripted group (container) (typed FeaturePython)
  n = 8
  ref = H_element
FEATURE [App::DocumentObjectGroupPython] G4_PROPANE  # scripted group (container) (typed FeaturePython)
  Dunit = g/cm3
  Dvalue = 0.00187939
  Group = -> [C_element096,H_element088]
  conduct = 2
  density = 1
  expand = 3
  formula = G4_PROPANE
  name = G4_PROPANE
  specific = 4
FEATURE [App::DocumentObjectGroupPython] C_element097  label="C_element : 055"  # scripted group (container) (typed FeaturePython)
  n = 3
  ref = C_element
FEATURE [App::DocumentObjectGroupPython] H_element089  label="H_element : 050"  # scripted group (container) (typed FeaturePython)
  n = 8
  ref = H_element
FEATURE [App::DocumentObjectGroupPython] G4_lPROPANE  # scripted group (container) (typed FeaturePython)
  Dunit = g/cm3
  Dvalue = 0.43
  Group = -> [C_element097,H_element089]
  conduct = 2
  density = 1
  expand = 3
  formula = G4_lPROPANE
  name = G4_lPROPANE
  specific = 4
FEATURE [App::DocumentObjectGroupPython] C_element098  label="C_element : 056"  # scripted group (container) (typed FeaturePython)
  n = 3
  ref = C_element
FEATURE [App::DocumentObjectGroupPython] H_element090  label="H_element : 051"  # scripted group (container) (typed FeaturePython)
  n = 8
  ref = H_element
FEATURE [App::DocumentObjectGroupPython] O_element086  label="O_element : 047"  # scripted group (container) (typed FeaturePython)
  n = 1
  ref = O_element
FEATURE [App::DocumentObjectGroupPython] G4_N_PROPYL_ALCOHOL  label="G4_N-PROPYL_ALCOHOL"  # scripted group (container) (typed FeaturePython)
  Dunit = g/cm3
  Dvalue = 0.8035
  Group = -> [C_element098,H_element090,O_element086]
  conduct = 2
  density = 1
  expand = 3
  formula = G4_N-PROPYL_ALCOHOL
  name = G4_N-PROPYL_ALCOHOL
  specific = 4
FEATURE [App::DocumentObjectGroupPython] C_element099  label="C_element : 057"  # scripted group (container) (typed FeaturePython)
  n = 5
  ref = C_element
FEATURE [App::DocumentObjectGroupPython] H_element091  label="H_element : 052"  # scripted group (container) (typed FeaturePython)
  n = 5
  ref = H_element
FEATURE [App::DocumentObjectGroupPython] N_element038  label="N_element : 017"  # scripted group (container) (typed FeaturePython)
  n = 1
  ref = N_element
FEATURE [App::DocumentObjectGroupPython] G4_PYRIDINE  # scripted group (container) (typed FeaturePython)
  Dunit = g/cm3
  Dvalue = 0.9819
  Group = -> [C_element099,H_element091,N_element038]
  conduct = 2
  density = 1
  expand = 3
  formula = G4_PYRIDINE
  name = G4_PYRIDINE
  specific = 4
FEATURE [App::DocumentObjectGroupPython] H_element092  label="H_element : 0.144"  # scripted group (container) (typed FeaturePython)
  n = 0.143711
FEATURE [App::DocumentObjectGroupPython] C_element100  label="C_element : 0.856"  # scripted group (container) (typed FeaturePython)
  n = 0.856289
FEATURE [App::DocumentObjectGroupPython] G4_RUBBER_BUTYL  # scripted group (container) (typed FeaturePython)
  Dunit = g/cm3
  Dvalue = 0.92
  Group = -> [H_element092,C_element100]
  conduct = 2
  density = 1
  expand = 3
  formula = G4_RUBBER_BUTYL
  name = G4_RUBBER_BUTYL
  specific = 4
FEATURE [App::DocumentObjectGroupPython] H_element093  label="H_element : 0.118"  # scripted group (container) (typed FeaturePython)
  n = 0.118371
FEATURE [App::DocumentObjectGroupPython] C_element101  label="C_element : 0.882"  # scripted group (container) (typed FeaturePython)
  n = 0.881629
FEATURE [App::DocumentObjectGroupPython] G4_RUBBER_NATURAL  # scripted group (container) (typed FeaturePython)
  Dunit = g/cm3
  Dvalue = 0.92
  Group = -> [H_element093,C_element101]
  conduct = 2
  density = 1
  expand = 3
  formula = G4_RUBBER_NATURAL
  name = G4_RUBBER_NATURAL
  specific = 4
FEATURE [App::DocumentObjectGroupPython] H_element094  label="H_element : 0.145"  # scripted group (container) (typed FeaturePython)
  n = 0.05692
FEATURE [App::DocumentObjectGroupPython] C_element102  label="C_element : 0.543"  # scripted group (container) (typed FeaturePython)
  n = 0.542646
FEATURE [App::DocumentObjectGroupPython] Cl_element021  label="Cl_element : 0.400"  # scripted group (container) (typed FeaturePython)
  n = 0.400434
FEATURE [App::DocumentObjectGroupPython] G4_RUBBER_NEOPRENE  # scripted group (container) (typed FeaturePython)
  Dunit = g/cm3
  Dvalue = 1.23
  Group = -> [H_element094,C_element102,Cl_element021]
  conduct = 2
  density = 1
  expand = 3
  formula = G4_RUBBER_NEOPRENE
  name = G4_RUBBER_NEOPRENE
  specific = 4
FEATURE [App::DocumentObjectGroupPython] Si_element006  label="Si_element : 1"  # scripted group (container) (typed FeaturePython)
  n = 1
  ref = Si_element
FEATURE [App::DocumentObjectGroupPython] O_element087  label="O_element : 048"  # scripted group (container) (typed FeaturePython)
  n = 2
  ref = O_element
FEATURE [App::DocumentObjectGroupPython] G4_SILICON_DIOXIDE  # scripted group (container) (typed FeaturePython)
  Dunit = g/cm3
  Dvalue = 2.32
  Group = -> [Si_element006,O_element087]
  conduct = 2
  density = 1
  expand = 3
  formula = G4_SILICON_DIOXIDE
  name = G4_SILICON_DIOXIDE
  specific = 4
FEATURE [App::DocumentObjectGroupPython] Ag_element002  label="Ag_element : 1"  # scripted group (container) (typed FeaturePython)
  n = 1
  ref = Ag_element
FEATURE [App::DocumentObjectGroupPython] Br_element005  label="Br_element : 003"  # scripted group (container) (typed FeaturePython)
  n = 1
  ref = Br_element
FEATURE [App::DocumentObjectGroupPython] G4_SILVER_BROMIDE  # scripted group (container) (typed FeaturePython)
  Dunit = g/cm3
  Dvalue = 6.473
  Group = -> [Ag_element002,Br_element005]
  conduct = 2
  density = 1
  expand = 3
  formula = G4_SILVER_BROMIDE
  name = G4_SILVER_BROMIDE
  specific = 4
FEATURE [App::DocumentObjectGroupPython] Ag_element003  label="Ag_element : 002"  # scripted group (container) (typed FeaturePython)
  n = 1
  ref = Ag_element
FEATURE [App::DocumentObjectGroupPython] Cl_element022  label="Cl_element : 011"  # scripted group (container) (typed FeaturePython)
  n = 1
  ref = Cl_element
FEATURE [App::DocumentObjectGroupPython] G4_SILVER_CHLORIDE  # scripted group (container) (typed FeaturePython)
  Dunit = g/cm3
  Dvalue = 5.56
  Group = -> [Ag_element003,Cl_element022]
  conduct = 2
  density = 1
  expand = 3
  formula = G4_SILVER_CHLORIDE
  name = G4_SILVER_CHLORIDE
  specific = 4
FEATURE [App::DocumentObjectGroupPython] Br_element006  label="Br_element : 0.423"  # scripted group (container) (typed FeaturePython)
  n = 0.422895
FEATURE [App::DocumentObjectGroupPython] Ag_element004  label="Ag_element : 0.574"  # scripted group (container) (typed FeaturePython)
  n = 0.573748
FEATURE [App::DocumentObjectGroupPython] I_element007  label="I_element : 0.649"  # scripted group (container) (typed FeaturePython)
  n = 0.003357
FEATURE [App::DocumentObjectGroupPython] G4_SILVER_HALIDES  # scripted group (container) (typed FeaturePython)
  Dunit = g/cm3
  Dvalue = 6.47
  Group = -> [Br_element006,Ag_element004,I_element007]
  conduct = 2
  density = 1
  expand = 3
  formula = G4_SILVER_HALIDES
  name = G4_SILVER_HALIDES
  specific = 4
FEATURE [App::DocumentObjectGroupPython] Ag_element005  label="Ag_element : 003"  # scripted group (container) (typed FeaturePython)
  n = 1
  ref = Ag_element
FEATURE [App::DocumentObjectGroupPython] I_element008  label="I_element : 004"  # scripted group (container) (typed FeaturePython)
  n = 1
  ref = I_element
FEATURE [App::DocumentObjectGroupPython] G4_SILVER_IODIDE  # scripted group (container) (typed FeaturePython)
  Dunit = g/cm3
  Dvalue = 6.01
  Group = -> [Ag_element005,I_element008]
  conduct = 2
  density = 1
  expand = 3
  formula = G4_SILVER_IODIDE
  name = G4_SILVER_IODIDE
  specific = 4
FEATURE [App::DocumentObjectGroupPython] H_element095  label="H_element : 0.100"  # scripted group (container) (typed FeaturePython)
  n = 0.1
FEATURE [App::DocumentObjectGroupPython] C_element103  label="C_element : 0.204"  # scripted group (container) (typed FeaturePython)
  n = 0.204
FEATURE [App::DocumentObjectGroupPython] N_element039  label="N_element : 0.759"  # scripted group (container) (typed FeaturePython)
  n = 0.042
FEATURE [App::DocumentObjectGroupPython] O_element088  label="O_element : 0.645"  # scripted group (container) (typed FeaturePython)
  n = 0.645
FEATURE [App::DocumentObjectGroupPython] Na_element013  label="Na_element : 0.100"  # scripted group (container) (typed FeaturePython)
  n = 0.002
FEATURE [App::DocumentObjectGroupPython] P_element009  label="P_element : 0.107"  # scripted group (container) (typed FeaturePython)
  n = 0.001
FEATURE [App::DocumentObjectGroupPython] S_element020  label="S_element : 0.021"  # scripted group (container) (typed FeaturePython)
  n = 0.002
FEATURE [App::DocumentObjectGroupPython] Cl_element023  label="Cl_element : 0.590"  # scripted group (container) (typed FeaturePython)
  n = 0.003
FEATURE [App::DocumentObjectGroupPython] K_element010  label="K_element : 0.001"  # scripted group (container) (typed FeaturePython)
  n = 0.001
FEATURE [App::DocumentObjectGroupPython] G4_SKIN_ICRP  # scripted group (container) (typed FeaturePython)
  Dunit = g/cm3
  Dvalue = 1.09
  Group = -> [H_element095,C_element103,N_element039,O_element088,Na_element013,P_element009,S_element020,Cl_element023,K_element010]
  conduct = 2
  density = 1
  expand = 3
  formula = G4_SKIN_ICRP
  name = G4_SKIN_ICRP
  specific = 4
FEATURE [App::DocumentObjectGroupPython] Na_element014  label="Na_element : 2"  # scripted group (container) (typed FeaturePython)
  n = 2
  ref = Na_element
FEATURE [App::DocumentObjectGroupPython] C_element104  label="C_element : 058"  # scripted group (container) (typed FeaturePython)
  n = 1
  ref = C_element
FEATURE [App::DocumentObjectGroupPython] O_element089  label="O_element : 049"  # scripted group (container) (typed FeaturePython)
  n = 3
  ref = O_element
FEATURE [App::DocumentObjectGroupPython] G4_SODIUM_CARBONATE  # scripted group (container) (typed FeaturePython)
  Dunit = g/cm3
  Dvalue = 2.532
  Group = -> [Na_element014,C_element104,O_element089]
  conduct = 2
  density = 1
  expand = 3
  formula = G4_SODIUM_CARBONATE
  name = G4_SODIUM_CARBONATE
  specific = 4
FEATURE [App::DocumentObjectGroupPython] Na_element015  label="Na_element : 1"  # scripted group (container) (typed FeaturePython)
  n = 1
  ref = Na_element
FEATURE [App::DocumentObjectGroupPython] I_element009  label="I_element : 005"  # scripted group (container) (typed FeaturePython)
  n = 1
  ref = I_element
FEATURE [App::DocumentObjectGroupPython] G4_SODIUM_IODIDE  # scripted group (container) (typed FeaturePython)
  Dunit = g/cm3
  Dvalue = 3.667
  Group = -> [Na_element015,I_element009]
  conduct = 2
  density = 1
  expand = 3
  formula = G4_SODIUM_IODIDE
  name = G4_SODIUM_IODIDE
  specific = 4
FEATURE [App::DocumentObjectGroupPython] Na_element016  label="Na_element : 003"  # scripted group (container) (typed FeaturePython)
  n = 2
  ref = Na_element
FEATURE [App::DocumentObjectGroupPython] O_element090  label="O_element : 050"  # scripted group (container) (typed FeaturePython)
  n = 1
  ref = O_element
FEATURE [App::DocumentObjectGroupPython] G4_SODIUM_MONOXIDE  # scripted group (container) (typed FeaturePython)
  Dunit = g/cm3
  Dvalue = 2.27
  Group = -> [Na_element016,O_element090]
  conduct = 2
  density = 1
  expand = 3
  formula = G4_SODIUM_MONOXIDE
  name = G4_SODIUM_MONOXIDE
  specific = 4
FEATURE [App::DocumentObjectGroupPython] Na_element017  label="Na_element : 004"  # scripted group (container) (typed FeaturePython)
  n = 1
  ref = Na_element
FEATURE [App::DocumentObjectGroupPython] N_element040  label="N_element : 018"  # scripted group (container) (typed FeaturePython)
  n = 1
  ref = N_element
FEATURE [App::DocumentObjectGroupPython] O_element091  label="O_element : 051"  # scripted group (container) (typed FeaturePython)
  n = 3
  ref = O_element
FEATURE [App::DocumentObjectGroupPython] G4_SODIUM_NITRATE  # scripted group (container) (typed FeaturePython)
  Dunit = g/cm3
  Dvalue = 2.261
  Group = -> [Na_element017,N_element040,O_element091]
  conduct = 2
  density = 1
  expand = 3
  formula = G4_SODIUM_NITRATE
  name = G4_SODIUM_NITRATE
  specific = 4
FEATURE [App::DocumentObjectGroupPython] C_element105  label="C_element : 059"  # scripted group (container) (typed FeaturePython)
  n = 14
  ref = C_element
FEATURE [App::DocumentObjectGroupPython] H_element096  label="H_element : 053"  # scripted group (container) (typed FeaturePython)
  n = 12
  ref = H_element
FEATURE [App::DocumentObjectGroupPython] G4_STILBENE  # scripted group (container) (typed FeaturePython)
  Dunit = g/cm3
  Dvalue = 0.9707
  Group = -> [C_element105,H_element096]
  conduct = 2
  density = 1
  expand = 3
  formula = G4_STILBENE
  name = G4_STILBENE
  specific = 4
FEATURE [App::DocumentObjectGroupPython] C_element106  label="C_element : 12"  # scripted group (container) (typed FeaturePython)
  n = 12
  ref = C_element
FEATURE [App::DocumentObjectGroupPython] H_element097  label="H_element : 22"  # scripted group (container) (typed FeaturePython)
  n = 22
  ref = H_element
FEATURE [App::DocumentObjectGroupPython] O_element092  label="O_element : 11"  # scripted group (container) (typed FeaturePython)
  n = 11
  ref = O_element
FEATURE [App::DocumentObjectGroupPython] G4_SUCROSE  # scripted group (container) (typed FeaturePython)
  Dunit = g/cm3
  Dvalue = 1.5805
  Group = -> [C_element106,H_element097,O_element092]
  conduct = 2
  density = 1
  expand = 3
  formula = G4_SUCROSE
  name = G4_SUCROSE
  specific = 4
FEATURE [App::DocumentObjectGroupPython] C_element107  label="C_element : 18"  # scripted group (container) (typed FeaturePython)
  n = 18
  ref = C_element
FEATURE [App::DocumentObjectGroupPython] H_element098  label="H_element : 054"  # scripted group (container) (typed FeaturePython)
  n = 14
  ref = H_element
FEATURE [App::DocumentObjectGroupPython] G4_TERPHENYL  # scripted group (container) (typed FeaturePython)
  Dunit = g/cm3
  Dvalue = 1.24
  Group = -> [C_element107,H_element098]
  conduct = 2
  density = 1
  expand = 3
  formula = G4_TERPHENYL
  name = G4_TERPHENYL
  specific = 4
FEATURE [App::DocumentObjectGroupPython] H_element099  label="H_element : 0.146"  # scripted group (container) (typed FeaturePython)
  n = 0.106
FEATURE [App::DocumentObjectGroupPython] C_element108  label="C_element : 0.883"  # scripted group (container) (typed FeaturePython)
  n = 0.099
FEATURE [App::DocumentObjectGroupPython] N_element041  label="N_element : 0.020"  # scripted group (container) (typed FeaturePython)
  n = 0.02
FEATURE [App::DocumentObjectGroupPython] O_element093  label="O_element : 0.766"  # scripted group (container) (typed FeaturePython)
  n = 0.766
FEATURE [App::DocumentObjectGroupPython] Na_element018  label="Na_element : 0.101"  # scripted group (container) (typed FeaturePython)
  n = 0.002
FEATURE [App::DocumentObjectGroupPython] P_element010  label="P_element : 0.108"  # scripted group (container) (typed FeaturePython)
  n = 0.001
FEATURE [App::DocumentObjectGroupPython] S_element021  label="S_element : 0.022"  # scripted group (container) (typed FeaturePython)
  n = 0.002
FEATURE [App::DocumentObjectGroupPython] Cl_element024  label="Cl_element : 0.002"  # scripted group (container) (typed FeaturePython)
  n = 0.002
FEATURE [App::DocumentObjectGroupPython] K_element011  label="K_element : 0.017"  # scripted group (container) (typed FeaturePython)
  n = 0.002
FEATURE [App::DocumentObjectGroupPython] G4_TESTIS_ICRP  # scripted group (container) (typed FeaturePython)
  Dunit = g/cm3
  Dvalue = 1.04
  Group = -> [H_element099,C_element108,N_element041,O_element093,Na_element018,P_element010,S_element021,Cl_element024,K_element011]
  conduct = 2
  density = 1
  expand = 3
  formula = G4_TESTIS_ICRP
  name = G4_TESTIS_ICRP
  specific = 4
FEATURE [App::DocumentObjectGroupPython] C_element109  label="C_element : 060"  # scripted group (container) (typed FeaturePython)
  n = 2
  ref = C_element
FEATURE [App::DocumentObjectGroupPython] Cl_element025  label="Cl_element : 012"  # scripted group (container) (typed FeaturePython)
  n = 4
  ref = Cl_element
FEATURE [App::DocumentObjectGroupPython] G4_TETRACHLOROETHYLENE  # scripted group (container) (typed FeaturePython)
  Dunit = g/cm3
  Dvalue = 1.625
  Group = -> [C_element109,Cl_element025]
  conduct = 2
  density = 1
  expand = 3
  formula = G4_TETRACHLOROETHYLENE
  name = G4_TETRACHLOROETHYLENE
  specific = 4
FEATURE [App::DocumentObjectGroupPython] Tl_element001  label="Tl_element : 1"  # scripted group (container) (typed FeaturePython)
  n = 1
  ref = Tl_element
FEATURE [App::DocumentObjectGroupPython] Cl_element026  label="Cl_element : 013"  # scripted group (container) (typed FeaturePython)
  n = 1
  ref = Cl_element
FEATURE [App::DocumentObjectGroupPython] G4_THALLIUM_CHLORIDE  # scripted group (container) (typed FeaturePython)
  Dunit = g/cm3
  Dvalue = 7.004
  Group = -> [Tl_element001,Cl_element026]
  conduct = 2
  density = 1
  expand = 3
  formula = G4_THALLIUM_CHLORIDE
  name = G4_THALLIUM_CHLORIDE
  specific = 4
FEATURE [App::DocumentObjectGroupPython] H_element100  label="H_element : 0.147"  # scripted group (container) (typed FeaturePython)
  n = 0.105
FEATURE [App::DocumentObjectGroupPython] C_element110  label="C_element : 0.256"  # scripted group (container) (typed FeaturePython)
  n = 0.256
FEATURE [App::DocumentObjectGroupPython] N_element042  label="N_element : 0.760"  # scripted group (container) (typed FeaturePython)
  n = 0.027
FEATURE [App::DocumentObjectGroupPython] O_element094  label="O_element : 0.602"  # scripted group (container) (typed FeaturePython)
  n = 0.602
FEATURE [App::DocumentObjectGroupPython] Na_element019  label="Na_element : 0.102"  # scripted group (container) (typed FeaturePython)
  n = 0.001
FEATURE [App::DocumentObjectGroupPython] P_element011  label="P_element : 0.109"  # scripted group (container) (typed FeaturePython)
  n = 0.002
FEATURE [App::DocumentObjectGroupPython] S_element022  label="S_element : 0.023"  # scripted group (container) (typed FeaturePython)
  n = 0.003
FEATURE [App::DocumentObjectGroupPython] Cl_element027  label="Cl_element : 0.591"  # scripted group (container) (typed FeaturePython)
  n = 0.002
FEATURE [App::DocumentObjectGroupPython] K_element012  label="K_element : 0.018"  # scripted group (container) (typed FeaturePython)
  n = 0.002
FEATURE [App::DocumentObjectGroupPython] G4_TISSUE_SOFT_ICRP  # scripted group (container) (typed FeaturePython)
  Dunit = g/cm3
  Dvalue = 1.03
  Group = -> [H_element100,C_element110,N_element042,O_element094,Na_element019,P_element011,S_element022,Cl_element027,K_element012]
  conduct = 2
  density = 1
  expand = 3
  formula = G4_TISSUE_SOFT_ICRP
  name = G4_TISSUE_SOFT_ICRP
  specific = 4
FEATURE [App::DocumentObjectGroupPython] H_element101  label="H_element : 0.148"  # scripted group (container) (typed FeaturePython)
  n = 0.101
FEATURE [App::DocumentObjectGroupPython] C_element111  label="C_element : 0.111"  # scripted group (container) (typed FeaturePython)
  n = 0.111
FEATURE [App::DocumentObjectGroupPython] N_element043  label="N_element : 0.026"  # scripted group (container) (typed FeaturePython)
  n = 0.026
FEATURE [App::DocumentObjectGroupPython] O_element095  label="O_element : 0.762"  # scripted group (container) (typed FeaturePython)
  n = 0.762
FEATURE [App::DocumentObjectGroupPython] G4_TISSUE_SOFT_ICRU_4  label="G4_TISSUE_SOFT_ICRU-4"  # scripted group (container) (typed FeaturePython)
  Dunit = g/cm3
  Dvalue = 1
  Group = -> [H_element101,C_element111,N_element043,O_element095]
  conduct = 2
  density = 1
  expand = 3
  formula = G4_TISSUE_SOFT_ICRU-4
  name = G4_TISSUE_SOFT_ICRU-4
  specific = 4
FEATURE [App::DocumentObjectGroupPython] H_element102  label="H_element : 0.149"  # scripted group (container) (typed FeaturePython)
  n = 0.101869
FEATURE [App::DocumentObjectGroupPython] C_element112  label="C_element : 0.456"  # scripted group (container) (typed FeaturePython)
  n = 0.456179
FEATURE [App::DocumentObjectGroupPython] N_element044  label="N_element : 0.761"  # scripted group (container) (typed FeaturePython)
  n = 0.035172
FEATURE [App::DocumentObjectGroupPython] O_element096  label="O_element : 0.407"  # scripted group (container) (typed FeaturePython)
  n = 0.40678
FEATURE [App::DocumentObjectGroupPython] G4_TISSUE_METHANE  label="G4_TISSUE-METHANE"  # scripted group (container) (typed FeaturePython)
  Dunit = g/cm3
  Dvalue = 0.00106409
  Group = -> [H_element102,C_element112,N_element044,O_element096]
  conduct = 2
  density = 1
  expand = 3
  formula = G4_TISSUE-METHANE
  name = G4_TISSUE-METHANE
  specific = 4
FEATURE [App::DocumentObjectGroupPython] H_element103  label="H_element : 0.103"  # scripted group (container) (typed FeaturePython)
  n = 0.102672
FEATURE [App::DocumentObjectGroupPython] C_element113  label="C_element : 0.569"  # scripted group (container) (typed FeaturePython)
  n = 0.56894
FEATURE [App::DocumentObjectGroupPython] N_element045  label="N_element : 0.762"  # scripted group (container) (typed FeaturePython)
  n = 0.035022
FEATURE [App::DocumentObjectGroupPython] O_element097  label="O_element : 0.293"  # scripted group (container) (typed FeaturePython)
  n = 0.293366
FEATURE [App::DocumentObjectGroupPython] G4_TISSUE_PROPANE  label="G4_TISSUE-PROPANE"  # scripted group (container) (typed FeaturePython)
  Dunit = g/cm3
  Dvalue = 0.00182628
  Group = -> [H_element103,C_element113,N_element045,O_element097]
  conduct = 2
  density = 1
  expand = 3
  formula = G4_TISSUE-PROPANE
  name = G4_TISSUE-PROPANE
  specific = 4
FEATURE [App::DocumentObjectGroupPython] Ti_element003  label="Ti_element : 1"  # scripted group (container) (typed FeaturePython)
  n = 1
  ref = Ti_element
FEATURE [App::DocumentObjectGroupPython] O_element098  label="O_element : 052"  # scripted group (container) (typed FeaturePython)
  n = 2
  ref = O_element
FEATURE [App::DocumentObjectGroupPython] G4_TITANIUM_DIOXIDE  # scripted group (container) (typed FeaturePython)
  Dunit = g/cm3
  Dvalue = 4.26
  Group = -> [Ti_element003,O_element098]
  conduct = 2
  density = 1
  expand = 3
  formula = G4_TITANIUM_DIOXIDE
  name = G4_TITANIUM_DIOXIDE
  specific = 4
FEATURE [App::DocumentObjectGroupPython] C_element114  label="C_element : 061"  # scripted group (container) (typed FeaturePython)
  n = 7
  ref = C_element
FEATURE [App::DocumentObjectGroupPython] H_element104  label="H_element : 055"  # scripted group (container) (typed FeaturePython)
  n = 8
  ref = H_element
FEATURE [App::DocumentObjectGroupPython] G4_TOLUENE  # scripted group (container) (typed FeaturePython)
  Dunit = g/cm3
  Dvalue = 0.8669
  Group = -> [C_element114,H_element104]
  conduct = 2
  density = 1
  expand = 3
  formula = G4_TOLUENE
  name = G4_TOLUENE
  specific = 4
FEATURE [App::DocumentObjectGroupPython] C_element115  label="C_element : 062"  # scripted group (container) (typed FeaturePython)
  n = 2
  ref = C_element
FEATURE [App::DocumentObjectGroupPython] H_element105  label="H_element : 056"  # scripted group (container) (typed FeaturePython)
  n = 1
  ref = H_element
FEATURE [App::DocumentObjectGroupPython] Cl_element028  label="Cl_element : 014"  # scripted group (container) (typed FeaturePython)
  n = 3
  ref = Cl_element
FEATURE [App::DocumentObjectGroupPython] G4_TRICHLOROETHYLENE  # scripted group (container) (typed FeaturePython)
  Dunit = g/cm3
  Dvalue = 1.46
  Group = -> [C_element115,H_element105,Cl_element028]
  conduct = 2
  density = 1
  expand = 3
  formula = G4_TRICHLOROETHYLENE
  name = G4_TRICHLOROETHYLENE
  specific = 4
FEATURE [App::DocumentObjectGroupPython] C_element116  label="C_element : 063"  # scripted group (container) (typed FeaturePython)
  n = 6
  ref = C_element
FEATURE [App::DocumentObjectGroupPython] H_element106  label="H_element : 15"  # scripted group (container) (typed FeaturePython)
  n = 15
  ref = H_element
FEATURE [App::DocumentObjectGroupPython] O_element099  label="O_element : 053"  # scripted group (container) (typed FeaturePython)
  n = 4
  ref = O_element
FEATURE [App::DocumentObjectGroupPython] P_element012  label="P_element : 1"  # scripted group (container) (typed FeaturePython)
  n = 1
  ref = P_element
FEATURE [App::DocumentObjectGroupPython] G4_TRIETHYL_PHOSPHATE  # scripted group (container) (typed FeaturePython)
  Dunit = g/cm3
  Dvalue = 1.07
  Group = -> [C_element116,H_element106,O_element099,P_element012]
  conduct = 2
  density = 1
  expand = 3
  formula = G4_TRIETHYL_PHOSPHATE
  name = G4_TRIETHYL_PHOSPHATE
  specific = 4
FEATURE [App::DocumentObjectGroupPython] W_element003  label="W_element : 003"  # scripted group (container) (typed FeaturePython)
  n = 1
  ref = W_element
FEATURE [App::DocumentObjectGroupPython] F_element017  label="F_element : 6"  # scripted group (container) (typed FeaturePython)
  n = 6
  ref = F_element
FEATURE [App::DocumentObjectGroupPython] G4_TUNGSTEN_HEXAFLUORIDE  # scripted group (container) (typed FeaturePython)
  Dunit = g/cm3
  Dvalue = 2.4
  Group = -> [W_element003,F_element017]
  conduct = 2
  density = 1
  expand = 3
  formula = G4_TUNGSTEN_HEXAFLUORIDE
  name = G4_TUNGSTEN_HEXAFLUORIDE
  specific = 4
FEATURE [App::DocumentObjectGroupPython] U_element001  label="U_element : 1"  # scripted group (container) (typed FeaturePython)
  n = 1
  ref = U_element
FEATURE [App::DocumentObjectGroupPython] C_element117  label="C_element : 064"  # scripted group (container) (typed FeaturePython)
  n = 2
  ref = C_element
FEATURE [App::DocumentObjectGroupPython] G4_URANIUM_DICARBIDE  # scripted group (container) (typed FeaturePython)
  Dunit = g/cm3
  Dvalue = 11.28
  Group = -> [U_element001,C_element117]
  conduct = 2
  density = 1
  expand = 3
  formula = G4_URANIUM_DICARBIDE
  name = G4_URANIUM_DICARBIDE
  specific = 4
FEATURE [App::DocumentObjectGroupPython] U_element002  label="U_element : 002"  # scripted group (container) (typed FeaturePython)
  n = 1
  ref = U_element
FEATURE [App::DocumentObjectGroupPython] C_element118  label="C_element : 065"  # scripted group (container) (typed FeaturePython)
  n = 1
  ref = C_element
FEATURE [App::DocumentObjectGroupPython] G4_URANIUM_MONOCARBIDE  # scripted group (container) (typed FeaturePython)
  Dunit = g/cm3
  Dvalue = 13.63
  Group = -> [U_element002,C_element118]
  conduct = 2
  density = 1
  expand = 3
  formula = G4_URANIUM_MONOCARBIDE
  name = G4_URANIUM_MONOCARBIDE
  specific = 4
FEATURE [App::DocumentObjectGroupPython] U_element003  label="U_element : 003"  # scripted group (container) (typed FeaturePython)
  n = 1
  ref = U_element
FEATURE [App::DocumentObjectGroupPython] O_element100  label="O_element : 054"  # scripted group (container) (typed FeaturePython)
  n = 2
  ref = O_element
FEATURE [App::DocumentObjectGroupPython] G4_URANIUM_OXIDE  # scripted group (container) (typed FeaturePython)
  Dunit = g/cm3
  Dvalue = 10.96
  Group = -> [U_element003,O_element100]
  conduct = 2
  density = 1
  expand = 3
  formula = G4_URANIUM_OXIDE
  name = G4_URANIUM_OXIDE
  specific = 4
FEATURE [App::DocumentObjectGroupPython] C_element119  label="C_element : 066"  # scripted group (container) (typed FeaturePython)
  n = 1
  ref = C_element
FEATURE [App::DocumentObjectGroupPython] H_element107  label="H_element : 057"  # scripted group (container) (typed FeaturePython)
  n = 4
  ref = H_element
FEATURE [App::DocumentObjectGroupPython] N_element046  label="N_element : 019"  # scripted group (container) (typed FeaturePython)
  n = 2
  ref = N_element
FEATURE [App::DocumentObjectGroupPython] O_element101  label="O_element : 055"  # scripted group (container) (typed FeaturePython)
  n = 1
  ref = O_element
FEATURE [App::DocumentObjectGroupPython] G4_UREA  # scripted group (container) (typed FeaturePython)
  Dunit = g/cm3
  Dvalue = 1.323
  Group = -> [C_element119,H_element107,N_element046,O_element101]
  conduct = 2
  density = 1
  expand = 3
  formula = G4_UREA
  name = G4_UREA
  specific = 4
FEATURE [App::DocumentObjectGroupPython] C_element120  label="C_element : 067"  # scripted group (container) (typed FeaturePython)
  n = 5
  ref = C_element
FEATURE [App::DocumentObjectGroupPython] H_element108  label="H_element : 058"  # scripted group (container) (typed FeaturePython)
  n = 11
  ref = H_element
FEATURE [App::DocumentObjectGroupPython] N_element047  label="N_element : 020"  # scripted group (container) (typed FeaturePython)
  n = 1
  ref = N_element
FEATURE [App::DocumentObjectGroupPython] O_element102  label="O_element : 056"  # scripted group (container) (typed FeaturePython)
  n = 2
  ref = O_element
FEATURE [App::DocumentObjectGroupPython] G4_VALINE  # scripted group (container) (typed FeaturePython)
  Dunit = g/cm3
  Dvalue = 1.23
  Group = -> [C_element120,H_element108,N_element047,O_element102]
  conduct = 2
  density = 1
  expand = 3
  formula = G4_VALINE
  name = G4_VALINE
  specific = 4
FEATURE [App::DocumentObjectGroupPython] H_element109  label="H_element : 0.009"  # scripted group (container) (typed FeaturePython)
  n = 0.009417
FEATURE [App::DocumentObjectGroupPython] C_element121  label="C_element : 0.281"  # scripted group (container) (typed FeaturePython)
  n = 0.280555
FEATURE [App::DocumentObjectGroupPython] F_element018  label="F_element : 0.710"  # scripted group (container) (typed FeaturePython)
  n = 0.710028
FEATURE [App::DocumentObjectGroupPython] G4_VITON  # scripted group (container) (typed FeaturePython)
  Dunit = g/cm3
  Dvalue = 1.8
  Group = -> [H_element109,C_element121,F_element018]
  conduct = 2
  density = 1
  expand = 3
  formula = G4_VITON
  name = G4_VITON
  specific = 4
FEATURE [App::DocumentObjectGroupPython] H_element110  label="H_element : 059"  # scripted group (container) (typed FeaturePython)
  n = 2
  ref = H_element
FEATURE [App::DocumentObjectGroupPython] O_element103  label="O_element : 057"  # scripted group (container) (typed FeaturePython)
  n = 1
  ref = O_element
FEATURE [App::DocumentObjectGroupPython] G4_WATER  # scripted group (container) (typed FeaturePython)
  Dunit = g/cm3
  Dvalue = 1
  Group = -> [H_element110,O_element103]
  conduct = 2
  density = 1
  expand = 3
  formula = G4_WATER
  name = G4_WATER
  specific = 4
FEATURE [App::DocumentObjectGroupPython] H_element111  label="H_element : 060"  # scripted group (container) (typed FeaturePython)
  n = 2
  ref = H_element
FEATURE [App::DocumentObjectGroupPython] O_element104  label="O_element : 058"  # scripted group (container) (typed FeaturePython)
  n = 1
  ref = O_element
FEATURE [App::DocumentObjectGroupPython] G4_WATER_VAPOR  # scripted group (container) (typed FeaturePython)
  Dunit = g/cm3
  Dvalue = 0.000756182
  Group = -> [H_element111,O_element104]
  conduct = 2
  density = 1
  expand = 3
  formula = G4_WATER_VAPOR
  name = G4_WATER_VAPOR
  specific = 4
FEATURE [App::DocumentObjectGroupPython] C_element122  label="C_element : 068"  # scripted group (container) (typed FeaturePython)
  n = 8
  ref = C_element
FEATURE [App::DocumentObjectGroupPython] H_element112  label="H_element : 061"  # scripted group (container) (typed FeaturePython)
  n = 10
  ref = H_element
FEATURE [App::DocumentObjectGroupPython] G4_XYLENE  # scripted group (container) (typed FeaturePython)
  Dunit = g/cm3
  Dvalue = 0.87
  Group = -> [C_element122,H_element112]
  conduct = 2
  density = 1
  expand = 3
  formula = G4_XYLENE
  name = G4_XYLENE
  specific = 4
FEATURE [App::DocumentObjectGroupPython] C_element123  label="C_element : 069"  # scripted group (container) (typed FeaturePython)
  n = 1
  ref = C_element
FEATURE [App::DocumentObjectGroupPython] G4_GRAPHITE  # scripted group (container) (typed FeaturePython)
  Dunit = g/cm3
  Dvalue = 2.21
  Group = -> [C_element123]
  conduct = 2
  density = 1
  expand = 3
  formula = G4_GRAPHITE
  name = G4_GRAPHITE
  specific = 4
FEATURE [App::DocumentObjectGroupPython] NIST  # scripted group (container) (typed FeaturePython)
  Group = -> [G4_A_150_TISSUE,G4_ACETONE,G4_ACETYLENE,G4_ADENINE,G4_ADIPOSE_TISSUE_ICRP,G4_AIR,G4_ALANINE,G4_ALUMINUM_OXIDE,G4_AMBER,G4_AMMONIA,G4_ANILINE,G4_ANTHRACENE,G4_B_100_BONE,G4_BAKELITE,G4_BARIUM_FLUORIDE,G4_BARIUM_SULFATE,G4_BENZENE,G4_BERYLLIUM_OXIDE,G4_BGO,G4_BLOOD_ICRP,G4_BONE_COMPACT_ICRU,G4_BONE_CORTICAL_ICRP,G4_BORON_CARBIDE,G4_BORON_OXIDE,G4_BRAIN_ICRP,G4_BUTANE,G4_N_BUTYL_ALCOHOL,G4_C_552,+152 more]
FEATURE [App::DocumentObjectGroupPython] H_element113  label="H_element : 062"  # scripted group (container) (typed FeaturePython)
  n = 1
  ref = H_element
FEATURE [App::DocumentObjectGroupPython] G4_H  # scripted group (container) (typed FeaturePython)
  Dunit = g/cm3
  Dvalue = 8.3748e-05
  Group = -> [H_element113]
  conduct = 2
  density = 1
  expand = 3
  formula = H
  name = G4_H
  specific = 4
FEATURE [App::DocumentObjectGroupPython] He_element001  label="He_element : 1"  # scripted group (container) (typed FeaturePython)
  n = 1
  ref = He_element
FEATURE [App::DocumentObjectGroupPython] G4_He  # scripted group (container) (typed FeaturePython)
  Dunit = g/cm3
  Dvalue = 0.000166322
  Group = -> [He_element001]
  conduct = 2
  density = 1
  expand = 3
  formula = He
  name = G4_He
  specific = 4
FEATURE [App::DocumentObjectGroupPython] Li_element008  label="Li_element : 008"  # scripted group (container) (typed FeaturePython)
  n = 1
  ref = Li_element
FEATURE [App::DocumentObjectGroupPython] G4_Li  # scripted group (container) (typed FeaturePython)
  Dunit = g/cm3
  Dvalue = 0.534
  Group = -> [Li_element008]
  conduct = 2
  density = 1
  expand = 3
  formula = Li
  name = G4_Li
  specific = 4
FEATURE [App::DocumentObjectGroupPython] Be_element002  label="Be_element : 002"  # scripted group (container) (typed FeaturePython)
  n = 1
  ref = Be_element
FEATURE [App::DocumentObjectGroupPython] G4_Be  # scripted group (container) (typed FeaturePython)
  Dunit = g/cm3
  Dvalue = 1.848
  Group = -> [Be_element002]
  conduct = 2
  density = 1
  expand = 3
  formula = Be
  name = G4_Be
  specific = 4
FEATURE [App::DocumentObjectGroupPython] B_element007  label="B_element : 007"  # scripted group (container) (typed FeaturePython)
  n = 1
  ref = B_element
FEATURE [App::DocumentObjectGroupPython] G4_B  # scripted group (container) (typed FeaturePython)
  Dunit = g/cm3
  Dvalue = 2.37
  Group = -> [B_element007]
  conduct = 2
  density = 1
  expand = 3
  formula = B
  name = G4_B
  specific = 4
FEATURE [App::DocumentObjectGroupPython] C_element124  label="C_element : 070"  # scripted group (container) (typed FeaturePython)
  n = 1
  ref = C_element
FEATURE [App::DocumentObjectGroupPython] G4_C  # scripted group (container) (typed FeaturePython)
  Dunit = g/cm3
  Dvalue = 2
  Group = -> [C_element124]
  conduct = 2
  density = 1
  expand = 3
  formula = C
  name = G4_C
  specific = 4
FEATURE [App::DocumentObjectGroupPython] N_element048  label="N_element : 021"  # scripted group (container) (typed FeaturePython)
  n = 1
  ref = N_element
FEATURE [App::DocumentObjectGroupPython] G4_N  # scripted group (container) (typed FeaturePython)
  Dunit = g/cm3
  Dvalue = 0.0011652
  Group = -> [N_element048]
  conduct = 2
  density = 1
  expand = 3
  formula = N
  name = G4_N
  specific = 4
FEATURE [App::DocumentObjectGroupPython] O_element105  label="O_element : 059"  # scripted group (container) (typed FeaturePython)
  n = 1
  ref = O_element
FEATURE [App::DocumentObjectGroupPython] G4_O  # scripted group (container) (typed FeaturePython)
  Dunit = g/cm3
  Dvalue = 0.00133151
  Group = -> [O_element105]
  conduct = 2
  density = 1
  expand = 3
  formula = O
  name = G4_O
  specific = 4
FEATURE [App::DocumentObjectGroupPython] F_element019  label="F_element : 008"  # scripted group (container) (typed FeaturePython)
  n = 1
  ref = F_element
FEATURE [App::DocumentObjectGroupPython] G4_F  # scripted group (container) (typed FeaturePython)
  Dunit = g/cm3
  Dvalue = 0.00158029
  Group = -> [F_element019]
  conduct = 2
  density = 1
  expand = 3
  formula = F
  name = G4_F
  specific = 4
FEATURE [App::DocumentObjectGroupPython] Ne_element001  label="Ne_element : 1"  # scripted group (container) (typed FeaturePython)
  n = 1
  ref = Ne_element
FEATURE [App::DocumentObjectGroupPython] G4_Ne  # scripted group (container) (typed FeaturePython)
  Dunit = g/cm3
  Dvalue = 0.000838505
  Group = -> [Ne_element001]
  conduct = 2
  density = 1
  expand = 3
  formula = Ne
  name = G4_Ne
  specific = 4
FEATURE [App::DocumentObjectGroupPython] Na_element020  label="Na_element : 005"  # scripted group (container) (typed FeaturePython)
  n = 1
  ref = Na_element
FEATURE [App::DocumentObjectGroupPython] G4_Na  # scripted group (container) (typed FeaturePython)
  Dunit = g/cm3
  Dvalue = 0.971
  Group = -> [Na_element020]
  conduct = 2
  density = 1
  expand = 3
  formula = Na
  name = G4_Na
  specific = 4
FEATURE [App::DocumentObjectGroupPython] Mg_element011  label="Mg_element : 005"  # scripted group (container) (typed FeaturePython)
  n = 1
  ref = Mg_element
FEATURE [App::DocumentObjectGroupPython] G4_Mg  # scripted group (container) (typed FeaturePython)
  Dunit = g/cm3
  Dvalue = 1.74
  Group = -> [Mg_element011]
  conduct = 2
  density = 1
  expand = 3
  formula = Mg
  name = G4_Mg
  specific = 4
FEATURE [App::DocumentObjectGroupPython] Al_element004  label="Al_element : 1"  # scripted group (container) (typed FeaturePython)
  n = 1
  ref = Al_element
FEATURE [App::DocumentObjectGroupPython] G4_Al  # scripted group (container) (typed FeaturePython)
  Dunit = g/cm3
  Dvalue = 2.699
  Group = -> [Al_element004]
  conduct = 2
  density = 1
  expand = 3
  formula = Al
  name = G4_Al
  specific = 4
FEATURE [App::DocumentObjectGroupPython] Si_element007  label="Si_element : 002"  # scripted group (container) (typed FeaturePython)
  n = 1
  ref = Si_element
FEATURE [App::DocumentObjectGroupPython] G4_Si  # scripted group (container) (typed FeaturePython)
  Dunit = g/cm3
  Dvalue = 2.33
  Group = -> [Si_element007]
  conduct = 2
  density = 1
  expand = 3
  formula = Si
  name = G4_Si
  specific = 4
FEATURE [App::DocumentObjectGroupPython] P_element013  label="P_element : 002"  # scripted group (container) (typed FeaturePython)
  n = 1
  ref = P_element
FEATURE [App::DocumentObjectGroupPython] G4_P  # scripted group (container) (typed FeaturePython)
  Dunit = g/cm3
  Dvalue = 2.2
  Group = -> [P_element013]
  conduct = 2
  density = 1
  expand = 3
  formula = P
  name = G4_P
  specific = 4
FEATURE [App::DocumentObjectGroupPython] S_element023  label="S_element : 007"  # scripted group (container) (typed FeaturePython)
  n = 1
  ref = S_element
FEATURE [App::DocumentObjectGroupPython] G4_S  # scripted group (container) (typed FeaturePython)
  Dunit = g/cm3
  Dvalue = 2
  Group = -> [S_element023]
  conduct = 2
  density = 1
  expand = 3
  formula = S
  name = G4_S
  specific = 4
FEATURE [App::DocumentObjectGroupPython] Cl_element029  label="Cl_element : 015"  # scripted group (container) (typed FeaturePython)
  n = 1
  ref = Cl_element
FEATURE [App::DocumentObjectGroupPython] G4_Cl  # scripted group (container) (typed FeaturePython)
  Dunit = g/cm3
  Dvalue = 0.00299473
  Group = -> [Cl_element029]
  conduct = 2
  density = 1
  expand = 3
  formula = Cl
  name = G4_Cl
  specific = 4
FEATURE [App::DocumentObjectGroupPython] Ar_element002  label="Ar_element : 1"  # scripted group (container) (typed FeaturePython)
  n = 1
  ref = Ar_element
FEATURE [App::DocumentObjectGroupPython] G4_Ar  # scripted group (container) (typed FeaturePython)
  Dunit = g/cm3
  Dvalue = 0.00166201
  Group = -> [Ar_element002]
  conduct = 2
  density = 1
  expand = 3
  formula = Ar
  name = G4_Ar
  specific = 4
FEATURE [App::DocumentObjectGroupPython] K_element013  label="K_element : 003"  # scripted group (container) (typed FeaturePython)
  n = 1
  ref = K_element
FEATURE [App::DocumentObjectGroupPython] G4_K  # scripted group (container) (typed FeaturePython)
  Dunit = g/cm3
  Dvalue = 0.862
  Group = -> [K_element013]
  conduct = 2
  density = 1
  expand = 3
  formula = K
  name = G4_K
  specific = 4
FEATURE [App::DocumentObjectGroupPython] Ca_element014  label="Ca_element : 007"  # scripted group (container) (typed FeaturePython)
  n = 1
  ref = Ca_element
FEATURE [App::DocumentObjectGroupPython] G4_Ca  # scripted group (container) (typed FeaturePython)
  Dunit = g/cm3
  Dvalue = 1.55
  Group = -> [Ca_element014]
  conduct = 2
  density = 1
  expand = 3
  formula = Ca
  name = G4_Ca
  specific = 4
FEATURE [App::DocumentObjectGroupPython] Sc_element001  label="Sc_element : 1"  # scripted group (container) (typed FeaturePython)
  n = 1
  ref = Sc_element
FEATURE [App::DocumentObjectGroupPython] G4_Sc  # scripted group (container) (typed FeaturePython)
  Dunit = g/cm3
  Dvalue = 2.989
  Group = -> [Sc_element001]
  conduct = 2
  density = 1
  expand = 3
  formula = Sc
  name = G4_Sc
  specific = 4
FEATURE [App::DocumentObjectGroupPython] Ti_element004  label="Ti_element : 002"  # scripted group (container) (typed FeaturePython)
  n = 1
  ref = Ti_element
FEATURE [App::DocumentObjectGroupPython] G4_Ti  # scripted group (container) (typed FeaturePython)
  Dunit = g/cm3
  Dvalue = 4.54
  Group = -> [Ti_element004]
  conduct = 2
  density = 1
  expand = 3
  formula = Ti
  name = G4_Ti
  specific = 4
FEATURE [App::DocumentObjectGroupPython] V_element001  label="V_element : 1"  # scripted group (container) (typed FeaturePython)
  n = 1
  ref = V_element
FEATURE [App::DocumentObjectGroupPython] G4_V  # scripted group (container) (typed FeaturePython)
  Dunit = g/cm3
  Dvalue = 6.11
  Group = -> [V_element001]
  conduct = 2
  density = 1
  expand = 3
  formula = V
  name = G4_V
  specific = 4
FEATURE [App::DocumentObjectGroupPython] Cr_element001  label="Cr_element : 1"  # scripted group (container) (typed FeaturePython)
  n = 1
  ref = Cr_element
FEATURE [App::DocumentObjectGroupPython] G4_Cr  # scripted group (container) (typed FeaturePython)
  Dunit = g/cm3
  Dvalue = 7.18
  Group = -> [Cr_element001]
  conduct = 2
  density = 1
  expand = 3
  formula = Cr
  name = G4_Cr
  specific = 4
FEATURE [App::DocumentObjectGroupPython] Mn_element001  label="Mn_element : 1"  # scripted group (container) (typed FeaturePython)
  n = 1
  ref = Mn_element
FEATURE [App::DocumentObjectGroupPython] G4_Mn  # scripted group (container) (typed FeaturePython)
  Dunit = g/cm3
  Dvalue = 7.44
  Group = -> [Mn_element001]
  conduct = 2
  density = 1
  expand = 3
  formula = Mn
  name = G4_Mn
  specific = 4
FEATURE [App::DocumentObjectGroupPython] Fe_element007  label="Fe_element : 004"  # scripted group (container) (typed FeaturePython)
  n = 1
  ref = Fe_element
FEATURE [App::DocumentObjectGroupPython] G4_Fe  # scripted group (container) (typed FeaturePython)
  Dunit = g/cm3
  Dvalue = 7.874
  Group = -> [Fe_element007]
  conduct = 2
  density = 1
  expand = 3
  formula = Fe
  name = G4_Fe
  specific = 4
FEATURE [App::DocumentObjectGroupPython] Co_element001  label="Co_element : 1"  # scripted group (container) (typed FeaturePython)
  n = 1
  ref = Co_element
FEATURE [App::DocumentObjectGroupPython] G4_Co  # scripted group (container) (typed FeaturePython)
  Dunit = g/cm3
  Dvalue = 8.9
  Group = -> [Co_element001]
  conduct = 2
  density = 1
  expand = 3
  formula = Co
  name = G4_Co
  specific = 4
FEATURE [App::DocumentObjectGroupPython] Ni_element001  label="Ni_element : 1"  # scripted group (container) (typed FeaturePython)
  n = 1
  ref = Ni_element
FEATURE [App::DocumentObjectGroupPython] G4_Ni  # scripted group (container) (typed FeaturePython)
  Dunit = g/cm3
  Dvalue = 8.902
  Group = -> [Ni_element001]
  conduct = 2
  density = 1
  expand = 3
  formula = Ni
  name = G4_Ni
  specific = 4
FEATURE [App::DocumentObjectGroupPython] Cu_element001  label="Cu_element : 1"  # scripted group (container) (typed FeaturePython)
  n = 1
  ref = Cu_element
FEATURE [App::DocumentObjectGroupPython] G4_Cu  # scripted group (container) (typed FeaturePython)
  Dunit = g/cm3
  Dvalue = 8.96
  Group = -> [Cu_element001]
  conduct = 2
  density = 1
  expand = 3
  formula = Cu
  name = G4_Cu
  specific = 4
FEATURE [App::DocumentObjectGroupPython] Zn_element001  label="Zn_element : 1"  # scripted group (container) (typed FeaturePython)
  n = 1
  ref = Zn_element
FEATURE [App::DocumentObjectGroupPython] G4_Zn  # scripted group (container) (typed FeaturePython)
  Dunit = g/cm3
  Dvalue = 7.133
  Group = -> [Zn_element001]
  conduct = 2
  density = 1
  expand = 3
  formula = Zn
  name = G4_Zn
  specific = 4
FEATURE [App::DocumentObjectGroupPython] Ga_element002  label="Ga_element : 002"  # scripted group (container) (typed FeaturePython)
  n = 1
  ref = Ga_element
FEATURE [App::DocumentObjectGroupPython] G4_Ga  # scripted group (container) (typed FeaturePython)
  Dunit = g/cm3
  Dvalue = 5.904
  Group = -> [Ga_element002]
  conduct = 2
  density = 1
  expand = 3
  formula = Ga
  name = G4_Ga
  specific = 4
FEATURE [App::DocumentObjectGroupPython] Ge_element002  label="Ge_element : 1"  # scripted group (container) (typed FeaturePython)
  n = 1
  ref = Ge_element
FEATURE [App::DocumentObjectGroupPython] G4_Ge  # scripted group (container) (typed FeaturePython)
  Dunit = g/cm3
  Dvalue = 5.323
  Group = -> [Ge_element002]
  conduct = 2
  density = 1
  expand = 3
  formula = Ge
  name = G4_Ge
  specific = 4
FEATURE [App::DocumentObjectGroupPython] As_element003  label="As_element : 002"  # scripted group (container) (typed FeaturePython)
  n = 1
  ref = As_element
FEATURE [App::DocumentObjectGroupPython] G4_As  # scripted group (container) (typed FeaturePython)
  Dunit = g/cm3
  Dvalue = 5.73
  Group = -> [As_element003]
  conduct = 2
  density = 1
  expand = 3
  formula = As
  name = G4_As
  specific = 4
FEATURE [App::DocumentObjectGroupPython] Se_element001  label="Se_element : 1"  # scripted group (container) (typed FeaturePython)
  n = 1
  ref = Se_element
FEATURE [App::DocumentObjectGroupPython] G4_Se  # scripted group (container) (typed FeaturePython)
  Dunit = g/cm3
  Dvalue = 4.5
  Group = -> [Se_element001]
  conduct = 2
  density = 1
  expand = 3
  formula = Se
  name = G4_Se
  specific = 4
FEATURE [App::DocumentObjectGroupPython] Br_element007  label="Br_element : 004"  # scripted group (container) (typed FeaturePython)
  n = 1
  ref = Br_element
FEATURE [App::DocumentObjectGroupPython] G4_Br  # scripted group (container) (typed FeaturePython)
  Dunit = g/cm3
  Dvalue = 0.0070721
  Group = -> [Br_element007]
  conduct = 2
  density = 1
  expand = 3
  formula = Br
  name = G4_Br
  specific = 4
FEATURE [App::DocumentObjectGroupPython] Kr_element001  label="Kr_element : 1"  # scripted group (container) (typed FeaturePython)
  n = 1
  ref = Kr_element
FEATURE [App::DocumentObjectGroupPython] G4_Kr  # scripted group (container) (typed FeaturePython)
  Dunit = g/cm3
  Dvalue = 0.00347832
  Group = -> [Kr_element001]
  conduct = 2
  density = 1
  expand = 3
  formula = Kr
  name = G4_Kr
  specific = 4
FEATURE [App::DocumentObjectGroupPython] Rb_element001  label="Rb_element : 1"  # scripted group (container) (typed FeaturePython)
  n = 1
  ref = Rb_element
FEATURE [App::DocumentObjectGroupPython] G4_Rb  # scripted group (container) (typed FeaturePython)
  Dunit = g/cm3
  Dvalue = 1.532
  Group = -> [Rb_element001]
  conduct = 2
  density = 1
  expand = 3
  formula = Rb
  name = G4_Rb
  specific = 4
FEATURE [App::DocumentObjectGroupPython] Sr_element001  label="Sr_element : 1"  # scripted group (container) (typed FeaturePython)
  n = 1
  ref = Sr_element
FEATURE [App::DocumentObjectGroupPython] G4_Sr  # scripted group (container) (typed FeaturePython)
  Dunit = g/cm3
  Dvalue = 2.54
  Group = -> [Sr_element001]
  conduct = 2
  density = 1
  expand = 3
  formula = Sr
  name = G4_Sr
  specific = 4
FEATURE [App::DocumentObjectGroupPython] Y_element001  label="Y_element : 1"  # scripted group (container) (typed FeaturePython)
  n = 1
  ref = Y_element
FEATURE [App::DocumentObjectGroupPython] G4_Y  # scripted group (container) (typed FeaturePython)
  Dunit = g/cm3
  Dvalue = 4.469
  Group = -> [Y_element001]
  conduct = 2
  density = 1
  expand = 3
  formula = Y
  name = G4_Y
  specific = 4
FEATURE [App::DocumentObjectGroupPython] Zr_element001  label="Zr_element : 1"  # scripted group (container) (typed FeaturePython)
  n = 1
  ref = Zr_element
FEATURE [App::DocumentObjectGroupPython] G4_Zr  # scripted group (container) (typed FeaturePython)
  Dunit = g/cm3
  Dvalue = 6.506
  Group = -> [Zr_element001]
  conduct = 2
  density = 1
  expand = 3
  formula = Zr
  name = G4_Zr
  specific = 4
FEATURE [App::DocumentObjectGroupPython] Nb_element001  label="Nb_element : 1"  # scripted group (container) (typed FeaturePython)
  n = 1
  ref = Nb_element
FEATURE [App::DocumentObjectGroupPython] G4_Nb  # scripted group (container) (typed FeaturePython)
  Dunit = g/cm3
  Dvalue = 8.57
  Group = -> [Nb_element001]
  conduct = 2
  density = 1
  expand = 3
  formula = Nb
  name = G4_Nb
  specific = 4
FEATURE [App::DocumentObjectGroupPython] Mo_element001  label="Mo_element : 1"  # scripted group (container) (typed FeaturePython)
  n = 1
  ref = Mo_element
FEATURE [App::DocumentObjectGroupPython] G4_Mo  # scripted group (container) (typed FeaturePython)
  Dunit = g/cm3
  Dvalue = 10.22
  Group = -> [Mo_element001]
  conduct = 2
  density = 1
  expand = 3
  formula = Mo
  name = G4_Mo
  specific = 4
FEATURE [App::DocumentObjectGroupPython] Tc_element001  label="Tc_element : 1"  # scripted group (container) (typed FeaturePython)
  n = 1
  ref = Tc_element
FEATURE [App::DocumentObjectGroupPython] G4_Tc  # scripted group (container) (typed FeaturePython)
  Dunit = g/cm3
  Dvalue = 11.5
  Group = -> [Tc_element001]
  conduct = 2
  density = 1
  expand = 3
  formula = Tc
  name = G4_Tc
  specific = 4
FEATURE [App::DocumentObjectGroupPython] Ru_element001  label="Ru_element : 1"  # scripted group (container) (typed FeaturePython)
  n = 1
  ref = Ru_element
FEATURE [App::DocumentObjectGroupPython] G4_Ru  # scripted group (container) (typed FeaturePython)
  Dunit = g/cm3
  Dvalue = 12.41
  Group = -> [Ru_element001]
  conduct = 2
  density = 1
  expand = 3
  formula = Ru
  name = G4_Ru
  specific = 4
FEATURE [App::DocumentObjectGroupPython] Rh_element001  label="Rh_element : 1"  # scripted group (container) (typed FeaturePython)
  n = 1
  ref = Rh_element
FEATURE [App::DocumentObjectGroupPython] G4_Rh  # scripted group (container) (typed FeaturePython)
  Dunit = g/cm3
  Dvalue = 12.41
  Group = -> [Rh_element001]
  conduct = 2
  density = 1
  expand = 3
  formula = Rh
  name = G4_Rh
  specific = 4
FEATURE [App::DocumentObjectGroupPython] Pd_element001  label="Pd_element : 1"  # scripted group (container) (typed FeaturePython)
  n = 1
  ref = Pd_element
FEATURE [App::DocumentObjectGroupPython] G4_Pd  # scripted group (container) (typed FeaturePython)
  Dunit = g/cm3
  Dvalue = 12.02
  Group = -> [Pd_element001]
  conduct = 2
  density = 1
  expand = 3
  formula = Pd
  name = G4_Pd
  specific = 4
FEATURE [App::DocumentObjectGroupPython] Ag_element006  label="Ag_element : 004"  # scripted group (container) (typed FeaturePython)
  n = 1
  ref = Ag_element
FEATURE [App::DocumentObjectGroupPython] G4_Ag  # scripted group (container) (typed FeaturePython)
  Dunit = g/cm3
  Dvalue = 10.5
  Group = -> [Ag_element006]
  conduct = 2
  density = 1
  expand = 3
  formula = Ag
  name = G4_Ag
  specific = 4
FEATURE [App::DocumentObjectGroupPython] Cd_element003  label="Cd_element : 003"  # scripted group (container) (typed FeaturePython)
  n = 1
  ref = Cd_element
FEATURE [App::DocumentObjectGroupPython] G4_Cd  # scripted group (container) (typed FeaturePython)
  Dunit = g/cm3
  Dvalue = 8.65
  Group = -> [Cd_element003]
  conduct = 2
  density = 1
  expand = 3
  formula = Cd
  name = G4_Cd
  specific = 4
FEATURE [App::DocumentObjectGroupPython] In_element001  label="In_element : 1"  # scripted group (container) (typed FeaturePython)
  n = 1
  ref = In_element
FEATURE [App::DocumentObjectGroupPython] G4_In  # scripted group (container) (typed FeaturePython)
  Dunit = g/cm3
  Dvalue = 7.31
  Group = -> [In_element001]
  conduct = 2
  density = 1
  expand = 3
  formula = In
  name = G4_In
  specific = 4
FEATURE [App::DocumentObjectGroupPython] Sn_element001  label="Sn_element : 1"  # scripted group (container) (typed FeaturePython)
  n = 1
  ref = Sn_element
FEATURE [App::DocumentObjectGroupPython] G4_Sn  # scripted group (container) (typed FeaturePython)
  Dunit = g/cm3
  Dvalue = 7.31
  Group = -> [Sn_element001]
  conduct = 2
  density = 1
  expand = 3
  formula = Sn
  name = G4_Sn
  specific = 4
FEATURE [App::DocumentObjectGroupPython] Sb_element001  label="Sb_element : 1"  # scripted group (container) (typed FeaturePython)
  n = 1
  ref = Sb_element
FEATURE [App::DocumentObjectGroupPython] G4_Sb  # scripted group (container) (typed FeaturePython)
  Dunit = g/cm3
  Dvalue = 6.691
  Group = -> [Sb_element001]
  conduct = 2
  density = 1
  expand = 3
  formula = Sb
  name = G4_Sb
  specific = 4
FEATURE [App::DocumentObjectGroupPython] Te_element002  label="Te_element : 002"  # scripted group (container) (typed FeaturePython)
  n = 1
  ref = Te_element
FEATURE [App::DocumentObjectGroupPython] G4_Te  # scripted group (container) (typed FeaturePython)
  Dunit = g/cm3
  Dvalue = 6.24
  Group = -> [Te_element002]
  conduct = 2
  density = 1
  expand = 3
  formula = Te
  name = G4_Te
  specific = 4
FEATURE [App::DocumentObjectGroupPython] I_element010  label="I_element : 006"  # scripted group (container) (typed FeaturePython)
  n = 1
  ref = I_element
FEATURE [App::DocumentObjectGroupPython] G4_I  # scripted group (container) (typed FeaturePython)
  Dunit = g/cm3
  Dvalue = 4.93
  Group = -> [I_element010]
  conduct = 2
  density = 1
  expand = 3
  formula = I
  name = G4_I
  specific = 4
FEATURE [App::DocumentObjectGroupPython] Xe_element001  label="Xe_element : 1"  # scripted group (container) (typed FeaturePython)
  n = 1
  ref = Xe_element
FEATURE [App::DocumentObjectGroupPython] G4_Xe  # scripted group (container) (typed FeaturePython)
  Dunit = g/cm3
  Dvalue = 0.00548536
  Group = -> [Xe_element001]
  conduct = 2
  density = 1
  expand = 3
  formula = Xe
  name = G4_Xe
  specific = 4
FEATURE [App::DocumentObjectGroupPython] Cs_element003  label="Cs_element : 003"  # scripted group (container) (typed FeaturePython)
  n = 1
  ref = Cs_element
FEATURE [App::DocumentObjectGroupPython] G4_Cs  # scripted group (container) (typed FeaturePython)
  Dunit = g/cm3
  Dvalue = 1.873
  Group = -> [Cs_element003]
  conduct = 2
  density = 1
  expand = 3
  formula = Cs
  name = G4_Cs
  specific = 4
FEATURE [App::DocumentObjectGroupPython] Ba_element003  label="Ba_element : 003"  # scripted group (container) (typed FeaturePython)
  n = 1
  ref = Ba_element
FEATURE [App::DocumentObjectGroupPython] G4_Ba  # scripted group (container) (typed FeaturePython)
  Dunit = g/cm3
  Dvalue = 3.5
  Group = -> [Ba_element003]
  conduct = 2
  density = 1
  expand = 3
  formula = Ba
  name = G4_Ba
  specific = 4
FEATURE [App::DocumentObjectGroupPython] La_element003  label="La_element : 003"  # scripted group (container) (typed FeaturePython)
  n = 1
  ref = La_element
FEATURE [App::DocumentObjectGroupPython] G4_La  # scripted group (container) (typed FeaturePython)
  Dunit = g/cm3
  Dvalue = 6.154
  Group = -> [La_element003]
  conduct = 2
  density = 1
  expand = 3
  formula = La
  name = G4_La
  specific = 4
FEATURE [App::DocumentObjectGroupPython] Ce_element002  label="Ce_element : 1"  # scripted group (container) (typed FeaturePython)
  n = 1
  ref = Ce_element
FEATURE [App::DocumentObjectGroupPython] G4_Ce  # scripted group (container) (typed FeaturePython)
  Dunit = g/cm3
  Dvalue = 6.657
  Group = -> [Ce_element002]
  conduct = 2
  density = 1
  expand = 3
  formula = Ce
  name = G4_Ce
  specific = 4
FEATURE [App::DocumentObjectGroupPython] Pr_element001  label="Pr_element : 1"  # scripted group (container) (typed FeaturePython)
  n = 1
  ref = Pr_element
FEATURE [App::DocumentObjectGroupPython] G4_Pr  # scripted group (container) (typed FeaturePython)
  Dunit = g/cm3
  Dvalue = 6.71
  Group = -> [Pr_element001]
  conduct = 2
  density = 1
  expand = 3
  formula = Pr
  name = G4_Pr
  specific = 4
FEATURE [App::DocumentObjectGroupPython] Nd_element001  label="Nd_element : 1"  # scripted group (container) (typed FeaturePython)
  n = 1
  ref = Nd_element
FEATURE [App::DocumentObjectGroupPython] G4_Nd  # scripted group (container) (typed FeaturePython)
  Dunit = g/cm3
  Dvalue = 6.9
  Group = -> [Nd_element001]
  conduct = 2
  density = 1
  expand = 3
  formula = Nd
  name = G4_Nd
  specific = 4
FEATURE [App::DocumentObjectGroupPython] Pm_element001  label="Pm_element : 1"  # scripted group (container) (typed FeaturePython)
  n = 1
  ref = Pm_element
FEATURE [App::DocumentObjectGroupPython] G4_Pm  # scripted group (container) (typed FeaturePython)
  Dunit = g/cm3
  Dvalue = 7.22
  Group = -> [Pm_element001]
  conduct = 2
  density = 1
  expand = 3
  formula = Pm
  name = G4_Pm
  specific = 4
FEATURE [App::DocumentObjectGroupPython] Sm_element001  label="Sm_element : 1"  # scripted group (container) (typed FeaturePython)
  n = 1
  ref = Sm_element
FEATURE [App::DocumentObjectGroupPython] G4_Sm  # scripted group (container) (typed FeaturePython)
  Dunit = g/cm3
  Dvalue = 7.46
  Group = -> [Sm_element001]
  conduct = 2
  density = 1
  expand = 3
  formula = Sm
  name = G4_Sm
  specific = 4
FEATURE [App::DocumentObjectGroupPython] Eu_element001  label="Eu_element : 1"  # scripted group (container) (typed FeaturePython)
  n = 1
  ref = Eu_element
FEATURE [App::DocumentObjectGroupPython] G4_Eu  # scripted group (container) (typed FeaturePython)
  Dunit = g/cm3
  Dvalue = 5.243
  Group = -> [Eu_element001]
  conduct = 2
  density = 1
  expand = 3
  formula = Eu
  name = G4_Eu
  specific = 4
FEATURE [App::DocumentObjectGroupPython] Gd_element002  label="Gd_element : 1"  # scripted group (container) (typed FeaturePython)
  n = 1
  ref = Gd_element
FEATURE [App::DocumentObjectGroupPython] G4_Gd  # scripted group (container) (typed FeaturePython)
  Dunit = g/cm3
  Dvalue = 7.9004
  Group = -> [Gd_element002]
  conduct = 2
  density = 1
  expand = 3
  formula = Gd
  name = G4_Gd
  specific = 4
FEATURE [App::DocumentObjectGroupPython] Tb_element001  label="Tb_element : 1"  # scripted group (container) (typed FeaturePython)
  n = 1
  ref = Tb_element
FEATURE [App::DocumentObjectGroupPython] G4_Tb  # scripted group (container) (typed FeaturePython)
  Dunit = g/cm3
  Dvalue = 8.229
  Group = -> [Tb_element001]
  conduct = 2
  density = 1
  expand = 3
  formula = Tb
  name = G4_Tb
  specific = 4
FEATURE [App::DocumentObjectGroupPython] Dy_element001  label="Dy_element : 1"  # scripted group (container) (typed FeaturePython)
  n = 1
  ref = Dy_element
FEATURE [App::DocumentObjectGroupPython] G4_Dy  # scripted group (container) (typed FeaturePython)
  Dunit = g/cm3
  Dvalue = 8.55
  Group = -> [Dy_element001]
  conduct = 2
  density = 1
  expand = 3
  formula = Dy
  name = G4_Dy
  specific = 4
FEATURE [App::DocumentObjectGroupPython] Ho_element001  label="Ho_element : 1"  # scripted group (container) (typed FeaturePython)
  n = 1
  ref = Ho_element
FEATURE [App::DocumentObjectGroupPython] G4_Ho  # scripted group (container) (typed FeaturePython)
  Dunit = g/cm3
  Dvalue = 8.795
  Group = -> [Ho_element001]
  conduct = 2
  density = 1
  expand = 3
  formula = Ho
  name = G4_Ho
  specific = 4
FEATURE [App::DocumentObjectGroupPython] Er_element001  label="Er_element : 1"  # scripted group (container) (typed FeaturePython)
  n = 1
  ref = Er_element
FEATURE [App::DocumentObjectGroupPython] G4_Er  # scripted group (container) (typed FeaturePython)
  Dunit = g/cm3
  Dvalue = 9.066
  Group = -> [Er_element001]
  conduct = 2
  density = 1
  expand = 3
  formula = Er
  name = G4_Er
  specific = 4
FEATURE [App::DocumentObjectGroupPython] Tm_element001  label="Tm_element : 1"  # scripted group (container) (typed FeaturePython)
  n = 1
  ref = Tm_element
FEATURE [App::DocumentObjectGroupPython] G4_Tm  # scripted group (container) (typed FeaturePython)
  Dunit = g/cm3
  Dvalue = 9.321
  Group = -> [Tm_element001]
  conduct = 2
  density = 1
  expand = 3
  formula = Tm
  name = G4_Tm
  specific = 4
FEATURE [App::DocumentObjectGroupPython] Yb_element001  label="Yb_element : 1"  # scripted group (container) (typed FeaturePython)
  n = 1
  ref = Yb_element
FEATURE [App::DocumentObjectGroupPython] G4_Yb  # scripted group (container) (typed FeaturePython)
  Dunit = g/cm3
  Dvalue = 6.73
  Group = -> [Yb_element001]
  conduct = 2
  density = 1
  expand = 3
  formula = Yb
  name = G4_Yb
  specific = 4
FEATURE [App::DocumentObjectGroupPython] Lu_element001  label="Lu_element : 1"  # scripted group (container) (typed FeaturePython)
  n = 1
  ref = Lu_element
FEATURE [App::DocumentObjectGroupPython] G4_Lu  # scripted group (container) (typed FeaturePython)
  Dunit = g/cm3
  Dvalue = 9.84
  Group = -> [Lu_element001]
  conduct = 2
  density = 1
  expand = 3
  formula = Lu
  name = G4_Lu
  specific = 4
FEATURE [App::DocumentObjectGroupPython] Hf_element001  label="Hf_element : 1"  # scripted group (container) (typed FeaturePython)
  n = 1
  ref = Hf_element
FEATURE [App::DocumentObjectGroupPython] G4_Hf  # scripted group (container) (typed FeaturePython)
  Dunit = g/cm3
  Dvalue = 13.31
  Group = -> [Hf_element001]
  conduct = 2
  density = 1
  expand = 3
  formula = Hf
  name = G4_Hf
  specific = 4
FEATURE [App::DocumentObjectGroupPython] Ta_element001  label="Ta_element : 1"  # scripted group (container) (typed FeaturePython)
  n = 1
  ref = Ta_element
FEATURE [App::DocumentObjectGroupPython] G4_Ta  # scripted group (container) (typed FeaturePython)
  Dunit = g/cm3
  Dvalue = 16.654
  Group = -> [Ta_element001]
  conduct = 2
  density = 1
  expand = 3
  formula = Ta
  name = G4_Ta
  specific = 4
FEATURE [App::DocumentObjectGroupPython] W_element004  label="W_element : 004"  # scripted group (container) (typed FeaturePython)
  n = 1
  ref = W_element
FEATURE [App::DocumentObjectGroupPython] G4_W  # scripted group (container) (typed FeaturePython)
  Dunit = g/cm3
  Dvalue = 19.3
  Group = -> [W_element004]
  conduct = 2
  density = 1
  expand = 3
  formula = W
  name = G4_W
  specific = 4
FEATURE [App::DocumentObjectGroupPython] Re_element001  label="Re_element : 1"  # scripted group (container) (typed FeaturePython)
  n = 1
  ref = Re_element
FEATURE [App::DocumentObjectGroupPython] G4_Re  # scripted group (container) (typed FeaturePython)
  Dunit = g/cm3
  Dvalue = 21.02
  Group = -> [Re_element001]
  conduct = 2
  density = 1
  expand = 3
  formula = Re
  name = G4_Re
  specific = 4
FEATURE [App::DocumentObjectGroupPython] Os_element001  label="Os_element : 1"  # scripted group (container) (typed FeaturePython)
  n = 1
  ref = Os_element
FEATURE [App::DocumentObjectGroupPython] G4_Os  # scripted group (container) (typed FeaturePython)
  Dunit = g/cm3
  Dvalue = 22.57
  Group = -> [Os_element001]
  conduct = 2
  density = 1
  expand = 3
  formula = Os
  name = G4_Os
  specific = 4
FEATURE [App::DocumentObjectGroupPython] Ir_element001  label="Ir_element : 1"  # scripted group (container) (typed FeaturePython)
  n = 1
  ref = Ir_element
FEATURE [App::DocumentObjectGroupPython] G4_Ir  # scripted group (container) (typed FeaturePython)
  Dunit = g/cm3
  Dvalue = 22.42
  Group = -> [Ir_element001]
  conduct = 2
  density = 1
  expand = 3
  formula = Ir
  name = G4_Ir
  specific = 4
FEATURE [App::DocumentObjectGroupPython] Pt_element001  label="Pt_element : 1"  # scripted group (container) (typed FeaturePython)
  n = 1
  ref = Pt_element
FEATURE [App::DocumentObjectGroupPython] G4_Pt  # scripted group (container) (typed FeaturePython)
  Dunit = g/cm3
  Dvalue = 21.45
  Group = -> [Pt_element001]
  conduct = 2
  density = 1
  expand = 3
  formula = Pt
  name = G4_Pt
  specific = 4
FEATURE [App::DocumentObjectGroupPython] Au_element001  label="Au_element : 1"  # scripted group (container) (typed FeaturePython)
  n = 1
  ref = Au_element
FEATURE [App::DocumentObjectGroupPython] G4_Au  # scripted group (container) (typed FeaturePython)
  Dunit = g/cm3
  Dvalue = 19.32
  Group = -> [Au_element001]
  conduct = 2
  density = 1
  expand = 3
  formula = Au
  name = G4_Au
  specific = 4
FEATURE [App::DocumentObjectGroupPython] Hg_element002  label="Hg_element : 002"  # scripted group (container) (typed FeaturePython)
  n = 1
  ref = Hg_element
FEATURE [App::DocumentObjectGroupPython] G4_Hg  # scripted group (container) (typed FeaturePython)
  Dunit = g/cm3
  Dvalue = 13.546
  Group = -> [Hg_element002]
  conduct = 2
  density = 1
  expand = 3
  formula = Hg
  name = G4_Hg
  specific = 4
FEATURE [App::DocumentObjectGroupPython] Tl_element002  label="Tl_element : 002"  # scripted group (container) (typed FeaturePython)
  n = 1
  ref = Tl_element
FEATURE [App::DocumentObjectGroupPython] G4_Tl  # scripted group (container) (typed FeaturePython)
  Dunit = g/cm3
  Dvalue = 11.72
  Group = -> [Tl_element002]
  conduct = 2
  density = 1
  expand = 3
  formula = Tl
  name = G4_Tl
  specific = 4
FEATURE [App::DocumentObjectGroupPython] Pb_element003  label="Pb_element : 1"  # scripted group (container) (typed FeaturePython)
  n = 1
  ref = Pb_element
FEATURE [App::DocumentObjectGroupPython] G4_Pb  # scripted group (container) (typed FeaturePython)
  Dunit = g/cm3
  Dvalue = 11.35
  Group = -> [Pb_element003]
  conduct = 2
  density = 1
  expand = 3
  formula = Pb
  name = G4_Pb
  specific = 4
FEATURE [App::DocumentObjectGroupPython] Bi_element002  label="Bi_element : 1"  # scripted group (container) (typed FeaturePython)
  n = 1
  ref = Bi_element
FEATURE [App::DocumentObjectGroupPython] G4_Bi  # scripted group (container) (typed FeaturePython)
  Dunit = g/cm3
  Dvalue = 9.747
  Group = -> [Bi_element002]
  conduct = 2
  density = 1
  expand = 3
  formula = Bi
  name = G4_Bi
  specific = 4
FEATURE [App::DocumentObjectGroupPython] Po_element001  label="Po_element : 1"  # scripted group (container) (typed FeaturePython)
  n = 1
  ref = Po_element
FEATURE [App::DocumentObjectGroupPython] G4_Po  # scripted group (container) (typed FeaturePython)
  Dunit = g/cm3
  Dvalue = 9.32
  Group = -> [Po_element001]
  conduct = 2
  density = 1
  expand = 3
  formula = Po
  name = G4_Po
  specific = 4
FEATURE [App::DocumentObjectGroupPython] At_element001  label="At_element : 1"  # scripted group (container) (typed FeaturePython)
  n = 1
  ref = At_element
FEATURE [App::DocumentObjectGroupPython] G4_At  # scripted group (container) (typed FeaturePython)
  Dunit = g/cm3
  Dvalue = 9.32
  Group = -> [At_element001]
  conduct = 2
  density = 1
  expand = 3
  formula = At
  name = G4_At
  specific = 4
FEATURE [App::DocumentObjectGroupPython] Rn_element001  label="Rn_element : 1"  # scripted group (container) (typed FeaturePython)
  n = 1
  ref = Rn_element
FEATURE [App::DocumentObjectGroupPython] G4_Rn  # scripted group (container) (typed FeaturePython)
  Dunit = g/cm3
  Dvalue = 0.00900662
  Group = -> [Rn_element001]
  conduct = 2
  density = 1
  expand = 3
  formula = Rn
  name = G4_Rn
  specific = 4
FEATURE [App::DocumentObjectGroupPython] Fr_element001  label="Fr_element : 1"  # scripted group (container) (typed FeaturePython)
  n = 1
  ref = Fr_element
FEATURE [App::DocumentObjectGroupPython] G4_Fr  # scripted group (container) (typed FeaturePython)
  Dunit = g/cm3
  Dvalue = 1
  Group = -> [Fr_element001]
  conduct = 2
  density = 1
  expand = 3
  formula = Fr
  name = G4_Fr
  specific = 4
FEATURE [App::DocumentObjectGroupPython] Ra_element001  label="Ra_element : 1"  # scripted group (container) (typed FeaturePython)
  n = 1
  ref = Ra_element
FEATURE [App::DocumentObjectGroupPython] G4_Ra  # scripted group (container) (typed FeaturePython)
  Dunit = g/cm3
  Dvalue = 5
  Group = -> [Ra_element001]
  conduct = 2
  density = 1
  expand = 3
  formula = Ra
  name = G4_Ra
  specific = 4
FEATURE [App::DocumentObjectGroupPython] Ac_element001  label="Ac_element : 1"  # scripted group (container) (typed FeaturePython)
  n = 1
  ref = Ac_element
FEATURE [App::DocumentObjectGroupPython] G4_Ac  # scripted group (container) (typed FeaturePython)
  Dunit = g/cm3
  Dvalue = 10.07
  Group = -> [Ac_element001]
  conduct = 2
  density = 1
  expand = 3
  formula = Ac
  name = G4_Ac
  specific = 4
FEATURE [App::DocumentObjectGroupPython] Th_element001  label="Th_element : 1"  # scripted group (container) (typed FeaturePython)
  n = 1
  ref = Th_element
FEATURE [App::DocumentObjectGroupPython] G4_Th  # scripted group (container) (typed FeaturePython)
  Dunit = g/cm3
  Dvalue = 11.72
  Group = -> [Th_element001]
  conduct = 2
  density = 1
  expand = 3
  formula = Th
  name = G4_Th
  specific = 4
FEATURE [App::DocumentObjectGroupPython] Pa_element001  label="Pa_element : 1"  # scripted group (container) (typed FeaturePython)
  n = 1
  ref = Pa_element
FEATURE [App::DocumentObjectGroupPython] G4_Pa  # scripted group (container) (typed FeaturePython)
  Dunit = g/cm3
  Dvalue = 15.37
  Group = -> [Pa_element001]
  conduct = 2
  density = 1
  expand = 3
  formula = Pa
  name = G4_Pa
  specific = 4
FEATURE [App::DocumentObjectGroupPython] U_element004  label="U_element : 004"  # scripted group (container) (typed FeaturePython)
  n = 1
  ref = U_element
FEATURE [App::DocumentObjectGroupPython] G4_U  # scripted group (container) (typed FeaturePython)
  Dunit = g/cm3
  Dvalue = 18.95
  Group = -> [U_element004]
  conduct = 2
  density = 1
  expand = 3
  formula = U
  name = G4_U
  specific = 4
FEATURE [App::DocumentObjectGroupPython] Np_element001  label="Np_element : 1"  # scripted group (container) (typed FeaturePython)
  n = 1
  ref = Np_element
FEATURE [App::DocumentObjectGroupPython] G4_Np  # scripted group (container) (typed FeaturePython)
  Dunit = g/cm3
  Dvalue = 20.25
  Group = -> [Np_element001]
  conduct = 2
  density = 1
  expand = 3
  formula = Np
  name = G4_Np
  specific = 4
FEATURE [App::DocumentObjectGroupPython] Pu_element002  label="Pu_element : 002"  # scripted group (container) (typed FeaturePython)
  n = 1
  ref = Pu_element
FEATURE [App::DocumentObjectGroupPython] G4_Pu  # scripted group (container) (typed FeaturePython)
  Dunit = g/cm3
  Dvalue = 19.84
  Group = -> [Pu_element002]
  conduct = 2
  density = 1
  expand = 3
  formula = Pu
  name = G4_Pu
  specific = 4
FEATURE [App::DocumentObjectGroupPython] Am_element001  label="Am_element : 1"  # scripted group (container) (typed FeaturePython)
  n = 1
  ref = Am_element
FEATURE [App::DocumentObjectGroupPython] G4_Am  # scripted group (container) (typed FeaturePython)
  Dunit = g/cm3
  Dvalue = 13.67
  Group = -> [Am_element001]
  conduct = 2
  density = 1
  expand = 3
  formula = Am
  name = G4_Am
  specific = 4
FEATURE [App::DocumentObjectGroupPython] Cm_element001  label="Cm_element : 1"  # scripted group (container) (typed FeaturePython)
  n = 1
  ref = Cm_element
FEATURE [App::DocumentObjectGroupPython] G4_Cm  # scripted group (container) (typed FeaturePython)
  Dunit = g/cm3
  Dvalue = 13.51
  Group = -> [Cm_element001]
  conduct = 2
  density = 1
  expand = 3
  formula = Cm
  name = G4_Cm
  specific = 4
FEATURE [App::DocumentObjectGroupPython] Bk_element001  label="Bk_element : 1"  # scripted group (container) (typed FeaturePython)
  n = 1
  ref = Bk_element
FEATURE [App::DocumentObjectGroupPython] G4_Bk  # scripted group (container) (typed FeaturePython)
  Dunit = g/cm3
  Dvalue = 14
  Group = -> [Bk_element001]
  conduct = 2
  density = 1
  expand = 3
  formula = Bk
  name = G4_Bk
  specific = 4
FEATURE [App::DocumentObjectGroupPython] Cf_element001  label="Cf_element : 1"  # scripted group (container) (typed FeaturePython)
  n = 1
  ref = Cf_element
FEATURE [App::DocumentObjectGroupPython] G4_Cf  # scripted group (container) (typed FeaturePython)
  Dunit = g/cm3
  Dvalue = 10
  Group = -> [Cf_element001]
  conduct = 2
  density = 1
  expand = 3
  formula = Cf
  name = G4_Cf
  specific = 4
FEATURE [App::DocumentObjectGroupPython] Element  # scripted group (container) (typed FeaturePython)
  Group = -> [G4_H,G4_He,G4_Li,G4_Be,G4_B,G4_C,G4_N,G4_O,G4_F,G4_Ne,G4_Na,G4_Mg,G4_Al,G4_Si,G4_P,G4_S,G4_Cl,G4_Ar,G4_K,G4_Ca,G4_Sc,G4_Ti,G4_V,G4_Cr,G4_Mn,G4_Fe,G4_Co,G4_Ni,G4_Cu,G4_Zn,G4_Ga,G4_Ge,G4_As,G4_Se,G4_Br,G4_Kr,G4_Rb,G4_Sr,G4_Y,G4_Zr,G4_Nb,G4_Mo,G4_Tc,G4_Ru,G4_Rh,G4_Pd,G4_Ag,G4_Cd,G4_In,G4_Sn,G4_Sb,G4_Te,G4_I,G4_Xe,G4_Cs,G4_Ba,G4_La,G4_Ce,G4_Pr,G4_Nd,G4_Pm,G4_Sm,G4_Eu,G4_Gd,G4_Tb,G4_Dy,G4_Ho,G4_Er,+30 more]
FEATURE [App::DocumentObjectGroupPython] H_element114  label="H_element : 063"  # scripted group (container) (typed FeaturePython)
  n = 2
  ref = H_element
FEATURE [App::DocumentObjectGroupPython] G4_lH2  # scripted group (container) (typed FeaturePython)
  Dunit = g/cm3
  Dvalue = 0.0708
  Group = -> [H_element114]
  conduct = 2
  density = 1
  expand = 3
  formula = G4_lH2
  name = G4_lH2
  specific = 4
FEATURE [App::DocumentObjectGroupPython] N_element049  label="N_element : 022"  # scripted group (container) (typed FeaturePython)
  n = 2
  ref = N_element
FEATURE [App::DocumentObjectGroupPython] G4_lN2  # scripted group (container) (typed FeaturePython)
  Dunit = g/cm3
  Dvalue = 0.807
  Group = -> [N_element049]
  conduct = 2
  density = 1
  expand = 3
  formula = G4_lN2
  name = G4_lN2
  specific = 4
FEATURE [App::DocumentObjectGroupPython] O_element106  label="O_element : 060"  # scripted group (container) (typed FeaturePython)
  n = 2
  ref = O_element
FEATURE [App::DocumentObjectGroupPython] G4_lO2  # scripted group (container) (typed FeaturePython)
  Dunit = g/cm3
  Dvalue = 1.141
  Group = -> [O_element106]
  conduct = 2
  density = 1
  expand = 3
  formula = G4_lO2
  name = G4_lO2
  specific = 4
FEATURE [App::DocumentObjectGroupPython] Ar  label="Ar : 1"  # scripted group (container) (typed FeaturePython)
  n = 1
  ref = Ar
FEATURE [App::DocumentObjectGroupPython] G4_lAr  # scripted group (container) (typed FeaturePython)
  Dunit = g/cm3
  Dvalue = 1.396
  Group = -> [Ar]
  conduct = 2
  density = 1
  expand = 3
  formula = G4_lAr
  name = G4_lAr
  specific = 4
FEATURE [App::DocumentObjectGroupPython] Br  label="Br : 1"  # scripted group (container) (typed FeaturePython)
  n = 1
  ref = Br
FEATURE [App::DocumentObjectGroupPython] G4_lBr  # scripted group (container) (typed FeaturePython)
  Dunit = g/cm3
  Dvalue = 3.1028
  Group = -> [Br]
  conduct = 2
  density = 1
  expand = 3
  formula = G4_lBr
  name = G4_lBr
  specific = 4
FEATURE [App::DocumentObjectGroupPython] Kr  label="Kr : 1"  # scripted group (container) (typed FeaturePython)
  n = 1
  ref = Kr
FEATURE [App::DocumentObjectGroupPython] G4_lKr  # scripted group (container) (typed FeaturePython)
  Dunit = g/cm3
  Dvalue = 2.418
  Group = -> [Kr]
  conduct = 2
  density = 1
  expand = 3
  formula = G4_lKr
  name = G4_lKr
  specific = 4
FEATURE [App::DocumentObjectGroupPython] Xe  label="Xe : 1"  # scripted group (container) (typed FeaturePython)
  n = 1
  ref = Xe
FEATURE [App::DocumentObjectGroupPython] G4_lXe  # scripted group (container) (typed FeaturePython)
  Dunit = g/cm3
  Dvalue = 2.953
  Group = -> [Xe]
  conduct = 2
  density = 1
  expand = 3
  formula = G4_lXe
  name = G4_lXe
  specific = 4
FEATURE [App::DocumentObjectGroupPython] O_element107  label="O_element : 061"  # scripted group (container) (typed FeaturePython)
  n = 4
  ref = O_element
FEATURE [App::DocumentObjectGroupPython] Pb_element004  label="Pb_element : 002"  # scripted group (container) (typed FeaturePython)
  n = 1
  ref = Pb_element
FEATURE [App::DocumentObjectGroupPython] W_element005  label="W_element : 005"  # scripted group (container) (typed FeaturePython)
  n = 1
  ref = W_element
FEATURE [App::DocumentObjectGroupPython] G4_PbWO4  # scripted group (container) (typed FeaturePython)
  Dunit = g/cm3
  Dvalue = 8.28
  Group = -> [O_element107,Pb_element004,W_element005]
  conduct = 2
  density = 1
  expand = 3
  formula = G4_PbWO4
  name = G4_PbWO4
  specific = 4
FEATURE [App::DocumentObjectGroupPython] alactic  label="alactic : 1"  # scripted group (container) (typed FeaturePython)
  n = 1
  ref = alactic
FEATURE [App::DocumentObjectGroupPython] G4_Galactic  # scripted group (container) (typed FeaturePython)
  Dunit = g/cm3
  Dvalue = 0
  Group = -> [alactic]
  conduct = 2
  density = 1
  expand = 3
  formula = G4_Galactic
  name = G4_Galactic
  specific = 4
FEATURE [App::DocumentObjectGroupPython] RAPHITE_POROUS  label="RAPHITE_POROUS : 1"  # scripted group (container) (typed FeaturePython)
  n = 1
  ref = RAPHITE_POROUS
FEATURE [App::DocumentObjectGroupPython] G4_GRAPHITE_POROUS  # scripted group (container) (typed FeaturePython)
  Dunit = g/cm3
  Dvalue = 1.7
  Group = -> [RAPHITE_POROUS]
  conduct = 2
  density = 1
  expand = 3
  formula = G4_GRAPHITE_POROUS
  name = G4_GRAPHITE_POROUS
  specific = 4
FEATURE [App::DocumentObjectGroupPython] H_element115  label="H_element : 0.150"  # scripted group (container) (typed FeaturePython)
  n = 0.080538
FEATURE [App::DocumentObjectGroupPython] C_element125  label="C_element : 0.600"  # scripted group (container) (typed FeaturePython)
  n = 0.599848
FEATURE [App::DocumentObjectGroupPython] O_element108  label="O_element : 0.320"  # scripted group (container) (typed FeaturePython)
  n = 0.319614
FEATURE [App::DocumentObjectGroupPython] G4_LUCITE  # scripted group (container) (typed FeaturePython)
  Dunit = g/cm3
  Dvalue = 1.19
  Group = -> [H_element115,C_element125,O_element108]
  conduct = 2
  density = 1
  expand = 3
  formula = G4_LUCITE
  name = G4_LUCITE
  specific = 4
FEATURE [App::DocumentObjectGroupPython] Cu_element002  label="Cu_element : 62"  # scripted group (container) (typed FeaturePython)
  n = 62
  ref = Cu_element
FEATURE [App::DocumentObjectGroupPython] Zn_element002  label="Zn_element : 35"  # scripted group (container) (typed FeaturePython)
  n = 35
  ref = Zn_element
FEATURE [App::DocumentObjectGroupPython] Pb_element005  label="Pb_element : 3"  # scripted group (container) (typed FeaturePython)
  n = 3
  ref = Pb_element
FEATURE [App::DocumentObjectGroupPython] G4_BRASS  # scripted group (container) (typed FeaturePython)
  Dunit = g/cm3
  Dvalue = 8.52
  Group = -> [Cu_element002,Zn_element002,Pb_element005]
  conduct = 2
  density = 1
  expand = 3
  formula = G4_BRASS
  name = G4_BRASS
  specific = 4
FEATURE [App::DocumentObjectGroupPython] Cu_element003  label="Cu_element : 89"  # scripted group (container) (typed FeaturePython)
  n = 89
  ref = Cu_element
FEATURE [App::DocumentObjectGroupPython] Zn_element003  label="Zn_element : 9"  # scripted group (container) (typed FeaturePython)
  n = 9
  ref = Zn_element
FEATURE [App::DocumentObjectGroupPython] Pb_element006  label="Pb_element : 2"  # scripted group (container) (typed FeaturePython)
  n = 2
  ref = Pb_element
FEATURE [App::DocumentObjectGroupPython] G4_BRONZE  # scripted group (container) (typed FeaturePython)
  Dunit = g/cm3
  Dvalue = 8.82
  Group = -> [Cu_element003,Zn_element003,Pb_element006]
  conduct = 2
  density = 1
  expand = 3
  formula = G4_BRONZE
  name = G4_BRONZE
  specific = 4
FEATURE [App::DocumentObjectGroupPython] Fe_element008  label="Fe_element : 74"  # scripted group (container) (typed FeaturePython)
  n = 74
  ref = Fe_element
FEATURE [App::DocumentObjectGroupPython] Cr_element002  label="Cr_element : 18"  # scripted group (container) (typed FeaturePython)
  n = 18
  ref = Cr_element
FEATURE [App::DocumentObjectGroupPython] Ni_element002  label="Ni_element : 8"  # scripted group (container) (typed FeaturePython)
  n = 8
  ref = Ni_element
FEATURE [App::DocumentObjectGroupPython] G4_STAINLESS_STEEL  label="G4_STAINLESS-STEEL"  # scripted group (container) (typed FeaturePython)
  Dunit = g/cm3
  Dvalue = 8
  Group = -> [Fe_element008,Cr_element002,Ni_element002]
  conduct = 2
  density = 1
  expand = 3
  formula = G4_STAINLESS-STEEL
  name = G4_STAINLESS-STEEL
  specific = 4
FEATURE [App::DocumentObjectGroupPython] H_element116  label="H_element : 064"  # scripted group (container) (typed FeaturePython)
  n = 18
  ref = H_element
FEATURE [App::DocumentObjectGroupPython] C_element126  label="C_element : 071"  # scripted group (container) (typed FeaturePython)
  n = 12
  ref = C_element
FEATURE [App::DocumentObjectGroupPython] O_element109  label="O_element : 062"  # scripted group (container) (typed FeaturePython)
  n = 7
  ref = O_element
FEATURE [App::DocumentObjectGroupPython] G4_CR39  # scripted group (container) (typed FeaturePython)
  Dunit = g/cm3
  Dvalue = 1.32
  Group = -> [H_element116,C_element126,O_element109]
  conduct = 2
  density = 1
  expand = 3
  formula = G4_CR39
  name = G4_CR39
  specific = 4
FEATURE [App::DocumentObjectGroupPython] H_element117  label="H_element : 38"  # scripted group (container) (typed FeaturePython)
  n = 38
  ref = H_element
FEATURE [App::DocumentObjectGroupPython] C_element127  label="C_element : 072"  # scripted group (container) (typed FeaturePython)
  n = 18
  ref = C_element
FEATURE [App::DocumentObjectGroupPython] O_element110  label="O_element : 063"  # scripted group (container) (typed FeaturePython)
  n = 1
  ref = O_element
FEATURE [App::DocumentObjectGroupPython] G4_OCTADECANOL  # scripted group (container) (typed FeaturePython)
  Dunit = g/cm3
  Dvalue = 0.812
  Group = -> [H_element117,C_element127,O_element110]
  conduct = 2
  density = 1
  expand = 3
  formula = G4_OCTADECANOL
  name = G4_OCTADECANOL
  specific = 4
FEATURE [App::DocumentObjectGroupPython] HEP  # scripted group (container) (typed FeaturePython)
  Group = -> [G4_lH2,G4_lN2,G4_lO2,G4_lAr,G4_lBr,G4_lKr,G4_lXe,G4_PbWO4,G4_Galactic,G4_GRAPHITE_POROUS,G4_LUCITE,G4_BRASS,G4_BRONZE,G4_STAINLESS_STEEL,G4_CR39,G4_OCTADECANOL]
FEATURE [App::DocumentObjectGroupPython] C_element128  label="C_element : 073"  # scripted group (container) (typed FeaturePython)
  n = 14
  ref = C_element
FEATURE [App::DocumentObjectGroupPython] H_element118  label="H_element : 065"  # scripted group (container) (typed FeaturePython)
  n = 10
  ref = H_element
FEATURE [App::DocumentObjectGroupPython] O_element111  label="O_element : 064"  # scripted group (container) (typed FeaturePython)
  n = 2
  ref = O_element
FEATURE [App::DocumentObjectGroupPython] N_element050  label="N_element : 023"  # scripted group (container) (typed FeaturePython)
  n = 2
  ref = N_element
FEATURE [App::DocumentObjectGroupPython] G4_KEVLAR  # scripted group (container) (typed FeaturePython)
  Dunit = g/cm3
  Dvalue = 1.44
  Group = -> [C_element128,H_element118,O_element111,N_element050]
  conduct = 2
  density = 1
  expand = 3
  formula = G4_KEVLAR
  name = G4_KEVLAR
  specific = 4
FEATURE [App::DocumentObjectGroupPython] C_element129  label="C_element : 074"  # scripted group (container) (typed FeaturePython)
  n = 10
  ref = C_element
FEATURE [App::DocumentObjectGroupPython] H_element119  label="H_element : 066"  # scripted group (container) (typed FeaturePython)
  n = 8
  ref = H_element
FEATURE [App::DocumentObjectGroupPython] O_element112  label="O_element : 065"  # scripted group (container) (typed FeaturePython)
  n = 4
  ref = O_element
FEATURE [App::DocumentObjectGroupPython] G4_DACRON  # scripted group (container) (typed FeaturePython)
  Dunit = g/cm3
  Dvalue = 1.4
  Group = -> [C_element129,H_element119,O_element112]
  conduct = 2
  density = 1
  expand = 3
  formula = G4_DACRON
  name = G4_DACRON
  specific = 4
FEATURE [App::DocumentObjectGroupPython] C_element130  label="C_element : 075"  # scripted group (container) (typed FeaturePython)
  n = 4
  ref = C_element
FEATURE [App::DocumentObjectGroupPython] H_element120  label="H_element : 067"  # scripted group (container) (typed FeaturePython)
  n = 5
  ref = H_element
FEATURE [App::DocumentObjectGroupPython] Cl_element030  label="Cl_element : 016"  # scripted group (container) (typed FeaturePython)
  n = 1
  ref = Cl_element
FEATURE [App::DocumentObjectGroupPython] G4_NEOPRENE  # scripted group (container) (typed FeaturePython)
  Dunit = g/cm3
  Dvalue = 1.23
  Group = -> [C_element130,H_element120,Cl_element030]
  conduct = 2
  density = 1
  expand = 3
  formula = G4_NEOPRENE
  name = G4_NEOPRENE
  specific = 4
FEATURE [App::DocumentObjectGroupPython] Space  # scripted group (container) (typed FeaturePython)
  Group = -> [G4_KEVLAR,G4_DACRON,G4_NEOPRENE]
FEATURE [App::DocumentObjectGroupPython] H_element121  label="H_element : 068"  # scripted group (container) (typed FeaturePython)
  n = 5
  ref = H_element
FEATURE [App::DocumentObjectGroupPython] C_element131  label="C_element : 076"  # scripted group (container) (typed FeaturePython)
  n = 4
  ref = C_element
FEATURE [App::DocumentObjectGroupPython] N_element051  label="N_element : 3"  # scripted group (container) (typed FeaturePython)
  n = 3
  ref = N_element
FEATURE [App::DocumentObjectGroupPython] O_element113  label="O_element : 066"  # scripted group (container) (typed FeaturePython)
  n = 1
  ref = O_element
FEATURE [App::DocumentObjectGroupPython] G4_CYTOSINE  # scripted group (container) (typed FeaturePython)
  Dunit = g/cm3
  Dvalue = 1.55
  Group = -> [H_element121,C_element131,N_element051,O_element113]
  conduct = 2
  density = 1
  expand = 3
  formula = G4_CYTOSINE
  name = G4_CYTOSINE
  specific = 4
FEATURE [App::DocumentObjectGroupPython] H_element122  label="H_element : 069"  # scripted group (container) (typed FeaturePython)
  n = 6
  ref = H_element
FEATURE [App::DocumentObjectGroupPython] C_element132  label="C_element : 077"  # scripted group (container) (typed FeaturePython)
  n = 5
  ref = C_element
FEATURE [App::DocumentObjectGroupPython] N_element052  label="N_element : 024"  # scripted group (container) (typed FeaturePython)
  n = 2
  ref = N_element
FEATURE [App::DocumentObjectGroupPython] O_element114  label="O_element : 067"  # scripted group (container) (typed FeaturePython)
  n = 2
  ref = O_element
FEATURE [App::DocumentObjectGroupPython] G4_THYMINE  # scripted group (container) (typed FeaturePython)
  Dunit = g/cm3
  Dvalue = 1.23
  Group = -> [H_element122,C_element132,N_element052,O_element114]
  conduct = 2
  density = 1
  expand = 3
  formula = G4_THYMINE
  name = G4_THYMINE
  specific = 4
FEATURE [App::DocumentObjectGroupPython] H_element123  label="H_element : 070"  # scripted group (container) (typed FeaturePython)
  n = 4
  ref = H_element
FEATURE [App::DocumentObjectGroupPython] C_element133  label="C_element : 078"  # scripted group (container) (typed FeaturePython)
  n = 4
  ref = C_element
FEATURE [App::DocumentObjectGroupPython] N_element053  label="N_element : 025"  # scripted group (container) (typed FeaturePython)
  n = 2
  ref = N_element
FEATURE [App::DocumentObjectGroupPython] O_element115  label="O_element : 068"  # scripted group (container) (typed FeaturePython)
  n = 2
  ref = O_element
FEATURE [App::DocumentObjectGroupPython] G4_URACIL  # scripted group (container) (typed FeaturePython)
  Dunit = g/cm3
  Dvalue = 1.32
  Group = -> [H_element123,C_element133,N_element053,O_element115]
  conduct = 2
  density = 1
  expand = 3
  formula = G4_URACIL
  name = G4_URACIL
  specific = 4
FEATURE [App::DocumentObjectGroupPython] H_element124  label="H_element : 071"  # scripted group (container) (typed FeaturePython)
  n = 4
  ref = H_element
FEATURE [App::DocumentObjectGroupPython] C_element134  label="C_element : 079"  # scripted group (container) (typed FeaturePython)
  n = 5
  ref = C_element
FEATURE [App::DocumentObjectGroupPython] N_element054  label="N_element : 026"  # scripted group (container) (typed FeaturePython)
  n = 5
  ref = N_element
FEATURE [App::DocumentObjectGroupPython] G4_DNA_ADENINE  # scripted group (container) (typed FeaturePython)
  Dunit = g/cm3
  Dvalue = 1
  Group = -> [H_element124,C_element134,N_element054]
  conduct = 2
  density = 1
  expand = 3
  formula = G4_DNA_ADENINE
  name = G4_DNA_ADENINE
  specific = 4
FEATURE [App::DocumentObjectGroupPython] H_element125  label="H_element : 072"  # scripted group (container) (typed FeaturePython)
  n = 4
  ref = H_element
FEATURE [App::DocumentObjectGroupPython] C_element135  label="C_element : 080"  # scripted group (container) (typed FeaturePython)
  n = 5
  ref = C_element
FEATURE [App::DocumentObjectGroupPython] N_element055  label="N_element : 027"  # scripted group (container) (typed FeaturePython)
  n = 5
  ref = N_element
FEATURE [App::DocumentObjectGroupPython] O_element116  label="O_element : 069"  # scripted group (container) (typed FeaturePython)
  n = 1
  ref = O_element
FEATURE [App::DocumentObjectGroupPython] G4_DNA_GUANINE  # scripted group (container) (typed FeaturePython)
  Dunit = g/cm3
  Dvalue = 1
  Group = -> [H_element125,C_element135,N_element055,O_element116]
  conduct = 2
  density = 1
  expand = 3
  formula = G4_DNA_GUANINE
  name = G4_DNA_GUANINE
  specific = 4
FEATURE [App::DocumentObjectGroupPython] H_element126  label="H_element : 073"  # scripted group (container) (typed FeaturePython)
  n = 4
  ref = H_element
FEATURE [App::DocumentObjectGroupPython] C_element136  label="C_element : 081"  # scripted group (container) (typed FeaturePython)
  n = 4
  ref = C_element
FEATURE [App::DocumentObjectGroupPython] N_element056  label="N_element : 028"  # scripted group (container) (typed FeaturePython)
  n = 3
  ref = N_element
FEATURE [App::DocumentObjectGroupPython] O_element117  label="O_element : 070"  # scripted group (container) (typed FeaturePython)
  n = 1
  ref = O_element
FEATURE [App::DocumentObjectGroupPython] G4_DNA_CYTOSINE  # scripted group (container) (typed FeaturePython)
  Dunit = g/cm3
  Dvalue = 1
  Group = -> [H_element126,C_element136,N_element056,O_element117]
  conduct = 2
  density = 1
  expand = 3
  formula = G4_DNA_CYTOSINE
  name = G4_DNA_CYTOSINE
  specific = 4
FEATURE [App::DocumentObjectGroupPython] H_element127  label="H_element : 074"  # scripted group (container) (typed FeaturePython)
  n = 5
  ref = H_element
FEATURE [App::DocumentObjectGroupPython] C_element137  label="C_element : 082"  # scripted group (container) (typed FeaturePython)
  n = 5
  ref = C_element
FEATURE [App::DocumentObjectGroupPython] N_element057  label="N_element : 029"  # scripted group (container) (typed FeaturePython)
  n = 2
  ref = N_element
FEATURE [App::DocumentObjectGroupPython] O_element118  label="O_element : 071"  # scripted group (container) (typed FeaturePython)
  n = 2
  ref = O_element
FEATURE [App::DocumentObjectGroupPython] G4_DNA_THYMINE  # scripted group (container) (typed FeaturePython)
  Dunit = g/cm3
  Dvalue = 1
  Group = -> [H_element127,C_element137,N_element057,O_element118]
  conduct = 2
  density = 1
  expand = 3
  formula = G4_DNA_THYMINE
  name = G4_DNA_THYMINE
  specific = 4
FEATURE [App::DocumentObjectGroupPython] H_element128  label="H_element : 075"  # scripted group (container) (typed FeaturePython)
  n = 3
  ref = H_element
FEATURE [App::DocumentObjectGroupPython] C_element138  label="C_element : 083"  # scripted group (container) (typed FeaturePython)
  n = 4
  ref = C_element
FEATURE [App::DocumentObjectGroupPython] N_element058  label="N_element : 030"  # scripted group (container) (typed FeaturePython)
  n = 2
  ref = N_element
FEATURE [App::DocumentObjectGroupPython] O_element119  label="O_element : 072"  # scripted group (container) (typed FeaturePython)
  n = 2
  ref = O_element
FEATURE [App::DocumentObjectGroupPython] G4_DNA_URACIL  # scripted group (container) (typed FeaturePython)
  Dunit = g/cm3
  Dvalue = 1
  Group = -> [H_element128,C_element138,N_element058,O_element119]
  conduct = 2
  density = 1
  expand = 3
  formula = G4_DNA_URACIL
  name = G4_DNA_URACIL
  specific = 4
FEATURE [App::DocumentObjectGroupPython] H_element129  label="H_element : 076"  # scripted group (container) (typed FeaturePython)
  n = 10
  ref = H_element
FEATURE [App::DocumentObjectGroupPython] C_element139  label="C_element : 084"  # scripted group (container) (typed FeaturePython)
  n = 10
  ref = C_element
FEATURE [App::DocumentObjectGroupPython] N_element059  label="N_element : 031"  # scripted group (container) (typed FeaturePython)
  n = 5
  ref = N_element
FEATURE [App::DocumentObjectGroupPython] O_element120  label="O_element : 073"  # scripted group (container) (typed FeaturePython)
  n = 4
  ref = O_element
FEATURE [App::DocumentObjectGroupPython] G4_DNA_ADENOSINE  # scripted group (container) (typed FeaturePython)
  Dunit = g/cm3
  Dvalue = 1
  Group = -> [H_element129,C_element139,N_element059,O_element120]
  conduct = 2
  density = 1
  expand = 3
  formula = G4_DNA_ADENOSINE
  name = G4_DNA_ADENOSINE
  specific = 4
FEATURE [App::DocumentObjectGroupPython] H_element130  label="H_element : 077"  # scripted group (container) (typed FeaturePython)
  n = 10
  ref = H_element
FEATURE [App::DocumentObjectGroupPython] C_element140  label="C_element : 085"  # scripted group (container) (typed FeaturePython)
  n = 10
  ref = C_element
FEATURE [App::DocumentObjectGroupPython] N_element060  label="N_element : 032"  # scripted group (container) (typed FeaturePython)
  n = 5
  ref = N_element
FEATURE [App::DocumentObjectGroupPython] O_element121  label="O_element : 074"  # scripted group (container) (typed FeaturePython)
  n = 5
  ref = O_element
FEATURE [App::DocumentObjectGroupPython] G4_DNA_GUANOSINE  # scripted group (container) (typed FeaturePython)
  Dunit = g/cm3
  Dvalue = 1
  Group = -> [H_element130,C_element140,N_element060,O_element121]
  conduct = 2
  density = 1
  expand = 3
  formula = G4_DNA_GUANOSINE
  name = G4_DNA_GUANOSINE
  specific = 4
FEATURE [App::DocumentObjectGroupPython] H_element131  label="H_element : 078"  # scripted group (container) (typed FeaturePython)
  n = 10
  ref = H_element
FEATURE [App::DocumentObjectGroupPython] C_element141  label="C_element : 086"  # scripted group (container) (typed FeaturePython)
  n = 9
  ref = C_element
FEATURE [App::DocumentObjectGroupPython] N_element061  label="N_element : 033"  # scripted group (container) (typed FeaturePython)
  n = 3
  ref = N_element
FEATURE [App::DocumentObjectGroupPython] O_element122  label="O_element : 075"  # scripted group (container) (typed FeaturePython)
  n = 5
  ref = O_element
FEATURE [App::DocumentObjectGroupPython] G4_DNA_CYTIDINE  # scripted group (container) (typed FeaturePython)
  Dunit = g/cm3
  Dvalue = 1
  Group = -> [H_element131,C_element141,N_element061,O_element122]
  conduct = 2
  density = 1
  expand = 3
  formula = G4_DNA_CYTIDINE
  name = G4_DNA_CYTIDINE
  specific = 4
FEATURE [App::DocumentObjectGroupPython] H_element132  label="H_element : 079"  # scripted group (container) (typed FeaturePython)
  n = 9
  ref = H_element
FEATURE [App::DocumentObjectGroupPython] C_element142  label="C_element : 087"  # scripted group (container) (typed FeaturePython)
  n = 9
  ref = C_element
FEATURE [App::DocumentObjectGroupPython] N_element062  label="N_element : 034"  # scripted group (container) (typed FeaturePython)
  n = 2
  ref = N_element
FEATURE [App::DocumentObjectGroupPython] O_element123  label="O_element : 076"  # scripted group (container) (typed FeaturePython)
  n = 6
  ref = O_element
FEATURE [App::DocumentObjectGroupPython] G4_DNA_URIDINE  # scripted group (container) (typed FeaturePython)
  Dunit = g/cm3
  Dvalue = 1
  Group = -> [H_element132,C_element142,N_element062,O_element123]
  conduct = 2
  density = 1
  expand = 3
  formula = G4_DNA_URIDINE
  name = G4_DNA_URIDINE
  specific = 4
FEATURE [App::DocumentObjectGroupPython] H_element133  label="H_element : 080"  # scripted group (container) (typed FeaturePython)
  n = 11
  ref = H_element
FEATURE [App::DocumentObjectGroupPython] C_element143  label="C_element : 088"  # scripted group (container) (typed FeaturePython)
  n = 10
  ref = C_element
FEATURE [App::DocumentObjectGroupPython] N_element063  label="N_element : 035"  # scripted group (container) (typed FeaturePython)
  n = 2
  ref = N_element
FEATURE [App::DocumentObjectGroupPython] O_element124  label="O_element : 077"  # scripted group (container) (typed FeaturePython)
  n = 6
  ref = O_element
FEATURE [App::DocumentObjectGroupPython] G4_DNA_METHYLURIDINE  # scripted group (container) (typed FeaturePython)
  Dunit = g/cm3
  Dvalue = 1
  Group = -> [H_element133,C_element143,N_element063,O_element124]
  conduct = 2
  density = 1
  expand = 3
  formula = G4_DNA_METHYLURIDINE
  name = G4_DNA_METHYLURIDINE
  specific = 4
FEATURE [App::DocumentObjectGroupPython] P_element014  label="P_element : 003"  # scripted group (container) (typed FeaturePython)
  n = 1
  ref = P_element
FEATURE [App::DocumentObjectGroupPython] O_element125  label="O_element : 078"  # scripted group (container) (typed FeaturePython)
  n = 3
  ref = O_element
FEATURE [App::DocumentObjectGroupPython] G4_DNA_MONOPHOSPHATE  # scripted group (container) (typed FeaturePython)
  Dunit = g/cm3
  Dvalue = 1
  Group = -> [P_element014,O_element125]
  conduct = 2
  density = 1
  expand = 3
  formula = G4_DNA_MONOPHOSPHATE
  name = G4_DNA_MONOPHOSPHATE
  specific = 4
FEATURE [App::DocumentObjectGroupPython] H_element134  label="H_element : 081"  # scripted group (container) (typed FeaturePython)
  n = 10
  ref = H_element
FEATURE [App::DocumentObjectGroupPython] C_element144  label="C_element : 089"  # scripted group (container) (typed FeaturePython)
  n = 10
  ref = C_element
FEATURE [App::DocumentObjectGroupPython] N_element064  label="N_element : 036"  # scripted group (container) (typed FeaturePython)
  n = 5
  ref = N_element
FEATURE [App::DocumentObjectGroupPython] O_element126  label="O_element : 079"  # scripted group (container) (typed FeaturePython)
  n = 7
  ref = O_element
FEATURE [App::DocumentObjectGroupPython] P_element015  label="P_element : 004"  # scripted group (container) (typed FeaturePython)
  n = 1
  ref = P_element
FEATURE [App::DocumentObjectGroupPython] G4_DNA_A  # scripted group (container) (typed FeaturePython)
  Dunit = g/cm3
  Dvalue = 1
  Group = -> [H_element134,C_element144,N_element064,O_element126,P_element015]
  conduct = 2
  density = 1
  expand = 3
  formula = G4_DNA_A
  name = G4_DNA_A
  specific = 4
FEATURE [App::DocumentObjectGroupPython] H_element135  label="H_element : 082"  # scripted group (container) (typed FeaturePython)
  n = 10
  ref = H_element
FEATURE [App::DocumentObjectGroupPython] C_element145  label="C_element : 090"  # scripted group (container) (typed FeaturePython)
  n = 10
  ref = C_element
FEATURE [App::DocumentObjectGroupPython] N_element065  label="N_element : 037"  # scripted group (container) (typed FeaturePython)
  n = 5
  ref = N_element
FEATURE [App::DocumentObjectGroupPython] O_element127  label="O_element : 8"  # scripted group (container) (typed FeaturePython)
  n = 8
  ref = O_element
FEATURE [App::DocumentObjectGroupPython] P_element016  label="P_element : 005"  # scripted group (container) (typed FeaturePython)
  n = 1
  ref = P_element
FEATURE [App::DocumentObjectGroupPython] G4_DNA_G  # scripted group (container) (typed FeaturePython)
  Dunit = g/cm3
  Dvalue = 1
  Group = -> [H_element135,C_element145,N_element065,O_element127,P_element016]
  conduct = 2
  density = 1
  expand = 3
  formula = G4_DNA_G
  name = G4_DNA_G
  specific = 4
FEATURE [App::DocumentObjectGroupPython] H_element136  label="H_element : 083"  # scripted group (container) (typed FeaturePython)
  n = 10
  ref = H_element
FEATURE [App::DocumentObjectGroupPython] C_element146  label="C_element : 091"  # scripted group (container) (typed FeaturePython)
  n = 9
  ref = C_element
FEATURE [App::DocumentObjectGroupPython] N_element066  label="N_element : 038"  # scripted group (container) (typed FeaturePython)
  n = 3
  ref = N_element
FEATURE [App::DocumentObjectGroupPython] O_element128  label="O_element : 080"  # scripted group (container) (typed FeaturePython)
  n = 8
  ref = O_element
FEATURE [App::DocumentObjectGroupPython] P_element017  label="P_element : 006"  # scripted group (container) (typed FeaturePython)
  n = 1
  ref = P_element
FEATURE [App::DocumentObjectGroupPython] G4_DNA_C  # scripted group (container) (typed FeaturePython)
  Dunit = g/cm3
  Dvalue = 1
  Group = -> [H_element136,C_element146,N_element066,O_element128,P_element017]
  conduct = 2
  density = 1
  expand = 3
  formula = G4_DNA_C
  name = G4_DNA_C
  specific = 4
FEATURE [App::DocumentObjectGroupPython] H_element137  label="H_element : 084"  # scripted group (container) (typed FeaturePython)
  n = 9
  ref = H_element
FEATURE [App::DocumentObjectGroupPython] C_element147  label="C_element : 092"  # scripted group (container) (typed FeaturePython)
  n = 9
  ref = C_element
FEATURE [App::DocumentObjectGroupPython] N_element067  label="N_element : 039"  # scripted group (container) (typed FeaturePython)
  n = 2
  ref = N_element
FEATURE [App::DocumentObjectGroupPython] O_element129  label="O_element : 9"  # scripted group (container) (typed FeaturePython)
  n = 9
  ref = O_element
FEATURE [App::DocumentObjectGroupPython] P_element018  label="P_element : 007"  # scripted group (container) (typed FeaturePython)
  n = 1
  ref = P_element
FEATURE [App::DocumentObjectGroupPython] G4_DNA_U  # scripted group (container) (typed FeaturePython)
  Dunit = g/cm3
  Dvalue = 1
  Group = -> [H_element137,C_element147,N_element067,O_element129,P_element018]
  conduct = 2
  density = 1
  expand = 3
  formula = G4_DNA_U
  name = G4_DNA_U
  specific = 4
FEATURE [App::DocumentObjectGroupPython] H_element138  label="H_element : 085"  # scripted group (container) (typed FeaturePython)
  n = 11
  ref = H_element
FEATURE [App::DocumentObjectGroupPython] C_element148  label="C_element : 093"  # scripted group (container) (typed FeaturePython)
  n = 10
  ref = C_element
FEATURE [App::DocumentObjectGroupPython] N_element068  label="N_element : 040"  # scripted group (container) (typed FeaturePython)
  n = 2
  ref = N_element
FEATURE [App::DocumentObjectGroupPython] O_element130  label="O_element : 081"  # scripted group (container) (typed FeaturePython)
  n = 9
  ref = O_element
FEATURE [App::DocumentObjectGroupPython] P_element019  label="P_element : 008"  # scripted group (container) (typed FeaturePython)
  n = 1
  ref = P_element
FEATURE [App::DocumentObjectGroupPython] G4_DNA_MU  # scripted group (container) (typed FeaturePython)
  Dunit = g/cm3
  Dvalue = 1
  Group = -> [H_element138,C_element148,N_element068,O_element130,P_element019]
  conduct = 2
  density = 1
  expand = 3
  formula = G4_DNA_MU
  name = G4_DNA_MU
  specific = 4
FEATURE [App::DocumentObjectGroupPython] BioChemical  # scripted group (container) (typed FeaturePython)
  Group = -> [G4_CYTOSINE,G4_THYMINE,G4_URACIL,G4_DNA_ADENINE,G4_DNA_GUANINE,G4_DNA_CYTOSINE,G4_DNA_THYMINE,G4_DNA_URACIL,G4_DNA_ADENOSINE,G4_DNA_GUANOSINE,G4_DNA_CYTIDINE,G4_DNA_URIDINE,G4_DNA_METHYLURIDINE,G4_DNA_MONOPHOSPHATE,G4_DNA_A,G4_DNA_G,G4_DNA_C,G4_DNA_U,G4_DNA_MU]
FEATURE [App::DocumentObjectGroupPython] G4Materials  # scripted group (container) (typed FeaturePython)
  Group = -> [NIST,Element,HEP,Space,BioChemical]
  version = 1
FEATURE [App::DocumentObjectGroupPython] Geant4  # scripted group (container) (typed FeaturePython)
  Group = -> [G4Isotopes,G4Elements,G4Materials]
FEATURE [App::DocumentObjectGroupPython] Materials  # scripted group (container) (typed FeaturePython)
  Group = -> [Geant4]
FEATURE [Part::FeaturePython] GDMLBox_WorldBox  # WARN: FeaturePython — macro-defined, semantics opaque (R4)
  lunit = 2
  material = 5
  x = 20
  y = 20
  z = 20
FEATURE [Sketcher::SketchObject] Sketch
  ArcFitTolerance = 0
  FullyConstrained = false
  MakeInternals = false
  sketch-geometry (4):
    g0: ArcOfCircle CenterX=0 CenterY=0 CenterZ=0 NormalX=0 NormalY=0 NormalZ=1 AngleXU=0 Radius=5.61268 StartAngle=0 EndAngle=3.14159
    g1: LineSegment StartX=5.61268 StartY=0 StartZ=0 EndX=0.046736 EndY=1.79644 EndZ=0
    g2: LineSegment StartX=0.046736 StartY=1.79644 StartZ=0 EndX=-1.78598 EndY=-2.14051 EndZ=0
    g3: LineSegment StartX=-1.78598 StartY=-2.14051 StartZ=0 EndX=-5.61268 EndY=1e-15 EndZ=0
  constraints (7):
    c: Coincident(g0,g-1)
    c: PointOnObject(g0,g-1)
    c: PointOnObject(g0,g-1)
    c: Coincident(g0,g1)
    c: Coincident(g1,g2)
    c: Coincident(g2,g3)
    c: Coincident(g3,g0)
FEATURE [Part::Extrusion] Extrude
  Base = -> Sketch
  Dir = (0,0,1)
  DirMode = 2
  FaceMakerClass = Part::FaceMakerBullseye
  FaceMakerMode = 3
  LengthFwd = 10
  LengthRev = 0
  Solid = true
  Symmetric = false
FEATURE [App::Part] Part
  Group = -> [Sketch,Extrude]
  Origin = -> Origin001
FEATURE [App::Part] worldVOL
  Group = -> [GDMLBox_WorldBox,Part]
  Origin = -> Origin
